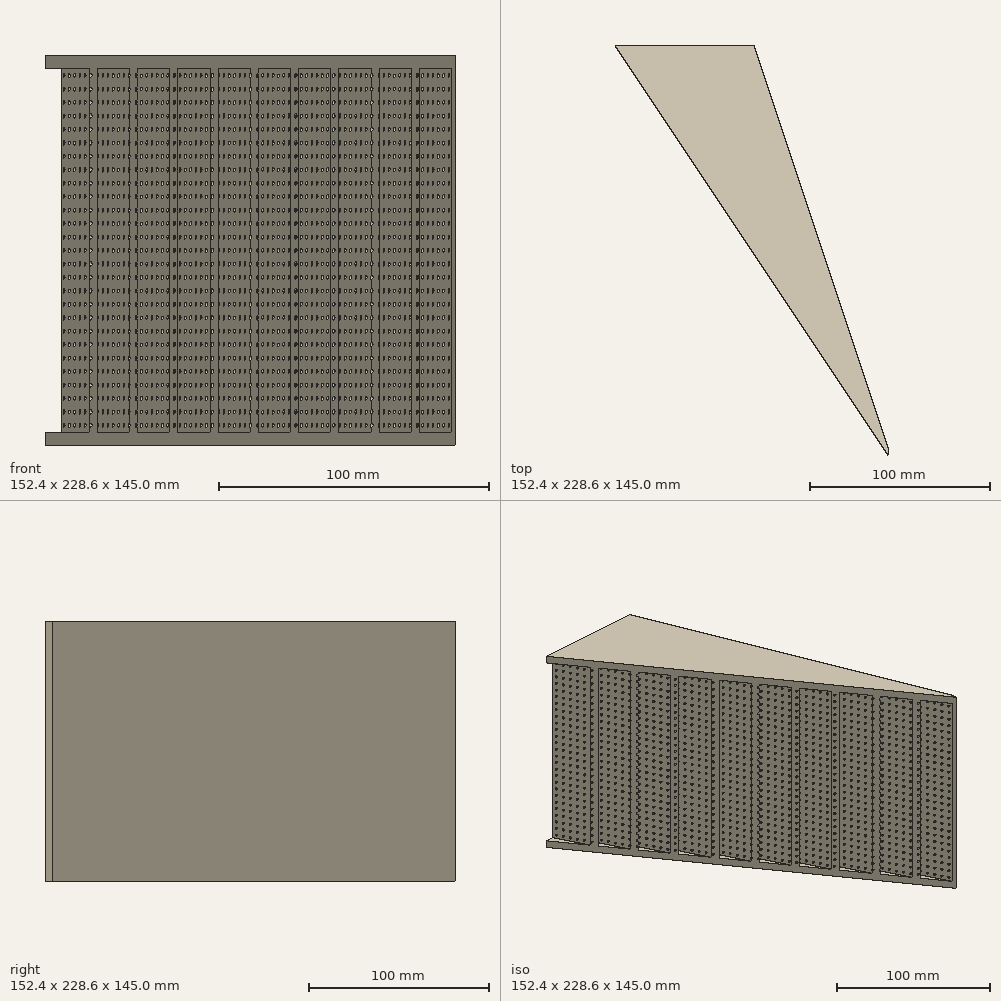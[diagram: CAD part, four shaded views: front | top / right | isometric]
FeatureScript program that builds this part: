
annotation { "Feature Type Name" : "Feature", "Feature Type Description" : "" }
export const myFeature = defineFeature(function(context is Context, id is Id, definition is map)
    precondition{}
    {
        {
            var Q0;
            Q0=qCreatedBy(makeId("Top.planeOp"),FACE);
            var sketch = newSketch(context, id + "F0", { "sketchPlane" : qUnion([Q0])});
            skLineSegment(sketch, "E0", {"start": v(0, -87) * mm, "end": v(0, 141.6) * mm});
            skLineSegment(sketch, "E1", {"start": v(0, -87) * mm, "end": v(-76.2, 141.6) * mm});
            skLineSegment(sketch, "E2", {"start": v(-76.2, 141.6) * mm, "end": v(0, 141.6) * mm});
            skLineSegment(sketch, "E3", {"start": v(0, -87) * mm, "end": v(-152.4, 141.6) * mm});
            skLineSegment(sketch, "E4", {"start": v(-152.4, 141.6) * mm, "end": v(-76.2, 141.6) * mm});
            skLineSegment(sketch, "E5", {"start": v(-97.03, 141.6) * mm, "end": v(0, -87) * mm});
            skLineSegment(sketch, "E6", {"start": v(-102.47, 141.6) * mm, "end": v(-14.95, -64.57) * mm});
            skLineSegment(sketch, "E7", {"start": v(-107.9, 141.6) * mm, "end": v(-29.9, -42.14) * mm});
            skLineSegment(sketch, "E8", {"start": v(-113.33, 141.6) * mm, "end": v(-44.86, -19.7) * mm});
            skLineSegment(sketch, "E9.1.0.0", {"start": v(-118.76, 141.6) * mm, "end": v(-59.8, 2.72) * mm});
            skLineSegment(sketch, "E9.2.0.0", {"start": v(-124.2, 141.6) * mm, "end": v(-74.76, 25.15) * mm});
            skLineSegment(sketch, "E9.3.0.0", {"start": v(-129.63, 141.6) * mm, "end": v(-89.71, 47.57) * mm});
            skLineSegment(sketch, "E9.4.0.0", {"start": v(-135.06, 141.6) * mm, "end": v(-104.66, 70) * mm});
            skLineSegment(sketch, "E9.5.0.0", {"start": v(-140.49, 141.6) * mm, "end": v(-119.61, 92.43) * mm});
            skLineSegment(sketch, "E9.6.0.0", {"start": v(-145.92, 141.6) * mm, "end": v(-134.57, 114.86) * mm});
            skLineSegment(sketch, "E10.1.0.0", {"start": v(-91.6, 141.6) * mm, "end": v(-19.87, -27.4) * mm});
            skLineSegment(sketch, "E10.2.0.0", {"start": v(-86.17, 141.6) * mm, "end": v(-39.73, 32.2) * mm});
            skLineSegment(sketch, "E11", {"start": v(-80.74, 141.6) * mm, "end": v(-59.6, 91.8) * mm});
            skLineSegment(sketch, "E12", {"start": v(-81.28, 141.6) * mm, "end": v(-57.61, 85.84) * mm});
            skLineSegment(sketch, "E13", {"start": v(-80.2, 141.6) * mm, "end": v(-61.58, 97.76) * mm});
            skLineSegment(sketch, "E14", {"start": v(-86.71, 141.6) * mm, "end": v(-37.75, 26.24) * mm});
            skLineSegment(sketch, "E15", {"start": v(-85.63, 141.6) * mm, "end": v(-41.72, 38.16) * mm});
            skLineSegment(sketch, "E16", {"start": v(-92.15, 141.6) * mm, "end": v(-17.88, -33.36) * mm});
            skLineSegment(sketch, "E17", {"start": v(-91.06, 141.6) * mm, "end": v(-21.85, -21.44) * mm});
            skLineSegment(sketch, "E18", {"start": v(-97.58, 141.6) * mm, "end": v(-1.5, -84.75) * mm});
            skLineSegment(sketch, "E19", {"start": v(-96.5, 141.6) * mm, "end": v(-1.99, -81.03) * mm});
            skLineSegment(sketch, "E20", {"start": v(-103, 141.6) * mm, "end": v(-16.45, -62.32) * mm});
            skLineSegment(sketch, "E21", {"start": v(-101.92, 141.6) * mm, "end": v(-13.46, -66.8) * mm});
            skLineSegment(sketch, "E22", {"start": v(-108.44, 141.6) * mm, "end": v(-31.4, -39.9) * mm});
            skLineSegment(sketch, "E23", {"start": v(-107.36, 141.6) * mm, "end": v(-28.4, -44.38) * mm});
            skLineSegment(sketch, "E24", {"start": v(-113.94, 141.76) * mm, "end": v(-46.35, -17.47) * mm});
            skLineSegment(sketch, "E25", {"start": v(-112.79, 141.6) * mm, "end": v(-43.36, -21.95) * mm});
            skLineSegment(sketch, "E26", {"start": v(-119.3, 141.6) * mm, "end": v(-61.3, 4.96) * mm});
            skLineSegment(sketch, "E27", {"start": v(-118.22, 141.6) * mm, "end": v(-58.31, 0.47) * mm});
            skLineSegment(sketch, "E28", {"start": v(-124.74, 141.6) * mm, "end": v(-76.25, 27.39) * mm});
            skLineSegment(sketch, "E29", {"start": v(-123.65, 141.6) * mm, "end": v(-73.26, 22.9) * mm});
            skLineSegment(sketch, "E30", {"start": v(-130.17, 141.6) * mm, "end": v(-91.2, 49.82) * mm});
            skLineSegment(sketch, "E31", {"start": v(-129.08, 141.6) * mm, "end": v(-88.22, 45.33) * mm});
            skLineSegment(sketch, "E32", {"start": v(-134.51, 141.6) * mm, "end": v(-103.17, 67.76) * mm});
            skLineSegment(sketch, "E33", {"start": v(-135.6, 141.6) * mm, "end": v(-106.16, 72.24) * mm});
            skLineSegment(sketch, "E34", {"start": v(-141.03, 141.6) * mm, "end": v(-121.1, 94.67) * mm});
            skLineSegment(sketch, "E35", {"start": v(-139.95, 141.6) * mm, "end": v(-118.12, 90.19) * mm});
            skLineSegment(sketch, "E36", {"start": v(-146.46, 141.6) * mm, "end": v(-136.06, 117.1) * mm});
            skLineSegment(sketch, "E37", {"start": v(-145.38, 141.6) * mm, "end": v(-133.07, 112.61) * mm});
            skPoint(sketch, "E38.endSnap0", {"position": v(-70.9, 119.68) * mm});
            skLineSegment(sketch, "E39", {"start": v(-74.88, 141.6) * mm, "end": v(1.19, -86.6) * mm});
            skLineSegment(sketch, "E40", {"start": v(1.19, -86.6) * mm, "end": v(0, -87) * mm});
            skSolve(sketch);
        }
        {
            var Q0;
            {var subQ0=sQuery(id+"F0.wireOp",EDGE,"E11");Q0=makeQuery(id+"F0.imprint","IMPRINT",FACE,{"disambiguationData":[TD([[makeQuery(id+"F0.imprint","IMPRINT",EDGE,{"derivedFrom":subQ0}),-1.0]])]});}
            var Q1;
            {var subQ0=sQuery(id+"F0.wireOp",EDGE,"E11");Q1=makeQuery(id+"F0.imprint","IMPRINT",FACE,{"disambiguationData":[TD([[makeQuery(id+"F0.imprint","IMPRINT",EDGE,{"derivedFrom":subQ0}),1.0]])]});}
            var Q2;
            {var subQ0=sQuery(id+"F0.wireOp",EDGE,"E10.2.0.0");Q2=makeQuery(id+"F0.imprint","IMPRINT",FACE,{"disambiguationData":[TD([[makeQuery(id+"F0.imprint","IMPRINT",EDGE,{"derivedFrom":subQ0}),1.0]])]});}
            var Q3;
            {var subQ0=sQuery(id+"F0.wireOp",EDGE,"E10.2.0.0");Q3=makeQuery(id+"F0.imprint","IMPRINT",FACE,{"disambiguationData":[TD([[makeQuery(id+"F0.imprint","IMPRINT",EDGE,{"derivedFrom":subQ0}),-1.0]])]});}
            var Q4;
            {var subQ0=sQuery(id+"F0.wireOp",EDGE,"E10.1.0.0");Q4=makeQuery(id+"F0.imprint","IMPRINT",FACE,{"disambiguationData":[TD([[makeQuery(id+"F0.imprint","IMPRINT",EDGE,{"derivedFrom":subQ0}),1.0]])]});}
            var Q5;
            {var subQ0=sQuery(id+"F0.wireOp",EDGE,"E10.1.0.0");Q5=makeQuery(id+"F0.imprint","IMPRINT",FACE,{"disambiguationData":[TD([[makeQuery(id+"F0.imprint","IMPRINT",EDGE,{"derivedFrom":subQ0}),-1.0]])]});}
            var Q6;
            {var subQ0=sQuery(id+"F0.wireOp",EDGE,"E5");Q6=makeQuery(id+"F0.imprint","IMPRINT",FACE,{"disambiguationData":[TD([[makeQuery(id+"F0.imprint","IMPRINT",EDGE,{"derivedFrom":subQ0}),1.0]])]});}
            var Q7;
            {var subQ0=sQuery(id+"F0.wireOp",EDGE,"E5");Q7=makeQuery(id+"F0.imprint","IMPRINT",FACE,{"disambiguationData":[TD([[makeQuery(id+"F0.imprint","IMPRINT",EDGE,{"derivedFrom":subQ0}),-1.0]])]});}
            var Q8;
            {var subQ0=sQuery(id+"F0.wireOp",EDGE,"E6");Q8=makeQuery(id+"F0.imprint","IMPRINT",FACE,{"disambiguationData":[TD([[makeQuery(id+"F0.imprint","IMPRINT",EDGE,{"derivedFrom":subQ0}),1.0]])]});}
            var Q9;
            {var subQ0=sQuery(id+"F0.wireOp",EDGE,"E6");Q9=makeQuery(id+"F0.imprint","IMPRINT",FACE,{"disambiguationData":[TD([[makeQuery(id+"F0.imprint","IMPRINT",EDGE,{"derivedFrom":subQ0}),-1.0]])]});}
            var Q10;
            {var subQ0=sQuery(id+"F0.wireOp",EDGE,"E7");Q10=makeQuery(id+"F0.imprint","IMPRINT",FACE,{"disambiguationData":[TD([[makeQuery(id+"F0.imprint","IMPRINT",EDGE,{"derivedFrom":subQ0}),1.0]])]});}
            var Q11;
            {var subQ0=sQuery(id+"F0.wireOp",EDGE,"E7");Q11=makeQuery(id+"F0.imprint","IMPRINT",FACE,{"disambiguationData":[TD([[makeQuery(id+"F0.imprint","IMPRINT",EDGE,{"derivedFrom":subQ0}),-1.0]])]});}
            var Q12;
            {var subQ0=sQuery(id+"F0.wireOp",EDGE,"E8");Q12=makeQuery(id+"F0.imprint","IMPRINT",FACE,{"disambiguationData":[TD([[makeQuery(id+"F0.imprint","IMPRINT",EDGE,{"derivedFrom":subQ0}),1.0]])]});}
            var Q13;
            {var subQ0=sQuery(id+"F0.wireOp",EDGE,"E8");Q13=makeQuery(id+"F0.imprint","IMPRINT",FACE,{"disambiguationData":[TD([[makeQuery(id+"F0.imprint","IMPRINT",EDGE,{"derivedFrom":subQ0}),-1.0]])]});}
            var Q14;
            {var subQ0=sQuery(id+"F0.wireOp",EDGE,"E9.1.0.0");Q14=makeQuery(id+"F0.imprint","IMPRINT",FACE,{"disambiguationData":[TD([[makeQuery(id+"F0.imprint","IMPRINT",EDGE,{"derivedFrom":subQ0}),1.0]])]});}
            var Q15;
            {var subQ0=sQuery(id+"F0.wireOp",EDGE,"E9.1.0.0");Q15=makeQuery(id+"F0.imprint","IMPRINT",FACE,{"disambiguationData":[TD([[makeQuery(id+"F0.imprint","IMPRINT",EDGE,{"derivedFrom":subQ0}),-1.0]])]});}
            var Q16;
            {var subQ0=sQuery(id+"F0.wireOp",EDGE,"E9.2.0.0");Q16=makeQuery(id+"F0.imprint","IMPRINT",FACE,{"disambiguationData":[TD([[makeQuery(id+"F0.imprint","IMPRINT",EDGE,{"derivedFrom":subQ0}),1.0]])]});}
            var Q17;
            {var subQ0=sQuery(id+"F0.wireOp",EDGE,"E9.2.0.0");Q17=makeQuery(id+"F0.imprint","IMPRINT",FACE,{"disambiguationData":[TD([[makeQuery(id+"F0.imprint","IMPRINT",EDGE,{"derivedFrom":subQ0}),-1.0]])]});}
            var Q18;
            {var subQ0=sQuery(id+"F0.wireOp",EDGE,"E9.3.0.0");Q18=makeQuery(id+"F0.imprint","IMPRINT",FACE,{"disambiguationData":[TD([[makeQuery(id+"F0.imprint","IMPRINT",EDGE,{"derivedFrom":subQ0}),1.0]])]});}
            var Q19;
            {var subQ0=sQuery(id+"F0.wireOp",EDGE,"E9.3.0.0");Q19=makeQuery(id+"F0.imprint","IMPRINT",FACE,{"disambiguationData":[TD([[makeQuery(id+"F0.imprint","IMPRINT",EDGE,{"derivedFrom":subQ0}),-1.0]])]});}
            var Q20;
            {var subQ0=sQuery(id+"F0.wireOp",EDGE,"E9.4.0.0");Q20=makeQuery(id+"F0.imprint","IMPRINT",FACE,{"disambiguationData":[TD([[makeQuery(id+"F0.imprint","IMPRINT",EDGE,{"derivedFrom":subQ0}),1.0]])]});}
            var Q21;
            {var subQ0=sQuery(id+"F0.wireOp",EDGE,"E9.4.0.0");Q21=makeQuery(id+"F0.imprint","IMPRINT",FACE,{"disambiguationData":[TD([[makeQuery(id+"F0.imprint","IMPRINT",EDGE,{"derivedFrom":subQ0}),-1.0]])]});}
            var Q22;
            {var subQ0=sQuery(id+"F0.wireOp",EDGE,"E9.5.0.0");Q22=makeQuery(id+"F0.imprint","IMPRINT",FACE,{"disambiguationData":[TD([[makeQuery(id+"F0.imprint","IMPRINT",EDGE,{"derivedFrom":subQ0}),1.0]])]});}
            var Q23;
            {var subQ0=sQuery(id+"F0.wireOp",EDGE,"E9.5.0.0");Q23=makeQuery(id+"F0.imprint","IMPRINT",FACE,{"disambiguationData":[TD([[makeQuery(id+"F0.imprint","IMPRINT",EDGE,{"derivedFrom":subQ0}),-1.0]])]});}
            var Q24;
            {var subQ0=sQuery(id+"F0.wireOp",EDGE,"E9.6.0.0");Q24=makeQuery(id+"F0.imprint","IMPRINT",FACE,{"disambiguationData":[TD([[makeQuery(id+"F0.imprint","IMPRINT",EDGE,{"derivedFrom":subQ0}),1.0]])]});}
            var Q25;
            {var subQ0=sQuery(id+"F0.wireOp",EDGE,"E9.6.0.0");Q25=makeQuery(id+"F0.imprint","IMPRINT",FACE,{"disambiguationData":[TD([[makeQuery(id+"F0.imprint","IMPRINT",EDGE,{"derivedFrom":subQ0}),-1.0]])]});}
            extrude(context, id + "F1", {"entities" : qUnion([Q0, Q1, Q2, Q3, Q4, Q5, Q6, Q7, Q8, Q9, Q10, Q11, Q12, Q13, Q14, Q15, Q16, Q17, Q18, Q19, Q20, Q21, Q22, Q23, Q24, Q25]), "depth" : 135 * mm, "offsetDistance" : 25 * mm});
        }
        {
            var Q0;
            Q0=makeQuery(id+"F1.opExtrude","SWEPT_FACE",FACE,{"disambiguationData":[OSD([sQuery(id+"F0.wireOp",EDGE,"E18")])]});
            var sketch = newSketch(context, id + "F2", { "sketchPlane" : qUnion([Q0])});
            skLineSegment(sketch, "E41", {"start": v(77.43, 195) * mm, "end": v(77.43, 135) * mm});
            skLineSegment(sketch, "E42", {"start": v(72.43, 135) * mm, "end": v(77.43, 135) * mm});
            skCircle(sketch, "E43", {"center": v(75, 197.44) * mm, "radius": 0.8 * mm});
            skCircle(sketch, "E44.0.1.0", {"center": v(75, 192.44) * mm, "radius": 0.8 * mm});
            skCircle(sketch, "E44.1.0.0", {"center": v(70, 197.44) * mm, "radius": 0.8 * mm});
            skCircle(sketch, "E44.1.1.0", {"center": v(70, 192.44) * mm, "radius": 0.8 * mm});
            skCircle(sketch, "E44.2.0.0", {"center": v(65, 197.44) * mm, "radius": 0.8 * mm});
            skCircle(sketch, "E44.2.1.0", {"center": v(65, 192.44) * mm, "radius": 0.8 * mm});
            skCircle(sketch, "E44.3.0.0", {"center": v(60, 197.44) * mm, "radius": 0.8 * mm});
            skCircle(sketch, "E44.3.1.0", {"center": v(60, 192.44) * mm, "radius": 0.8 * mm});
            skCircle(sketch, "E44.4.0.0", {"center": v(55, 197.44) * mm, "radius": 0.8 * mm});
            skCircle(sketch, "E44.4.1.0", {"center": v(55, 192.44) * mm, "radius": 0.8 * mm});
            skCircle(sketch, "E44.5.0.0", {"center": v(50, 197.44) * mm, "radius": 0.8 * mm});
            skCircle(sketch, "E44.5.1.0", {"center": v(50, 192.44) * mm, "radius": 0.8 * mm});
            skCircle(sketch, "E44.6.0.0", {"center": v(45, 197.44) * mm, "radius": 0.8 * mm});
            skCircle(sketch, "E44.6.1.0", {"center": v(45, 192.44) * mm, "radius": 0.8 * mm});
            skCircle(sketch, "E44.7.0.0", {"center": v(40, 197.44) * mm, "radius": 0.8 * mm});
            skCircle(sketch, "E44.7.1.0", {"center": v(40, 192.44) * mm, "radius": 0.8 * mm});
            skCircle(sketch, "E44.8.0.0", {"center": v(35, 197.44) * mm, "radius": 0.8 * mm});
            skCircle(sketch, "E44.8.1.0", {"center": v(35, 192.44) * mm, "radius": 0.8 * mm});
            skCircle(sketch, "E44.9.0.0", {"center": v(30, 197.44) * mm, "radius": 0.8 * mm});
            skCircle(sketch, "E44.9.1.0", {"center": v(30, 192.44) * mm, "radius": 0.8 * mm});
            skCircle(sketch, "E44.10.0.0", {"center": v(25, 197.44) * mm, "radius": 0.8 * mm});
            skCircle(sketch, "E44.10.1.0", {"center": v(25, 192.44) * mm, "radius": 0.8 * mm});
            skCircle(sketch, "E44.11.0.0", {"center": v(20, 197.44) * mm, "radius": 0.8 * mm});
            skCircle(sketch, "E44.11.1.0", {"center": v(20, 192.44) * mm, "radius": 0.8 * mm});
            skCircle(sketch, "E44.12.0.0", {"center": v(15, 197.44) * mm, "radius": 0.8 * mm});
            skCircle(sketch, "E44.12.1.0", {"center": v(15, 192.44) * mm, "radius": 0.8 * mm});
            skCircle(sketch, "E44.13.0.0", {"center": v(10, 197.44) * mm, "radius": 0.8 * mm});
            skCircle(sketch, "E44.13.1.0", {"center": v(10, 192.44) * mm, "radius": 0.8 * mm});
            skCircle(sketch, "E44.14.0.0", {"center": v(5, 197.44) * mm, "radius": 0.8 * mm});
            skCircle(sketch, "E44.14.1.0", {"center": v(5, 192.44) * mm, "radius": 0.8 * mm});
            skCircle(sketch, "E44.15.0.0", {"center": v(0, 197.44) * mm, "radius": 0.8 * mm});
            skCircle(sketch, "E44.15.1.0", {"center": v(0, 192.44) * mm, "radius": 0.8 * mm});
            skCircle(sketch, "E44.16.0.0", {"center": v(-5, 197.44) * mm, "radius": 0.8 * mm});
            skCircle(sketch, "E44.16.1.0", {"center": v(-5, 192.44) * mm, "radius": 0.8 * mm});
            skCircle(sketch, "E44.17.0.0", {"center": v(-10, 197.44) * mm, "radius": 0.8 * mm});
            skCircle(sketch, "E44.17.1.0", {"center": v(-10, 192.44) * mm, "radius": 0.8 * mm});
            skCircle(sketch, "E44.18.0.0", {"center": v(-15, 197.44) * mm, "radius": 0.8 * mm});
            skCircle(sketch, "E44.18.1.0", {"center": v(-15, 192.44) * mm, "radius": 0.8 * mm});
            skCircle(sketch, "E44.19.0.0", {"center": v(-20, 197.44) * mm, "radius": 0.8 * mm});
            skCircle(sketch, "E44.19.1.0", {"center": v(-20, 192.44) * mm, "radius": 0.8 * mm});
            skCircle(sketch, "E44.20.0.0", {"center": v(-25, 197.44) * mm, "radius": 0.8 * mm});
            skCircle(sketch, "E44.20.1.0", {"center": v(-25, 192.44) * mm, "radius": 0.8 * mm});
            skCircle(sketch, "E44.21.0.0", {"center": v(-30, 197.44) * mm, "radius": 0.8 * mm});
            skCircle(sketch, "E44.21.1.0", {"center": v(-30, 192.44) * mm, "radius": 0.8 * mm});
            skCircle(sketch, "E44.22.0.0", {"center": v(-35, 197.44) * mm, "radius": 0.8 * mm});
            skCircle(sketch, "E44.22.1.0", {"center": v(-35, 192.44) * mm, "radius": 0.8 * mm});
            skCircle(sketch, "E44.23.0.0", {"center": v(-40, 197.44) * mm, "radius": 0.8 * mm});
            skCircle(sketch, "E44.23.1.0", {"center": v(-40, 192.44) * mm, "radius": 0.8 * mm});
            skCircle(sketch, "E44.24.0.0", {"center": v(-45, 197.44) * mm, "radius": 0.8 * mm});
            skCircle(sketch, "E44.24.1.0", {"center": v(-45, 192.44) * mm, "radius": 0.8 * mm});
            skCircle(sketch, "E44.25.0.0", {"center": v(-50, 197.44) * mm, "radius": 0.8 * mm});
            skCircle(sketch, "E44.25.1.0", {"center": v(-50, 192.44) * mm, "radius": 0.8 * mm});
            skCircle(sketch, "E44.26.0.0", {"center": v(-55, 197.44) * mm, "radius": 0.8 * mm});
            skCircle(sketch, "E44.26.1.0", {"center": v(-55, 192.44) * mm, "radius": 0.8 * mm});
            skCircle(sketch, "E44.27.0.0", {"center": v(-60, 197.44) * mm, "radius": 0.8 * mm});
            skCircle(sketch, "E44.27.1.0", {"center": v(-60, 192.44) * mm, "radius": 0.8 * mm});
            skCircle(sketch, "E44.28.0.0", {"center": v(-65, 197.44) * mm, "radius": 0.8 * mm});
            skCircle(sketch, "E44.28.1.0", {"center": v(-65, 192.44) * mm, "radius": 0.8 * mm});
            skCircle(sketch, "E44.29.0.0", {"center": v(-70, 197.44) * mm, "radius": 0.8 * mm});
            skCircle(sketch, "E44.29.1.0", {"center": v(-70, 192.44) * mm, "radius": 0.8 * mm});
            skCircle(sketch, "E44.30.0.0", {"center": v(-75, 197.44) * mm, "radius": 0.8 * mm});
            skCircle(sketch, "E44.30.1.0", {"center": v(-75, 192.44) * mm, "radius": 0.8 * mm});
            skCircle(sketch, "E44.31.0.0", {"center": v(-80, 197.44) * mm, "radius": 0.8 * mm});
            skCircle(sketch, "E44.31.1.0", {"center": v(-80, 192.44) * mm, "radius": 0.8 * mm});
            skCircle(sketch, "E44.32.0.0", {"center": v(-85, 197.44) * mm, "radius": 0.8 * mm});
            skCircle(sketch, "E44.32.1.0", {"center": v(-85, 192.44) * mm, "radius": 0.8 * mm});
            skCircle(sketch, "E44.33.0.0", {"center": v(-90, 197.44) * mm, "radius": 0.8 * mm});
            skCircle(sketch, "E44.33.1.0", {"center": v(-90, 192.44) * mm, "radius": 0.8 * mm});
            skCircle(sketch, "E44.34.0.0", {"center": v(-95, 197.44) * mm, "radius": 0.8 * mm});
            skCircle(sketch, "E44.34.1.0", {"center": v(-95, 192.44) * mm, "radius": 0.8 * mm});
            skCircle(sketch, "E44.35.0.0", {"center": v(-100, 197.44) * mm, "radius": 0.8 * mm});
            skCircle(sketch, "E44.35.1.0", {"center": v(-100, 192.44) * mm, "radius": 0.8 * mm});
            skCircle(sketch, "E44.36.0.0", {"center": v(-105, 197.44) * mm, "radius": 0.8 * mm});
            skCircle(sketch, "E44.36.1.0", {"center": v(-105, 192.44) * mm, "radius": 0.8 * mm});
            skCircle(sketch, "E44.37.0.0", {"center": v(-110, 197.44) * mm, "radius": 0.8 * mm});
            skCircle(sketch, "E44.37.1.0", {"center": v(-110, 192.44) * mm, "radius": 0.8 * mm});
            skCircle(sketch, "E44.38.0.0", {"center": v(-115, 197.44) * mm, "radius": 0.8 * mm});
            skCircle(sketch, "E44.38.1.0", {"center": v(-115, 192.44) * mm, "radius": 0.8 * mm});
            skCircle(sketch, "E44.39.0.0", {"center": v(-120, 197.44) * mm, "radius": 0.8 * mm});
            skCircle(sketch, "E44.39.1.0", {"center": v(-120, 192.44) * mm, "radius": 0.8 * mm});
            skCircle(sketch, "E44.40.0.0", {"center": v(-125, 197.44) * mm, "radius": 0.8 * mm});
            skCircle(sketch, "E44.40.1.0", {"center": v(-125, 192.44) * mm, "radius": 0.8 * mm});
            skCircle(sketch, "E44.41.0.0", {"center": v(-130, 197.44) * mm, "radius": 0.8 * mm});
            skCircle(sketch, "E44.41.1.0", {"center": v(-130, 192.44) * mm, "radius": 0.8 * mm});
            skCircle(sketch, "E44.42.0.0", {"center": v(-135, 197.44) * mm, "radius": 0.8 * mm});
            skCircle(sketch, "E44.42.1.0", {"center": v(-135, 192.44) * mm, "radius": 0.8 * mm});
            skCircle(sketch, "E44.43.0.0", {"center": v(-140, 197.44) * mm, "radius": 0.8 * mm});
            skCircle(sketch, "E44.43.1.0", {"center": v(-140, 192.44) * mm, "radius": 0.8 * mm});
            skCircle(sketch, "E44.44.0.0", {"center": v(-145, 197.44) * mm, "radius": 0.8 * mm});
            skCircle(sketch, "E44.44.1.0", {"center": v(-145, 192.44) * mm, "radius": 0.8 * mm});
            skCircle(sketch, "E44.45.0.0", {"center": v(-150, 197.44) * mm, "radius": 0.8 * mm});
            skCircle(sketch, "E44.45.1.0", {"center": v(-150, 192.44) * mm, "radius": 0.8 * mm});
            skCircle(sketch, "E44.46.0.0", {"center": v(-155, 197.44) * mm, "radius": 0.8 * mm});
            skCircle(sketch, "E44.46.1.0", {"center": v(-155, 192.44) * mm, "radius": 0.8 * mm});
            skCircle(sketch, "E44.47.0.0", {"center": v(-160, 197.44) * mm, "radius": 0.8 * mm});
            skCircle(sketch, "E44.47.1.0", {"center": v(-160, 192.44) * mm, "radius": 0.8 * mm});
            skCircle(sketch, "E44.48.0.0", {"center": v(-165, 197.44) * mm, "radius": 0.8 * mm});
            skCircle(sketch, "E44.48.1.0", {"center": v(-165, 192.44) * mm, "radius": 0.8 * mm});
            skLineSegment(sketch, "E44.direction1", {"start": v(75, 197.44) * mm, "end": v(70, 197.44) * mm, "construction": true});
            skLineSegment(sketch, "E44.direction2", {"start": v(75, 197.44) * mm, "end": v(75, 192.44) * mm, "construction": true});
            skCircle(sketch, "E45.0.0.2", {"center": v(75, 187.44) * mm, "radius": 0.8 * mm});
            skCircle(sketch, "E45.0.0.3", {"center": v(75, 182.44) * mm, "radius": 0.8 * mm});
            skCircle(sketch, "E45.0.0.4", {"center": v(75, 177.44) * mm, "radius": 0.8 * mm});
            skCircle(sketch, "E45.0.0.5", {"center": v(75, 172.44) * mm, "radius": 0.8 * mm});
            skCircle(sketch, "E45.0.0.6", {"center": v(75, 167.44) * mm, "radius": 0.8 * mm});
            skCircle(sketch, "E45.0.0.7", {"center": v(75, 162.44) * mm, "radius": 0.8 * mm});
            skCircle(sketch, "E45.0.0.8", {"center": v(75, 157.44) * mm, "radius": 0.8 * mm});
            skCircle(sketch, "E45.0.0.9", {"center": v(75, 152.44) * mm, "radius": 0.8 * mm});
            skCircle(sketch, "E45.0.0.10", {"center": v(75, 147.44) * mm, "radius": 0.8 * mm});
            skCircle(sketch, "E45.0.0.11", {"center": v(75, 142.44) * mm, "radius": 0.8 * mm});
            skCircle(sketch, "E45.0.0.12", {"center": v(75, 137.44) * mm, "radius": 0.8 * mm});
            skCircle(sketch, "E45.0.0.13", {"center": v(75, 132.44) * mm, "radius": 0.8 * mm});
            skCircle(sketch, "E45.0.0.14", {"center": v(75, 127.44) * mm, "radius": 0.8 * mm});
            skCircle(sketch, "E45.0.0.15", {"center": v(75, 122.44) * mm, "radius": 0.8 * mm});
            skCircle(sketch, "E45.0.0.16", {"center": v(75, 117.44) * mm, "radius": 0.8 * mm});
            skCircle(sketch, "E45.0.0.17", {"center": v(75, 112.44) * mm, "radius": 0.8 * mm});
            skCircle(sketch, "E45.0.0.18", {"center": v(75, 107.44) * mm, "radius": 0.8 * mm});
            skCircle(sketch, "E45.0.0.19", {"center": v(75, 102.44) * mm, "radius": 0.8 * mm});
            skCircle(sketch, "E45.0.0.20", {"center": v(75, 97.44) * mm, "radius": 0.8 * mm});
            skCircle(sketch, "E45.0.0.21", {"center": v(75, 92.44) * mm, "radius": 0.8 * mm});
            skCircle(sketch, "E45.0.0.22", {"center": v(75, 87.44) * mm, "radius": 0.8 * mm});
            skCircle(sketch, "E45.0.0.23", {"center": v(75, 82.44) * mm, "radius": 0.8 * mm});
            skCircle(sketch, "E45.0.0.24", {"center": v(75, 77.44) * mm, "radius": 0.8 * mm});
            skCircle(sketch, "E45.0.0.25", {"center": v(75, 72.44) * mm, "radius": 0.8 * mm});
            skCircle(sketch, "E45.0.0.26", {"center": v(75, 67.44) * mm, "radius": 0.8 * mm});
            skCircle(sketch, "E45.0.0.27", {"center": v(75, 62.44) * mm, "radius": 0.8 * mm});
            skCircle(sketch, "E45.0.0.28", {"center": v(75, 57.44) * mm, "radius": 0.8 * mm});
            skCircle(sketch, "E45.0.0.29", {"center": v(75, 52.44) * mm, "radius": 0.8 * mm});
            skCircle(sketch, "E45.0.1.2", {"center": v(70, 187.44) * mm, "radius": 0.8 * mm});
            skCircle(sketch, "E45.0.1.3", {"center": v(70, 182.44) * mm, "radius": 0.8 * mm});
            skCircle(sketch, "E45.0.1.4", {"center": v(70, 177.44) * mm, "radius": 0.8 * mm});
            skCircle(sketch, "E45.0.1.5", {"center": v(70, 172.44) * mm, "radius": 0.8 * mm});
            skCircle(sketch, "E45.0.1.6", {"center": v(70, 167.44) * mm, "radius": 0.8 * mm});
            skCircle(sketch, "E45.0.1.7", {"center": v(70, 162.44) * mm, "radius": 0.8 * mm});
            skCircle(sketch, "E45.0.1.8", {"center": v(70, 157.44) * mm, "radius": 0.8 * mm});
            skCircle(sketch, "E45.0.1.9", {"center": v(70, 152.44) * mm, "radius": 0.8 * mm});
            skCircle(sketch, "E45.0.1.10", {"center": v(70, 147.44) * mm, "radius": 0.8 * mm});
            skCircle(sketch, "E45.0.1.11", {"center": v(70, 142.44) * mm, "radius": 0.8 * mm});
            skCircle(sketch, "E45.0.1.12", {"center": v(70, 137.44) * mm, "radius": 0.8 * mm});
            skCircle(sketch, "E45.0.1.13", {"center": v(70, 132.44) * mm, "radius": 0.8 * mm});
            skCircle(sketch, "E45.0.1.14", {"center": v(70, 127.44) * mm, "radius": 0.8 * mm});
            skCircle(sketch, "E45.0.1.15", {"center": v(70, 122.44) * mm, "radius": 0.8 * mm});
            skCircle(sketch, "E45.0.1.16", {"center": v(70, 117.44) * mm, "radius": 0.8 * mm});
            skCircle(sketch, "E45.0.1.17", {"center": v(70, 112.44) * mm, "radius": 0.8 * mm});
            skCircle(sketch, "E45.0.1.18", {"center": v(70, 107.44) * mm, "radius": 0.8 * mm});
            skCircle(sketch, "E45.0.1.19", {"center": v(70, 102.44) * mm, "radius": 0.8 * mm});
            skCircle(sketch, "E45.0.1.20", {"center": v(70, 97.44) * mm, "radius": 0.8 * mm});
            skCircle(sketch, "E45.0.1.21", {"center": v(70, 92.44) * mm, "radius": 0.8 * mm});
            skCircle(sketch, "E45.0.1.22", {"center": v(70, 87.44) * mm, "radius": 0.8 * mm});
            skCircle(sketch, "E45.0.1.23", {"center": v(70, 82.44) * mm, "radius": 0.8 * mm});
            skCircle(sketch, "E45.0.1.24", {"center": v(70, 77.44) * mm, "radius": 0.8 * mm});
            skCircle(sketch, "E45.0.1.25", {"center": v(70, 72.44) * mm, "radius": 0.8 * mm});
            skCircle(sketch, "E45.0.1.26", {"center": v(70, 67.44) * mm, "radius": 0.8 * mm});
            skCircle(sketch, "E45.0.1.27", {"center": v(70, 62.44) * mm, "radius": 0.8 * mm});
            skCircle(sketch, "E45.0.1.28", {"center": v(70, 57.44) * mm, "radius": 0.8 * mm});
            skCircle(sketch, "E45.0.1.29", {"center": v(70, 52.44) * mm, "radius": 0.8 * mm});
            skCircle(sketch, "E45.0.2.2", {"center": v(65, 187.44) * mm, "radius": 0.8 * mm});
            skCircle(sketch, "E45.0.2.3", {"center": v(65, 182.44) * mm, "radius": 0.8 * mm});
            skCircle(sketch, "E45.0.2.4", {"center": v(65, 177.44) * mm, "radius": 0.8 * mm});
            skCircle(sketch, "E45.0.2.5", {"center": v(65, 172.44) * mm, "radius": 0.8 * mm});
            skCircle(sketch, "E45.0.2.6", {"center": v(65, 167.44) * mm, "radius": 0.8 * mm});
            skCircle(sketch, "E45.0.2.7", {"center": v(65, 162.44) * mm, "radius": 0.8 * mm});
            skCircle(sketch, "E45.0.2.8", {"center": v(65, 157.44) * mm, "radius": 0.8 * mm});
            skCircle(sketch, "E45.0.2.9", {"center": v(65, 152.44) * mm, "radius": 0.8 * mm});
            skCircle(sketch, "E45.0.2.10", {"center": v(65, 147.44) * mm, "radius": 0.8 * mm});
            skCircle(sketch, "E45.0.2.11", {"center": v(65, 142.44) * mm, "radius": 0.8 * mm});
            skCircle(sketch, "E45.0.2.12", {"center": v(65, 137.44) * mm, "radius": 0.8 * mm});
            skCircle(sketch, "E45.0.2.13", {"center": v(65, 132.44) * mm, "radius": 0.8 * mm});
            skCircle(sketch, "E45.0.2.14", {"center": v(65, 127.44) * mm, "radius": 0.8 * mm});
            skCircle(sketch, "E45.0.2.15", {"center": v(65, 122.44) * mm, "radius": 0.8 * mm});
            skCircle(sketch, "E45.0.2.16", {"center": v(65, 117.44) * mm, "radius": 0.8 * mm});
            skCircle(sketch, "E45.0.2.17", {"center": v(65, 112.44) * mm, "radius": 0.8 * mm});
            skCircle(sketch, "E45.0.2.18", {"center": v(65, 107.44) * mm, "radius": 0.8 * mm});
            skCircle(sketch, "E45.0.2.19", {"center": v(65, 102.44) * mm, "radius": 0.8 * mm});
            skCircle(sketch, "E45.0.2.20", {"center": v(65, 97.44) * mm, "radius": 0.8 * mm});
            skCircle(sketch, "E45.0.2.21", {"center": v(65, 92.44) * mm, "radius": 0.8 * mm});
            skCircle(sketch, "E45.0.2.22", {"center": v(65, 87.44) * mm, "radius": 0.8 * mm});
            skCircle(sketch, "E45.0.2.23", {"center": v(65, 82.44) * mm, "radius": 0.8 * mm});
            skCircle(sketch, "E45.0.2.24", {"center": v(65, 77.44) * mm, "radius": 0.8 * mm});
            skCircle(sketch, "E45.0.2.25", {"center": v(65, 72.44) * mm, "radius": 0.8 * mm});
            skCircle(sketch, "E45.0.2.26", {"center": v(65, 67.44) * mm, "radius": 0.8 * mm});
            skCircle(sketch, "E45.0.2.27", {"center": v(65, 62.44) * mm, "radius": 0.8 * mm});
            skCircle(sketch, "E45.0.2.28", {"center": v(65, 57.44) * mm, "radius": 0.8 * mm});
            skCircle(sketch, "E45.0.2.29", {"center": v(65, 52.44) * mm, "radius": 0.8 * mm});
            skCircle(sketch, "E45.0.3.2", {"center": v(60, 187.44) * mm, "radius": 0.8 * mm});
            skCircle(sketch, "E45.0.3.3", {"center": v(60, 182.44) * mm, "radius": 0.8 * mm});
            skCircle(sketch, "E45.0.3.4", {"center": v(60, 177.44) * mm, "radius": 0.8 * mm});
            skCircle(sketch, "E45.0.3.5", {"center": v(60, 172.44) * mm, "radius": 0.8 * mm});
            skCircle(sketch, "E45.0.3.6", {"center": v(60, 167.44) * mm, "radius": 0.8 * mm});
            skCircle(sketch, "E45.0.3.7", {"center": v(60, 162.44) * mm, "radius": 0.8 * mm});
            skCircle(sketch, "E45.0.3.8", {"center": v(60, 157.44) * mm, "radius": 0.8 * mm});
            skCircle(sketch, "E45.0.3.9", {"center": v(60, 152.44) * mm, "radius": 0.8 * mm});
            skCircle(sketch, "E45.0.3.10", {"center": v(60, 147.44) * mm, "radius": 0.8 * mm});
            skCircle(sketch, "E45.0.3.11", {"center": v(60, 142.44) * mm, "radius": 0.8 * mm});
            skCircle(sketch, "E45.0.3.12", {"center": v(60, 137.44) * mm, "radius": 0.8 * mm});
            skCircle(sketch, "E45.0.3.13", {"center": v(60, 132.44) * mm, "radius": 0.8 * mm});
            skCircle(sketch, "E45.0.3.14", {"center": v(60, 127.44) * mm, "radius": 0.8 * mm});
            skCircle(sketch, "E45.0.3.15", {"center": v(60, 122.44) * mm, "radius": 0.8 * mm});
            skCircle(sketch, "E45.0.3.16", {"center": v(60, 117.44) * mm, "radius": 0.8 * mm});
            skCircle(sketch, "E45.0.3.17", {"center": v(60, 112.44) * mm, "radius": 0.8 * mm});
            skCircle(sketch, "E45.0.3.18", {"center": v(60, 107.44) * mm, "radius": 0.8 * mm});
            skCircle(sketch, "E45.0.3.19", {"center": v(60, 102.44) * mm, "radius": 0.8 * mm});
            skCircle(sketch, "E45.0.3.20", {"center": v(60, 97.44) * mm, "radius": 0.8 * mm});
            skCircle(sketch, "E45.0.3.21", {"center": v(60, 92.44) * mm, "radius": 0.8 * mm});
            skCircle(sketch, "E45.0.3.22", {"center": v(60, 87.44) * mm, "radius": 0.8 * mm});
            skCircle(sketch, "E45.0.3.23", {"center": v(60, 82.44) * mm, "radius": 0.8 * mm});
            skCircle(sketch, "E45.0.3.24", {"center": v(60, 77.44) * mm, "radius": 0.8 * mm});
            skCircle(sketch, "E45.0.3.25", {"center": v(60, 72.44) * mm, "radius": 0.8 * mm});
            skCircle(sketch, "E45.0.3.26", {"center": v(60, 67.44) * mm, "radius": 0.8 * mm});
            skCircle(sketch, "E45.0.3.27", {"center": v(60, 62.44) * mm, "radius": 0.8 * mm});
            skCircle(sketch, "E45.0.3.28", {"center": v(60, 57.44) * mm, "radius": 0.8 * mm});
            skCircle(sketch, "E45.0.3.29", {"center": v(60, 52.44) * mm, "radius": 0.8 * mm});
            skCircle(sketch, "E45.0.4.2", {"center": v(55, 187.44) * mm, "radius": 0.8 * mm});
            skCircle(sketch, "E45.0.4.3", {"center": v(55, 182.44) * mm, "radius": 0.8 * mm});
            skCircle(sketch, "E45.0.4.4", {"center": v(55, 177.44) * mm, "radius": 0.8 * mm});
            skCircle(sketch, "E45.0.4.5", {"center": v(55, 172.44) * mm, "radius": 0.8 * mm});
            skCircle(sketch, "E45.0.4.6", {"center": v(55, 167.44) * mm, "radius": 0.8 * mm});
            skCircle(sketch, "E45.0.4.7", {"center": v(55, 162.44) * mm, "radius": 0.8 * mm});
            skCircle(sketch, "E45.0.4.8", {"center": v(55, 157.44) * mm, "radius": 0.8 * mm});
            skCircle(sketch, "E45.0.4.9", {"center": v(55, 152.44) * mm, "radius": 0.8 * mm});
            skCircle(sketch, "E45.0.4.10", {"center": v(55, 147.44) * mm, "radius": 0.8 * mm});
            skCircle(sketch, "E45.0.4.11", {"center": v(55, 142.44) * mm, "radius": 0.8 * mm});
            skCircle(sketch, "E45.0.4.12", {"center": v(55, 137.44) * mm, "radius": 0.8 * mm});
            skCircle(sketch, "E45.0.4.13", {"center": v(55, 132.44) * mm, "radius": 0.8 * mm});
            skCircle(sketch, "E45.0.4.14", {"center": v(55, 127.44) * mm, "radius": 0.8 * mm});
            skCircle(sketch, "E45.0.4.15", {"center": v(55, 122.44) * mm, "radius": 0.8 * mm});
            skCircle(sketch, "E45.0.4.16", {"center": v(55, 117.44) * mm, "radius": 0.8 * mm});
            skCircle(sketch, "E45.0.4.17", {"center": v(55, 112.44) * mm, "radius": 0.8 * mm});
            skCircle(sketch, "E45.0.4.18", {"center": v(55, 107.44) * mm, "radius": 0.8 * mm});
            skCircle(sketch, "E45.0.4.19", {"center": v(55, 102.44) * mm, "radius": 0.8 * mm});
            skCircle(sketch, "E45.0.4.20", {"center": v(55, 97.44) * mm, "radius": 0.8 * mm});
            skCircle(sketch, "E45.0.4.21", {"center": v(55, 92.44) * mm, "radius": 0.8 * mm});
            skCircle(sketch, "E45.0.4.22", {"center": v(55, 87.44) * mm, "radius": 0.8 * mm});
            skCircle(sketch, "E45.0.4.23", {"center": v(55, 82.44) * mm, "radius": 0.8 * mm});
            skCircle(sketch, "E45.0.4.24", {"center": v(55, 77.44) * mm, "radius": 0.8 * mm});
            skCircle(sketch, "E45.0.4.25", {"center": v(55, 72.44) * mm, "radius": 0.8 * mm});
            skCircle(sketch, "E45.0.4.26", {"center": v(55, 67.44) * mm, "radius": 0.8 * mm});
            skCircle(sketch, "E45.0.4.27", {"center": v(55, 62.44) * mm, "radius": 0.8 * mm});
            skCircle(sketch, "E45.0.4.28", {"center": v(55, 57.44) * mm, "radius": 0.8 * mm});
            skCircle(sketch, "E45.0.4.29", {"center": v(55, 52.44) * mm, "radius": 0.8 * mm});
            skCircle(sketch, "E45.0.5.2", {"center": v(50, 187.44) * mm, "radius": 0.8 * mm});
            skCircle(sketch, "E45.0.5.3", {"center": v(50, 182.44) * mm, "radius": 0.8 * mm});
            skCircle(sketch, "E45.0.5.4", {"center": v(50, 177.44) * mm, "radius": 0.8 * mm});
            skCircle(sketch, "E45.0.5.5", {"center": v(50, 172.44) * mm, "radius": 0.8 * mm});
            skCircle(sketch, "E45.0.5.6", {"center": v(50, 167.44) * mm, "radius": 0.8 * mm});
            skCircle(sketch, "E45.0.5.7", {"center": v(50, 162.44) * mm, "radius": 0.8 * mm});
            skCircle(sketch, "E45.0.5.8", {"center": v(50, 157.44) * mm, "radius": 0.8 * mm});
            skCircle(sketch, "E45.0.5.9", {"center": v(50, 152.44) * mm, "radius": 0.8 * mm});
            skCircle(sketch, "E45.0.5.10", {"center": v(50, 147.44) * mm, "radius": 0.8 * mm});
            skCircle(sketch, "E45.0.5.11", {"center": v(50, 142.44) * mm, "radius": 0.8 * mm});
            skCircle(sketch, "E45.0.5.12", {"center": v(50, 137.44) * mm, "radius": 0.8 * mm});
            skCircle(sketch, "E45.0.5.13", {"center": v(50, 132.44) * mm, "radius": 0.8 * mm});
            skCircle(sketch, "E45.0.5.14", {"center": v(50, 127.44) * mm, "radius": 0.8 * mm});
            skCircle(sketch, "E45.0.5.15", {"center": v(50, 122.44) * mm, "radius": 0.8 * mm});
            skCircle(sketch, "E45.0.5.16", {"center": v(50, 117.44) * mm, "radius": 0.8 * mm});
            skCircle(sketch, "E45.0.5.17", {"center": v(50, 112.44) * mm, "radius": 0.8 * mm});
            skCircle(sketch, "E45.0.5.18", {"center": v(50, 107.44) * mm, "radius": 0.8 * mm});
            skCircle(sketch, "E45.0.5.19", {"center": v(50, 102.44) * mm, "radius": 0.8 * mm});
            skCircle(sketch, "E45.0.5.20", {"center": v(50, 97.44) * mm, "radius": 0.8 * mm});
            skCircle(sketch, "E45.0.5.21", {"center": v(50, 92.44) * mm, "radius": 0.8 * mm});
            skCircle(sketch, "E45.0.5.22", {"center": v(50, 87.44) * mm, "radius": 0.8 * mm});
            skCircle(sketch, "E45.0.5.23", {"center": v(50, 82.44) * mm, "radius": 0.8 * mm});
            skCircle(sketch, "E45.0.5.24", {"center": v(50, 77.44) * mm, "radius": 0.8 * mm});
            skCircle(sketch, "E45.0.5.25", {"center": v(50, 72.44) * mm, "radius": 0.8 * mm});
            skCircle(sketch, "E45.0.5.26", {"center": v(50, 67.44) * mm, "radius": 0.8 * mm});
            skCircle(sketch, "E45.0.5.27", {"center": v(50, 62.44) * mm, "radius": 0.8 * mm});
            skCircle(sketch, "E45.0.5.28", {"center": v(50, 57.44) * mm, "radius": 0.8 * mm});
            skCircle(sketch, "E45.0.5.29", {"center": v(50, 52.44) * mm, "radius": 0.8 * mm});
            skCircle(sketch, "E45.0.6.2", {"center": v(45, 187.44) * mm, "radius": 0.8 * mm});
            skCircle(sketch, "E45.0.6.3", {"center": v(45, 182.44) * mm, "radius": 0.8 * mm});
            skCircle(sketch, "E45.0.6.4", {"center": v(45, 177.44) * mm, "radius": 0.8 * mm});
            skCircle(sketch, "E45.0.6.5", {"center": v(45, 172.44) * mm, "radius": 0.8 * mm});
            skCircle(sketch, "E45.0.6.6", {"center": v(45, 167.44) * mm, "radius": 0.8 * mm});
            skCircle(sketch, "E45.0.6.7", {"center": v(45, 162.44) * mm, "radius": 0.8 * mm});
            skCircle(sketch, "E45.0.6.8", {"center": v(45, 157.44) * mm, "radius": 0.8 * mm});
            skCircle(sketch, "E45.0.6.9", {"center": v(45, 152.44) * mm, "radius": 0.8 * mm});
            skCircle(sketch, "E45.0.6.10", {"center": v(45, 147.44) * mm, "radius": 0.8 * mm});
            skCircle(sketch, "E45.0.6.11", {"center": v(45, 142.44) * mm, "radius": 0.8 * mm});
            skCircle(sketch, "E45.0.6.12", {"center": v(45, 137.44) * mm, "radius": 0.8 * mm});
            skCircle(sketch, "E45.0.6.13", {"center": v(45, 132.44) * mm, "radius": 0.8 * mm});
            skCircle(sketch, "E45.0.6.14", {"center": v(45, 127.44) * mm, "radius": 0.8 * mm});
            skCircle(sketch, "E45.0.6.15", {"center": v(45, 122.44) * mm, "radius": 0.8 * mm});
            skCircle(sketch, "E45.0.6.16", {"center": v(45, 117.44) * mm, "radius": 0.8 * mm});
            skCircle(sketch, "E45.0.6.17", {"center": v(45, 112.44) * mm, "radius": 0.8 * mm});
            skCircle(sketch, "E45.0.6.18", {"center": v(45, 107.44) * mm, "radius": 0.8 * mm});
            skCircle(sketch, "E45.0.6.19", {"center": v(45, 102.44) * mm, "radius": 0.8 * mm});
            skCircle(sketch, "E45.0.6.20", {"center": v(45, 97.44) * mm, "radius": 0.8 * mm});
            skCircle(sketch, "E45.0.6.21", {"center": v(45, 92.44) * mm, "radius": 0.8 * mm});
            skCircle(sketch, "E45.0.6.22", {"center": v(45, 87.44) * mm, "radius": 0.8 * mm});
            skCircle(sketch, "E45.0.6.23", {"center": v(45, 82.44) * mm, "radius": 0.8 * mm});
            skCircle(sketch, "E45.0.6.24", {"center": v(45, 77.44) * mm, "radius": 0.8 * mm});
            skCircle(sketch, "E45.0.6.25", {"center": v(45, 72.44) * mm, "radius": 0.8 * mm});
            skCircle(sketch, "E45.0.6.26", {"center": v(45, 67.44) * mm, "radius": 0.8 * mm});
            skCircle(sketch, "E45.0.6.27", {"center": v(45, 62.44) * mm, "radius": 0.8 * mm});
            skCircle(sketch, "E45.0.6.28", {"center": v(45, 57.44) * mm, "radius": 0.8 * mm});
            skCircle(sketch, "E45.0.6.29", {"center": v(45, 52.44) * mm, "radius": 0.8 * mm});
            skCircle(sketch, "E45.0.7.2", {"center": v(40, 187.44) * mm, "radius": 0.8 * mm});
            skCircle(sketch, "E45.0.7.3", {"center": v(40, 182.44) * mm, "radius": 0.8 * mm});
            skCircle(sketch, "E45.0.7.4", {"center": v(40, 177.44) * mm, "radius": 0.8 * mm});
            skCircle(sketch, "E45.0.7.5", {"center": v(40, 172.44) * mm, "radius": 0.8 * mm});
            skCircle(sketch, "E45.0.7.6", {"center": v(40, 167.44) * mm, "radius": 0.8 * mm});
            skCircle(sketch, "E45.0.7.7", {"center": v(40, 162.44) * mm, "radius": 0.8 * mm});
            skCircle(sketch, "E45.0.7.8", {"center": v(40, 157.44) * mm, "radius": 0.8 * mm});
            skCircle(sketch, "E45.0.7.9", {"center": v(40, 152.44) * mm, "radius": 0.8 * mm});
            skCircle(sketch, "E45.0.7.10", {"center": v(40, 147.44) * mm, "radius": 0.8 * mm});
            skCircle(sketch, "E45.0.7.11", {"center": v(40, 142.44) * mm, "radius": 0.8 * mm});
            skCircle(sketch, "E45.0.7.12", {"center": v(40, 137.44) * mm, "radius": 0.8 * mm});
            skCircle(sketch, "E45.0.7.13", {"center": v(40, 132.44) * mm, "radius": 0.8 * mm});
            skCircle(sketch, "E45.0.7.14", {"center": v(40, 127.44) * mm, "radius": 0.8 * mm});
            skCircle(sketch, "E45.0.7.15", {"center": v(40, 122.44) * mm, "radius": 0.8 * mm});
            skCircle(sketch, "E45.0.7.16", {"center": v(40, 117.44) * mm, "radius": 0.8 * mm});
            skCircle(sketch, "E45.0.7.17", {"center": v(40, 112.44) * mm, "radius": 0.8 * mm});
            skCircle(sketch, "E45.0.7.18", {"center": v(40, 107.44) * mm, "radius": 0.8 * mm});
            skCircle(sketch, "E45.0.7.19", {"center": v(40, 102.44) * mm, "radius": 0.8 * mm});
            skCircle(sketch, "E45.0.7.20", {"center": v(40, 97.44) * mm, "radius": 0.8 * mm});
            skCircle(sketch, "E45.0.7.21", {"center": v(40, 92.44) * mm, "radius": 0.8 * mm});
            skCircle(sketch, "E45.0.7.22", {"center": v(40, 87.44) * mm, "radius": 0.8 * mm});
            skCircle(sketch, "E45.0.7.23", {"center": v(40, 82.44) * mm, "radius": 0.8 * mm});
            skCircle(sketch, "E45.0.7.24", {"center": v(40, 77.44) * mm, "radius": 0.8 * mm});
            skCircle(sketch, "E45.0.7.25", {"center": v(40, 72.44) * mm, "radius": 0.8 * mm});
            skCircle(sketch, "E45.0.7.26", {"center": v(40, 67.44) * mm, "radius": 0.8 * mm});
            skCircle(sketch, "E45.0.7.27", {"center": v(40, 62.44) * mm, "radius": 0.8 * mm});
            skCircle(sketch, "E45.0.7.28", {"center": v(40, 57.44) * mm, "radius": 0.8 * mm});
            skCircle(sketch, "E45.0.7.29", {"center": v(40, 52.44) * mm, "radius": 0.8 * mm});
            skCircle(sketch, "E45.0.8.2", {"center": v(35, 187.44) * mm, "radius": 0.8 * mm});
            skCircle(sketch, "E45.0.8.3", {"center": v(35, 182.44) * mm, "radius": 0.8 * mm});
            skCircle(sketch, "E45.0.8.4", {"center": v(35, 177.44) * mm, "radius": 0.8 * mm});
            skCircle(sketch, "E45.0.8.5", {"center": v(35, 172.44) * mm, "radius": 0.8 * mm});
            skCircle(sketch, "E45.0.8.6", {"center": v(35, 167.44) * mm, "radius": 0.8 * mm});
            skCircle(sketch, "E45.0.8.7", {"center": v(35, 162.44) * mm, "radius": 0.8 * mm});
            skCircle(sketch, "E45.0.8.8", {"center": v(35, 157.44) * mm, "radius": 0.8 * mm});
            skCircle(sketch, "E45.0.8.9", {"center": v(35, 152.44) * mm, "radius": 0.8 * mm});
            skCircle(sketch, "E45.0.8.10", {"center": v(35, 147.44) * mm, "radius": 0.8 * mm});
            skCircle(sketch, "E45.0.8.11", {"center": v(35, 142.44) * mm, "radius": 0.8 * mm});
            skCircle(sketch, "E45.0.8.12", {"center": v(35, 137.44) * mm, "radius": 0.8 * mm});
            skCircle(sketch, "E45.0.8.13", {"center": v(35, 132.44) * mm, "radius": 0.8 * mm});
            skCircle(sketch, "E45.0.8.14", {"center": v(35, 127.44) * mm, "radius": 0.8 * mm});
            skCircle(sketch, "E45.0.8.15", {"center": v(35, 122.44) * mm, "radius": 0.8 * mm});
            skCircle(sketch, "E45.0.8.16", {"center": v(35, 117.44) * mm, "radius": 0.8 * mm});
            skCircle(sketch, "E45.0.8.17", {"center": v(35, 112.44) * mm, "radius": 0.8 * mm});
            skCircle(sketch, "E45.0.8.18", {"center": v(35, 107.44) * mm, "radius": 0.8 * mm});
            skCircle(sketch, "E45.0.8.19", {"center": v(35, 102.44) * mm, "radius": 0.8 * mm});
            skCircle(sketch, "E45.0.8.20", {"center": v(35, 97.44) * mm, "radius": 0.8 * mm});
            skCircle(sketch, "E45.0.8.21", {"center": v(35, 92.44) * mm, "radius": 0.8 * mm});
            skCircle(sketch, "E45.0.8.22", {"center": v(35, 87.44) * mm, "radius": 0.8 * mm});
            skCircle(sketch, "E45.0.8.23", {"center": v(35, 82.44) * mm, "radius": 0.8 * mm});
            skCircle(sketch, "E45.0.8.24", {"center": v(35, 77.44) * mm, "radius": 0.8 * mm});
            skCircle(sketch, "E45.0.8.25", {"center": v(35, 72.44) * mm, "radius": 0.8 * mm});
            skCircle(sketch, "E45.0.8.26", {"center": v(35, 67.44) * mm, "radius": 0.8 * mm});
            skCircle(sketch, "E45.0.8.27", {"center": v(35, 62.44) * mm, "radius": 0.8 * mm});
            skCircle(sketch, "E45.0.8.28", {"center": v(35, 57.44) * mm, "radius": 0.8 * mm});
            skCircle(sketch, "E45.0.8.29", {"center": v(35, 52.44) * mm, "radius": 0.8 * mm});
            skCircle(sketch, "E45.0.9.2", {"center": v(30, 187.44) * mm, "radius": 0.8 * mm});
            skCircle(sketch, "E45.0.9.3", {"center": v(30, 182.44) * mm, "radius": 0.8 * mm});
            skCircle(sketch, "E45.0.9.4", {"center": v(30, 177.44) * mm, "radius": 0.8 * mm});
            skCircle(sketch, "E45.0.9.5", {"center": v(30, 172.44) * mm, "radius": 0.8 * mm});
            skCircle(sketch, "E45.0.9.6", {"center": v(30, 167.44) * mm, "radius": 0.8 * mm});
            skCircle(sketch, "E45.0.9.7", {"center": v(30, 162.44) * mm, "radius": 0.8 * mm});
            skCircle(sketch, "E45.0.9.8", {"center": v(30, 157.44) * mm, "radius": 0.8 * mm});
            skCircle(sketch, "E45.0.9.9", {"center": v(30, 152.44) * mm, "radius": 0.8 * mm});
            skCircle(sketch, "E45.0.9.10", {"center": v(30, 147.44) * mm, "radius": 0.8 * mm});
            skCircle(sketch, "E45.0.9.11", {"center": v(30, 142.44) * mm, "radius": 0.8 * mm});
            skCircle(sketch, "E45.0.9.12", {"center": v(30, 137.44) * mm, "radius": 0.8 * mm});
            skCircle(sketch, "E45.0.9.13", {"center": v(30, 132.44) * mm, "radius": 0.8 * mm});
            skCircle(sketch, "E45.0.9.14", {"center": v(30, 127.44) * mm, "radius": 0.8 * mm});
            skCircle(sketch, "E45.0.9.15", {"center": v(30, 122.44) * mm, "radius": 0.8 * mm});
            skCircle(sketch, "E45.0.9.16", {"center": v(30, 117.44) * mm, "radius": 0.8 * mm});
            skCircle(sketch, "E45.0.9.17", {"center": v(30, 112.44) * mm, "radius": 0.8 * mm});
            skCircle(sketch, "E45.0.9.18", {"center": v(30, 107.44) * mm, "radius": 0.8 * mm});
            skCircle(sketch, "E45.0.9.19", {"center": v(30, 102.44) * mm, "radius": 0.8 * mm});
            skCircle(sketch, "E45.0.9.20", {"center": v(30, 97.44) * mm, "radius": 0.8 * mm});
            skCircle(sketch, "E45.0.9.21", {"center": v(30, 92.44) * mm, "radius": 0.8 * mm});
            skCircle(sketch, "E45.0.9.22", {"center": v(30, 87.44) * mm, "radius": 0.8 * mm});
            skCircle(sketch, "E45.0.9.23", {"center": v(30, 82.44) * mm, "radius": 0.8 * mm});
            skCircle(sketch, "E45.0.9.24", {"center": v(30, 77.44) * mm, "radius": 0.8 * mm});
            skCircle(sketch, "E45.0.9.25", {"center": v(30, 72.44) * mm, "radius": 0.8 * mm});
            skCircle(sketch, "E45.0.9.26", {"center": v(30, 67.44) * mm, "radius": 0.8 * mm});
            skCircle(sketch, "E45.0.9.27", {"center": v(30, 62.44) * mm, "radius": 0.8 * mm});
            skCircle(sketch, "E45.0.9.28", {"center": v(30, 57.44) * mm, "radius": 0.8 * mm});
            skCircle(sketch, "E45.0.9.29", {"center": v(30, 52.44) * mm, "radius": 0.8 * mm});
            skCircle(sketch, "E45.0.10.2", {"center": v(25, 187.44) * mm, "radius": 0.8 * mm});
            skCircle(sketch, "E45.0.10.3", {"center": v(25, 182.44) * mm, "radius": 0.8 * mm});
            skCircle(sketch, "E45.0.10.4", {"center": v(25, 177.44) * mm, "radius": 0.8 * mm});
            skCircle(sketch, "E45.0.10.5", {"center": v(25, 172.44) * mm, "radius": 0.8 * mm});
            skCircle(sketch, "E45.0.10.6", {"center": v(25, 167.44) * mm, "radius": 0.8 * mm});
            skCircle(sketch, "E45.0.10.7", {"center": v(25, 162.44) * mm, "radius": 0.8 * mm});
            skCircle(sketch, "E45.0.10.8", {"center": v(25, 157.44) * mm, "radius": 0.8 * mm});
            skCircle(sketch, "E45.0.10.9", {"center": v(25, 152.44) * mm, "radius": 0.8 * mm});
            skCircle(sketch, "E45.0.10.10", {"center": v(25, 147.44) * mm, "radius": 0.8 * mm});
            skCircle(sketch, "E45.0.10.11", {"center": v(25, 142.44) * mm, "radius": 0.8 * mm});
            skCircle(sketch, "E45.0.10.12", {"center": v(25, 137.44) * mm, "radius": 0.8 * mm});
            skCircle(sketch, "E45.0.10.13", {"center": v(25, 132.44) * mm, "radius": 0.8 * mm});
            skCircle(sketch, "E45.0.10.14", {"center": v(25, 127.44) * mm, "radius": 0.8 * mm});
            skCircle(sketch, "E45.0.10.15", {"center": v(25, 122.44) * mm, "radius": 0.8 * mm});
            skCircle(sketch, "E45.0.10.16", {"center": v(25, 117.44) * mm, "radius": 0.8 * mm});
            skCircle(sketch, "E45.0.10.17", {"center": v(25, 112.44) * mm, "radius": 0.8 * mm});
            skCircle(sketch, "E45.0.10.18", {"center": v(25, 107.44) * mm, "radius": 0.8 * mm});
            skCircle(sketch, "E45.0.10.19", {"center": v(25, 102.44) * mm, "radius": 0.8 * mm});
            skCircle(sketch, "E45.0.10.20", {"center": v(25, 97.44) * mm, "radius": 0.8 * mm});
            skCircle(sketch, "E45.0.10.21", {"center": v(25, 92.44) * mm, "radius": 0.8 * mm});
            skCircle(sketch, "E45.0.10.22", {"center": v(25, 87.44) * mm, "radius": 0.8 * mm});
            skCircle(sketch, "E45.0.10.23", {"center": v(25, 82.44) * mm, "radius": 0.8 * mm});
            skCircle(sketch, "E45.0.10.24", {"center": v(25, 77.44) * mm, "radius": 0.8 * mm});
            skCircle(sketch, "E45.0.10.25", {"center": v(25, 72.44) * mm, "radius": 0.8 * mm});
            skCircle(sketch, "E45.0.10.26", {"center": v(25, 67.44) * mm, "radius": 0.8 * mm});
            skCircle(sketch, "E45.0.10.27", {"center": v(25, 62.44) * mm, "radius": 0.8 * mm});
            skCircle(sketch, "E45.0.10.28", {"center": v(25, 57.44) * mm, "radius": 0.8 * mm});
            skCircle(sketch, "E45.0.10.29", {"center": v(25, 52.44) * mm, "radius": 0.8 * mm});
            skCircle(sketch, "E45.0.11.2", {"center": v(20, 187.44) * mm, "radius": 0.8 * mm});
            skCircle(sketch, "E45.0.11.3", {"center": v(20, 182.44) * mm, "radius": 0.8 * mm});
            skCircle(sketch, "E45.0.11.4", {"center": v(20, 177.44) * mm, "radius": 0.8 * mm});
            skCircle(sketch, "E45.0.11.5", {"center": v(20, 172.44) * mm, "radius": 0.8 * mm});
            skCircle(sketch, "E45.0.11.6", {"center": v(20, 167.44) * mm, "radius": 0.8 * mm});
            skCircle(sketch, "E45.0.11.7", {"center": v(20, 162.44) * mm, "radius": 0.8 * mm});
            skCircle(sketch, "E45.0.11.8", {"center": v(20, 157.44) * mm, "radius": 0.8 * mm});
            skCircle(sketch, "E45.0.11.9", {"center": v(20, 152.44) * mm, "radius": 0.8 * mm});
            skCircle(sketch, "E45.0.11.10", {"center": v(20, 147.44) * mm, "radius": 0.8 * mm});
            skCircle(sketch, "E45.0.11.11", {"center": v(20, 142.44) * mm, "radius": 0.8 * mm});
            skCircle(sketch, "E45.0.11.12", {"center": v(20, 137.44) * mm, "radius": 0.8 * mm});
            skCircle(sketch, "E45.0.11.13", {"center": v(20, 132.44) * mm, "radius": 0.8 * mm});
            skCircle(sketch, "E45.0.11.14", {"center": v(20, 127.44) * mm, "radius": 0.8 * mm});
            skCircle(sketch, "E45.0.11.15", {"center": v(20, 122.44) * mm, "radius": 0.8 * mm});
            skCircle(sketch, "E45.0.11.16", {"center": v(20, 117.44) * mm, "radius": 0.8 * mm});
            skCircle(sketch, "E45.0.11.17", {"center": v(20, 112.44) * mm, "radius": 0.8 * mm});
            skCircle(sketch, "E45.0.11.18", {"center": v(20, 107.44) * mm, "radius": 0.8 * mm});
            skCircle(sketch, "E45.0.11.19", {"center": v(20, 102.44) * mm, "radius": 0.8 * mm});
            skCircle(sketch, "E45.0.11.20", {"center": v(20, 97.44) * mm, "radius": 0.8 * mm});
            skCircle(sketch, "E45.0.11.21", {"center": v(20, 92.44) * mm, "radius": 0.8 * mm});
            skCircle(sketch, "E45.0.11.22", {"center": v(20, 87.44) * mm, "radius": 0.8 * mm});
            skCircle(sketch, "E45.0.11.23", {"center": v(20, 82.44) * mm, "radius": 0.8 * mm});
            skCircle(sketch, "E45.0.11.24", {"center": v(20, 77.44) * mm, "radius": 0.8 * mm});
            skCircle(sketch, "E45.0.11.25", {"center": v(20, 72.44) * mm, "radius": 0.8 * mm});
            skCircle(sketch, "E45.0.11.26", {"center": v(20, 67.44) * mm, "radius": 0.8 * mm});
            skCircle(sketch, "E45.0.11.27", {"center": v(20, 62.44) * mm, "radius": 0.8 * mm});
            skCircle(sketch, "E45.0.11.28", {"center": v(20, 57.44) * mm, "radius": 0.8 * mm});
            skCircle(sketch, "E45.0.11.29", {"center": v(20, 52.44) * mm, "radius": 0.8 * mm});
            skCircle(sketch, "E45.0.12.2", {"center": v(15, 187.44) * mm, "radius": 0.8 * mm});
            skCircle(sketch, "E45.0.12.3", {"center": v(15, 182.44) * mm, "radius": 0.8 * mm});
            skCircle(sketch, "E45.0.12.4", {"center": v(15, 177.44) * mm, "radius": 0.8 * mm});
            skCircle(sketch, "E45.0.12.5", {"center": v(15, 172.44) * mm, "radius": 0.8 * mm});
            skCircle(sketch, "E45.0.12.6", {"center": v(15, 167.44) * mm, "radius": 0.8 * mm});
            skCircle(sketch, "E45.0.12.7", {"center": v(15, 162.44) * mm, "radius": 0.8 * mm});
            skCircle(sketch, "E45.0.12.8", {"center": v(15, 157.44) * mm, "radius": 0.8 * mm});
            skCircle(sketch, "E45.0.12.9", {"center": v(15, 152.44) * mm, "radius": 0.8 * mm});
            skCircle(sketch, "E45.0.12.10", {"center": v(15, 147.44) * mm, "radius": 0.8 * mm});
            skCircle(sketch, "E45.0.12.11", {"center": v(15, 142.44) * mm, "radius": 0.8 * mm});
            skCircle(sketch, "E45.0.12.12", {"center": v(15, 137.44) * mm, "radius": 0.8 * mm});
            skCircle(sketch, "E45.0.12.13", {"center": v(15, 132.44) * mm, "radius": 0.8 * mm});
            skCircle(sketch, "E45.0.12.14", {"center": v(15, 127.44) * mm, "radius": 0.8 * mm});
            skCircle(sketch, "E45.0.12.15", {"center": v(15, 122.44) * mm, "radius": 0.8 * mm});
            skCircle(sketch, "E45.0.12.16", {"center": v(15, 117.44) * mm, "radius": 0.8 * mm});
            skCircle(sketch, "E45.0.12.17", {"center": v(15, 112.44) * mm, "radius": 0.8 * mm});
            skCircle(sketch, "E45.0.12.18", {"center": v(15, 107.44) * mm, "radius": 0.8 * mm});
            skCircle(sketch, "E45.0.12.19", {"center": v(15, 102.44) * mm, "radius": 0.8 * mm});
            skCircle(sketch, "E45.0.12.20", {"center": v(15, 97.44) * mm, "radius": 0.8 * mm});
            skCircle(sketch, "E45.0.12.21", {"center": v(15, 92.44) * mm, "radius": 0.8 * mm});
            skCircle(sketch, "E45.0.12.22", {"center": v(15, 87.44) * mm, "radius": 0.8 * mm});
            skCircle(sketch, "E45.0.12.23", {"center": v(15, 82.44) * mm, "radius": 0.8 * mm});
            skCircle(sketch, "E45.0.12.24", {"center": v(15, 77.44) * mm, "radius": 0.8 * mm});
            skCircle(sketch, "E45.0.12.25", {"center": v(15, 72.44) * mm, "radius": 0.8 * mm});
            skCircle(sketch, "E45.0.12.26", {"center": v(15, 67.44) * mm, "radius": 0.8 * mm});
            skCircle(sketch, "E45.0.12.27", {"center": v(15, 62.44) * mm, "radius": 0.8 * mm});
            skCircle(sketch, "E45.0.12.28", {"center": v(15, 57.44) * mm, "radius": 0.8 * mm});
            skCircle(sketch, "E45.0.12.29", {"center": v(15, 52.44) * mm, "radius": 0.8 * mm});
            skCircle(sketch, "E45.0.13.2", {"center": v(10, 187.44) * mm, "radius": 0.8 * mm});
            skCircle(sketch, "E45.0.13.3", {"center": v(10, 182.44) * mm, "radius": 0.8 * mm});
            skCircle(sketch, "E45.0.13.4", {"center": v(10, 177.44) * mm, "radius": 0.8 * mm});
            skCircle(sketch, "E45.0.13.5", {"center": v(10, 172.44) * mm, "radius": 0.8 * mm});
            skCircle(sketch, "E45.0.13.6", {"center": v(10, 167.44) * mm, "radius": 0.8 * mm});
            skCircle(sketch, "E45.0.13.7", {"center": v(10, 162.44) * mm, "radius": 0.8 * mm});
            skCircle(sketch, "E45.0.13.8", {"center": v(10, 157.44) * mm, "radius": 0.8 * mm});
            skCircle(sketch, "E45.0.13.9", {"center": v(10, 152.44) * mm, "radius": 0.8 * mm});
            skCircle(sketch, "E45.0.13.10", {"center": v(10, 147.44) * mm, "radius": 0.8 * mm});
            skCircle(sketch, "E45.0.13.11", {"center": v(10, 142.44) * mm, "radius": 0.8 * mm});
            skCircle(sketch, "E45.0.13.12", {"center": v(10, 137.44) * mm, "radius": 0.8 * mm});
            skCircle(sketch, "E45.0.13.13", {"center": v(10, 132.44) * mm, "radius": 0.8 * mm});
            skCircle(sketch, "E45.0.13.14", {"center": v(10, 127.44) * mm, "radius": 0.8 * mm});
            skCircle(sketch, "E45.0.13.15", {"center": v(10, 122.44) * mm, "radius": 0.8 * mm});
            skCircle(sketch, "E45.0.13.16", {"center": v(10, 117.44) * mm, "radius": 0.8 * mm});
            skCircle(sketch, "E45.0.13.17", {"center": v(10, 112.44) * mm, "radius": 0.8 * mm});
            skCircle(sketch, "E45.0.13.18", {"center": v(10, 107.44) * mm, "radius": 0.8 * mm});
            skCircle(sketch, "E45.0.13.19", {"center": v(10, 102.44) * mm, "radius": 0.8 * mm});
            skCircle(sketch, "E45.0.13.20", {"center": v(10, 97.44) * mm, "radius": 0.8 * mm});
            skCircle(sketch, "E45.0.13.21", {"center": v(10, 92.44) * mm, "radius": 0.8 * mm});
            skCircle(sketch, "E45.0.13.22", {"center": v(10, 87.44) * mm, "radius": 0.8 * mm});
            skCircle(sketch, "E45.0.13.23", {"center": v(10, 82.44) * mm, "radius": 0.8 * mm});
            skCircle(sketch, "E45.0.13.24", {"center": v(10, 77.44) * mm, "radius": 0.8 * mm});
            skCircle(sketch, "E45.0.13.25", {"center": v(10, 72.44) * mm, "radius": 0.8 * mm});
            skCircle(sketch, "E45.0.13.26", {"center": v(10, 67.44) * mm, "radius": 0.8 * mm});
            skCircle(sketch, "E45.0.13.27", {"center": v(10, 62.44) * mm, "radius": 0.8 * mm});
            skCircle(sketch, "E45.0.13.28", {"center": v(10, 57.44) * mm, "radius": 0.8 * mm});
            skCircle(sketch, "E45.0.13.29", {"center": v(10, 52.44) * mm, "radius": 0.8 * mm});
            skCircle(sketch, "E45.0.14.2", {"center": v(5, 187.44) * mm, "radius": 0.8 * mm});
            skCircle(sketch, "E45.0.14.3", {"center": v(5, 182.44) * mm, "radius": 0.8 * mm});
            skCircle(sketch, "E45.0.14.4", {"center": v(5, 177.44) * mm, "radius": 0.8 * mm});
            skCircle(sketch, "E45.0.14.5", {"center": v(5, 172.44) * mm, "radius": 0.8 * mm});
            skCircle(sketch, "E45.0.14.6", {"center": v(5, 167.44) * mm, "radius": 0.8 * mm});
            skCircle(sketch, "E45.0.14.7", {"center": v(5, 162.44) * mm, "radius": 0.8 * mm});
            skCircle(sketch, "E45.0.14.8", {"center": v(5, 157.44) * mm, "radius": 0.8 * mm});
            skCircle(sketch, "E45.0.14.9", {"center": v(5, 152.44) * mm, "radius": 0.8 * mm});
            skCircle(sketch, "E45.0.14.10", {"center": v(5, 147.44) * mm, "radius": 0.8 * mm});
            skCircle(sketch, "E45.0.14.11", {"center": v(5, 142.44) * mm, "radius": 0.8 * mm});
            skCircle(sketch, "E45.0.14.12", {"center": v(5, 137.44) * mm, "radius": 0.8 * mm});
            skCircle(sketch, "E45.0.14.13", {"center": v(5, 132.44) * mm, "radius": 0.8 * mm});
            skCircle(sketch, "E45.0.14.14", {"center": v(5, 127.44) * mm, "radius": 0.8 * mm});
            skCircle(sketch, "E45.0.14.15", {"center": v(5, 122.44) * mm, "radius": 0.8 * mm});
            skCircle(sketch, "E45.0.14.16", {"center": v(5, 117.44) * mm, "radius": 0.8 * mm});
            skCircle(sketch, "E45.0.14.17", {"center": v(5, 112.44) * mm, "radius": 0.8 * mm});
            skCircle(sketch, "E45.0.14.18", {"center": v(5, 107.44) * mm, "radius": 0.8 * mm});
            skCircle(sketch, "E45.0.14.19", {"center": v(5, 102.44) * mm, "radius": 0.8 * mm});
            skCircle(sketch, "E45.0.14.20", {"center": v(5, 97.44) * mm, "radius": 0.8 * mm});
            skCircle(sketch, "E45.0.14.21", {"center": v(5, 92.44) * mm, "radius": 0.8 * mm});
            skCircle(sketch, "E45.0.14.22", {"center": v(5, 87.44) * mm, "radius": 0.8 * mm});
            skCircle(sketch, "E45.0.14.23", {"center": v(5, 82.44) * mm, "radius": 0.8 * mm});
            skCircle(sketch, "E45.0.14.24", {"center": v(5, 77.44) * mm, "radius": 0.8 * mm});
            skCircle(sketch, "E45.0.14.25", {"center": v(5, 72.44) * mm, "radius": 0.8 * mm});
            skCircle(sketch, "E45.0.14.26", {"center": v(5, 67.44) * mm, "radius": 0.8 * mm});
            skCircle(sketch, "E45.0.14.27", {"center": v(5, 62.44) * mm, "radius": 0.8 * mm});
            skCircle(sketch, "E45.0.14.28", {"center": v(5, 57.44) * mm, "radius": 0.8 * mm});
            skCircle(sketch, "E45.0.14.29", {"center": v(5, 52.44) * mm, "radius": 0.8 * mm});
            skCircle(sketch, "E45.0.15.2", {"center": v(0, 187.44) * mm, "radius": 0.8 * mm});
            skCircle(sketch, "E45.0.15.3", {"center": v(0, 182.44) * mm, "radius": 0.8 * mm});
            skCircle(sketch, "E45.0.15.4", {"center": v(0, 177.44) * mm, "radius": 0.8 * mm});
            skCircle(sketch, "E45.0.15.5", {"center": v(0, 172.44) * mm, "radius": 0.8 * mm});
            skCircle(sketch, "E45.0.15.6", {"center": v(0, 167.44) * mm, "radius": 0.8 * mm});
            skCircle(sketch, "E45.0.15.7", {"center": v(0, 162.44) * mm, "radius": 0.8 * mm});
            skCircle(sketch, "E45.0.15.8", {"center": v(0, 157.44) * mm, "radius": 0.8 * mm});
            skCircle(sketch, "E45.0.15.9", {"center": v(0, 152.44) * mm, "radius": 0.8 * mm});
            skCircle(sketch, "E45.0.15.10", {"center": v(0, 147.44) * mm, "radius": 0.8 * mm});
            skCircle(sketch, "E45.0.15.11", {"center": v(0, 142.44) * mm, "radius": 0.8 * mm});
            skCircle(sketch, "E45.0.15.12", {"center": v(0, 137.44) * mm, "radius": 0.8 * mm});
            skCircle(sketch, "E45.0.15.13", {"center": v(0, 132.44) * mm, "radius": 0.8 * mm});
            skCircle(sketch, "E45.0.15.14", {"center": v(0, 127.44) * mm, "radius": 0.8 * mm});
            skCircle(sketch, "E45.0.15.15", {"center": v(0, 122.44) * mm, "radius": 0.8 * mm});
            skCircle(sketch, "E45.0.15.16", {"center": v(0, 117.44) * mm, "radius": 0.8 * mm});
            skCircle(sketch, "E45.0.15.17", {"center": v(0, 112.44) * mm, "radius": 0.8 * mm});
            skCircle(sketch, "E45.0.15.18", {"center": v(0, 107.44) * mm, "radius": 0.8 * mm});
            skCircle(sketch, "E45.0.15.19", {"center": v(0, 102.44) * mm, "radius": 0.8 * mm});
            skCircle(sketch, "E45.0.15.20", {"center": v(0, 97.44) * mm, "radius": 0.8 * mm});
            skCircle(sketch, "E45.0.15.21", {"center": v(0, 92.44) * mm, "radius": 0.8 * mm});
            skCircle(sketch, "E45.0.15.22", {"center": v(0, 87.44) * mm, "radius": 0.8 * mm});
            skCircle(sketch, "E45.0.15.23", {"center": v(0, 82.44) * mm, "radius": 0.8 * mm});
            skCircle(sketch, "E45.0.15.24", {"center": v(0, 77.44) * mm, "radius": 0.8 * mm});
            skCircle(sketch, "E45.0.15.25", {"center": v(0, 72.44) * mm, "radius": 0.8 * mm});
            skCircle(sketch, "E45.0.15.26", {"center": v(0, 67.44) * mm, "radius": 0.8 * mm});
            skCircle(sketch, "E45.0.15.27", {"center": v(0, 62.44) * mm, "radius": 0.8 * mm});
            skCircle(sketch, "E45.0.15.28", {"center": v(0, 57.44) * mm, "radius": 0.8 * mm});
            skCircle(sketch, "E45.0.15.29", {"center": v(0, 52.44) * mm, "radius": 0.8 * mm});
            skCircle(sketch, "E45.0.16.2", {"center": v(-5, 187.44) * mm, "radius": 0.8 * mm});
            skCircle(sketch, "E45.0.16.3", {"center": v(-5, 182.44) * mm, "radius": 0.8 * mm});
            skCircle(sketch, "E45.0.16.4", {"center": v(-5, 177.44) * mm, "radius": 0.8 * mm});
            skCircle(sketch, "E45.0.16.5", {"center": v(-5, 172.44) * mm, "radius": 0.8 * mm});
            skCircle(sketch, "E45.0.16.6", {"center": v(-5, 167.44) * mm, "radius": 0.8 * mm});
            skCircle(sketch, "E45.0.16.7", {"center": v(-5, 162.44) * mm, "radius": 0.8 * mm});
            skCircle(sketch, "E45.0.16.8", {"center": v(-5, 157.44) * mm, "radius": 0.8 * mm});
            skCircle(sketch, "E45.0.16.9", {"center": v(-5, 152.44) * mm, "radius": 0.8 * mm});
            skCircle(sketch, "E45.0.16.10", {"center": v(-5, 147.44) * mm, "radius": 0.8 * mm});
            skCircle(sketch, "E45.0.16.11", {"center": v(-5, 142.44) * mm, "radius": 0.8 * mm});
            skCircle(sketch, "E45.0.16.12", {"center": v(-5, 137.44) * mm, "radius": 0.8 * mm});
            skCircle(sketch, "E45.0.16.13", {"center": v(-5, 132.44) * mm, "radius": 0.8 * mm});
            skCircle(sketch, "E45.0.16.14", {"center": v(-5, 127.44) * mm, "radius": 0.8 * mm});
            skCircle(sketch, "E45.0.16.15", {"center": v(-5, 122.44) * mm, "radius": 0.8 * mm});
            skCircle(sketch, "E45.0.16.16", {"center": v(-5, 117.44) * mm, "radius": 0.8 * mm});
            skCircle(sketch, "E45.0.16.17", {"center": v(-5, 112.44) * mm, "radius": 0.8 * mm});
            skCircle(sketch, "E45.0.16.18", {"center": v(-5, 107.44) * mm, "radius": 0.8 * mm});
            skCircle(sketch, "E45.0.16.19", {"center": v(-5, 102.44) * mm, "radius": 0.8 * mm});
            skCircle(sketch, "E45.0.16.20", {"center": v(-5, 97.44) * mm, "radius": 0.8 * mm});
            skCircle(sketch, "E45.0.16.21", {"center": v(-5, 92.44) * mm, "radius": 0.8 * mm});
            skCircle(sketch, "E45.0.16.22", {"center": v(-5, 87.44) * mm, "radius": 0.8 * mm});
            skCircle(sketch, "E45.0.16.23", {"center": v(-5, 82.44) * mm, "radius": 0.8 * mm});
            skCircle(sketch, "E45.0.16.24", {"center": v(-5, 77.44) * mm, "radius": 0.8 * mm});
            skCircle(sketch, "E45.0.16.25", {"center": v(-5, 72.44) * mm, "radius": 0.8 * mm});
            skCircle(sketch, "E45.0.16.26", {"center": v(-5, 67.44) * mm, "radius": 0.8 * mm});
            skCircle(sketch, "E45.0.16.27", {"center": v(-5, 62.44) * mm, "radius": 0.8 * mm});
            skCircle(sketch, "E45.0.16.28", {"center": v(-5, 57.44) * mm, "radius": 0.8 * mm});
            skCircle(sketch, "E45.0.16.29", {"center": v(-5, 52.44) * mm, "radius": 0.8 * mm});
            skCircle(sketch, "E45.0.17.2", {"center": v(-10, 187.44) * mm, "radius": 0.8 * mm});
            skCircle(sketch, "E45.0.17.3", {"center": v(-10, 182.44) * mm, "radius": 0.8 * mm});
            skCircle(sketch, "E45.0.17.4", {"center": v(-10, 177.44) * mm, "radius": 0.8 * mm});
            skCircle(sketch, "E45.0.17.5", {"center": v(-10, 172.44) * mm, "radius": 0.8 * mm});
            skCircle(sketch, "E45.0.17.6", {"center": v(-10, 167.44) * mm, "radius": 0.8 * mm});
            skCircle(sketch, "E45.0.17.7", {"center": v(-10, 162.44) * mm, "radius": 0.8 * mm});
            skCircle(sketch, "E45.0.17.8", {"center": v(-10, 157.44) * mm, "radius": 0.8 * mm});
            skCircle(sketch, "E45.0.17.9", {"center": v(-10, 152.44) * mm, "radius": 0.8 * mm});
            skCircle(sketch, "E45.0.17.10", {"center": v(-10, 147.44) * mm, "radius": 0.8 * mm});
            skCircle(sketch, "E45.0.17.11", {"center": v(-10, 142.44) * mm, "radius": 0.8 * mm});
            skCircle(sketch, "E45.0.17.12", {"center": v(-10, 137.44) * mm, "radius": 0.8 * mm});
            skCircle(sketch, "E45.0.17.13", {"center": v(-10, 132.44) * mm, "radius": 0.8 * mm});
            skCircle(sketch, "E45.0.17.14", {"center": v(-10, 127.44) * mm, "radius": 0.8 * mm});
            skCircle(sketch, "E45.0.17.15", {"center": v(-10, 122.44) * mm, "radius": 0.8 * mm});
            skCircle(sketch, "E45.0.17.16", {"center": v(-10, 117.44) * mm, "radius": 0.8 * mm});
            skCircle(sketch, "E45.0.17.17", {"center": v(-10, 112.44) * mm, "radius": 0.8 * mm});
            skCircle(sketch, "E45.0.17.18", {"center": v(-10, 107.44) * mm, "radius": 0.8 * mm});
            skCircle(sketch, "E45.0.17.19", {"center": v(-10, 102.44) * mm, "radius": 0.8 * mm});
            skCircle(sketch, "E45.0.17.20", {"center": v(-10, 97.44) * mm, "radius": 0.8 * mm});
            skCircle(sketch, "E45.0.17.21", {"center": v(-10, 92.44) * mm, "radius": 0.8 * mm});
            skCircle(sketch, "E45.0.17.22", {"center": v(-10, 87.44) * mm, "radius": 0.8 * mm});
            skCircle(sketch, "E45.0.17.23", {"center": v(-10, 82.44) * mm, "radius": 0.8 * mm});
            skCircle(sketch, "E45.0.17.24", {"center": v(-10, 77.44) * mm, "radius": 0.8 * mm});
            skCircle(sketch, "E45.0.17.25", {"center": v(-10, 72.44) * mm, "radius": 0.8 * mm});
            skCircle(sketch, "E45.0.17.26", {"center": v(-10, 67.44) * mm, "radius": 0.8 * mm});
            skCircle(sketch, "E45.0.17.27", {"center": v(-10, 62.44) * mm, "radius": 0.8 * mm});
            skCircle(sketch, "E45.0.17.28", {"center": v(-10, 57.44) * mm, "radius": 0.8 * mm});
            skCircle(sketch, "E45.0.17.29", {"center": v(-10, 52.44) * mm, "radius": 0.8 * mm});
            skCircle(sketch, "E45.0.18.2", {"center": v(-15, 187.44) * mm, "radius": 0.8 * mm});
            skCircle(sketch, "E45.0.18.3", {"center": v(-15, 182.44) * mm, "radius": 0.8 * mm});
            skCircle(sketch, "E45.0.18.4", {"center": v(-15, 177.44) * mm, "radius": 0.8 * mm});
            skCircle(sketch, "E45.0.18.5", {"center": v(-15, 172.44) * mm, "radius": 0.8 * mm});
            skCircle(sketch, "E45.0.18.6", {"center": v(-15, 167.44) * mm, "radius": 0.8 * mm});
            skCircle(sketch, "E45.0.18.7", {"center": v(-15, 162.44) * mm, "radius": 0.8 * mm});
            skCircle(sketch, "E45.0.18.8", {"center": v(-15, 157.44) * mm, "radius": 0.8 * mm});
            skCircle(sketch, "E45.0.18.9", {"center": v(-15, 152.44) * mm, "radius": 0.8 * mm});
            skCircle(sketch, "E45.0.18.10", {"center": v(-15, 147.44) * mm, "radius": 0.8 * mm});
            skCircle(sketch, "E45.0.18.11", {"center": v(-15, 142.44) * mm, "radius": 0.8 * mm});
            skCircle(sketch, "E45.0.18.12", {"center": v(-15, 137.44) * mm, "radius": 0.8 * mm});
            skCircle(sketch, "E45.0.18.13", {"center": v(-15, 132.44) * mm, "radius": 0.8 * mm});
            skCircle(sketch, "E45.0.18.14", {"center": v(-15, 127.44) * mm, "radius": 0.8 * mm});
            skCircle(sketch, "E45.0.18.15", {"center": v(-15, 122.44) * mm, "radius": 0.8 * mm});
            skCircle(sketch, "E45.0.18.16", {"center": v(-15, 117.44) * mm, "radius": 0.8 * mm});
            skCircle(sketch, "E45.0.18.17", {"center": v(-15, 112.44) * mm, "radius": 0.8 * mm});
            skCircle(sketch, "E45.0.18.18", {"center": v(-15, 107.44) * mm, "radius": 0.8 * mm});
            skCircle(sketch, "E45.0.18.19", {"center": v(-15, 102.44) * mm, "radius": 0.8 * mm});
            skCircle(sketch, "E45.0.18.20", {"center": v(-15, 97.44) * mm, "radius": 0.8 * mm});
            skCircle(sketch, "E45.0.18.21", {"center": v(-15, 92.44) * mm, "radius": 0.8 * mm});
            skCircle(sketch, "E45.0.18.22", {"center": v(-15, 87.44) * mm, "radius": 0.8 * mm});
            skCircle(sketch, "E45.0.18.23", {"center": v(-15, 82.44) * mm, "radius": 0.8 * mm});
            skCircle(sketch, "E45.0.18.24", {"center": v(-15, 77.44) * mm, "radius": 0.8 * mm});
            skCircle(sketch, "E45.0.18.25", {"center": v(-15, 72.44) * mm, "radius": 0.8 * mm});
            skCircle(sketch, "E45.0.18.26", {"center": v(-15, 67.44) * mm, "radius": 0.8 * mm});
            skCircle(sketch, "E45.0.18.27", {"center": v(-15, 62.44) * mm, "radius": 0.8 * mm});
            skCircle(sketch, "E45.0.18.28", {"center": v(-15, 57.44) * mm, "radius": 0.8 * mm});
            skCircle(sketch, "E45.0.18.29", {"center": v(-15, 52.44) * mm, "radius": 0.8 * mm});
            skCircle(sketch, "E45.0.19.2", {"center": v(-20, 187.44) * mm, "radius": 0.8 * mm});
            skCircle(sketch, "E45.0.19.3", {"center": v(-20, 182.44) * mm, "radius": 0.8 * mm});
            skCircle(sketch, "E45.0.19.4", {"center": v(-20, 177.44) * mm, "radius": 0.8 * mm});
            skCircle(sketch, "E45.0.19.5", {"center": v(-20, 172.44) * mm, "radius": 0.8 * mm});
            skCircle(sketch, "E45.0.19.6", {"center": v(-20, 167.44) * mm, "radius": 0.8 * mm});
            skCircle(sketch, "E45.0.19.7", {"center": v(-20, 162.44) * mm, "radius": 0.8 * mm});
            skCircle(sketch, "E45.0.19.8", {"center": v(-20, 157.44) * mm, "radius": 0.8 * mm});
            skCircle(sketch, "E45.0.19.9", {"center": v(-20, 152.44) * mm, "radius": 0.8 * mm});
            skCircle(sketch, "E45.0.19.10", {"center": v(-20, 147.44) * mm, "radius": 0.8 * mm});
            skCircle(sketch, "E45.0.19.11", {"center": v(-20, 142.44) * mm, "radius": 0.8 * mm});
            skCircle(sketch, "E45.0.19.12", {"center": v(-20, 137.44) * mm, "radius": 0.8 * mm});
            skCircle(sketch, "E45.0.19.13", {"center": v(-20, 132.44) * mm, "radius": 0.8 * mm});
            skCircle(sketch, "E45.0.19.14", {"center": v(-20, 127.44) * mm, "radius": 0.8 * mm});
            skCircle(sketch, "E45.0.19.15", {"center": v(-20, 122.44) * mm, "radius": 0.8 * mm});
            skCircle(sketch, "E45.0.19.16", {"center": v(-20, 117.44) * mm, "radius": 0.8 * mm});
            skCircle(sketch, "E45.0.19.17", {"center": v(-20, 112.44) * mm, "radius": 0.8 * mm});
            skCircle(sketch, "E45.0.19.18", {"center": v(-20, 107.44) * mm, "radius": 0.8 * mm});
            skCircle(sketch, "E45.0.19.19", {"center": v(-20, 102.44) * mm, "radius": 0.8 * mm});
            skCircle(sketch, "E45.0.19.20", {"center": v(-20, 97.44) * mm, "radius": 0.8 * mm});
            skCircle(sketch, "E45.0.19.21", {"center": v(-20, 92.44) * mm, "radius": 0.8 * mm});
            skCircle(sketch, "E45.0.19.22", {"center": v(-20, 87.44) * mm, "radius": 0.8 * mm});
            skCircle(sketch, "E45.0.19.23", {"center": v(-20, 82.44) * mm, "radius": 0.8 * mm});
            skCircle(sketch, "E45.0.19.24", {"center": v(-20, 77.44) * mm, "radius": 0.8 * mm});
            skCircle(sketch, "E45.0.19.25", {"center": v(-20, 72.44) * mm, "radius": 0.8 * mm});
            skCircle(sketch, "E45.0.19.26", {"center": v(-20, 67.44) * mm, "radius": 0.8 * mm});
            skCircle(sketch, "E45.0.19.27", {"center": v(-20, 62.44) * mm, "radius": 0.8 * mm});
            skCircle(sketch, "E45.0.19.28", {"center": v(-20, 57.44) * mm, "radius": 0.8 * mm});
            skCircle(sketch, "E45.0.19.29", {"center": v(-20, 52.44) * mm, "radius": 0.8 * mm});
            skCircle(sketch, "E45.0.20.2", {"center": v(-25, 187.44) * mm, "radius": 0.8 * mm});
            skCircle(sketch, "E45.0.20.3", {"center": v(-25, 182.44) * mm, "radius": 0.8 * mm});
            skCircle(sketch, "E45.0.20.4", {"center": v(-25, 177.44) * mm, "radius": 0.8 * mm});
            skCircle(sketch, "E45.0.20.5", {"center": v(-25, 172.44) * mm, "radius": 0.8 * mm});
            skCircle(sketch, "E45.0.20.6", {"center": v(-25, 167.44) * mm, "radius": 0.8 * mm});
            skCircle(sketch, "E45.0.20.7", {"center": v(-25, 162.44) * mm, "radius": 0.8 * mm});
            skCircle(sketch, "E45.0.20.8", {"center": v(-25, 157.44) * mm, "radius": 0.8 * mm});
            skCircle(sketch, "E45.0.20.9", {"center": v(-25, 152.44) * mm, "radius": 0.8 * mm});
            skCircle(sketch, "E45.0.20.10", {"center": v(-25, 147.44) * mm, "radius": 0.8 * mm});
            skCircle(sketch, "E45.0.20.11", {"center": v(-25, 142.44) * mm, "radius": 0.8 * mm});
            skCircle(sketch, "E45.0.20.12", {"center": v(-25, 137.44) * mm, "radius": 0.8 * mm});
            skCircle(sketch, "E45.0.20.13", {"center": v(-25, 132.44) * mm, "radius": 0.8 * mm});
            skCircle(sketch, "E45.0.20.14", {"center": v(-25, 127.44) * mm, "radius": 0.8 * mm});
            skCircle(sketch, "E45.0.20.15", {"center": v(-25, 122.44) * mm, "radius": 0.8 * mm});
            skCircle(sketch, "E45.0.20.16", {"center": v(-25, 117.44) * mm, "radius": 0.8 * mm});
            skCircle(sketch, "E45.0.20.17", {"center": v(-25, 112.44) * mm, "radius": 0.8 * mm});
            skCircle(sketch, "E45.0.20.18", {"center": v(-25, 107.44) * mm, "radius": 0.8 * mm});
            skCircle(sketch, "E45.0.20.19", {"center": v(-25, 102.44) * mm, "radius": 0.8 * mm});
            skCircle(sketch, "E45.0.20.20", {"center": v(-25, 97.44) * mm, "radius": 0.8 * mm});
            skCircle(sketch, "E45.0.20.21", {"center": v(-25, 92.44) * mm, "radius": 0.8 * mm});
            skCircle(sketch, "E45.0.20.22", {"center": v(-25, 87.44) * mm, "radius": 0.8 * mm});
            skCircle(sketch, "E45.0.20.23", {"center": v(-25, 82.44) * mm, "radius": 0.8 * mm});
            skCircle(sketch, "E45.0.20.24", {"center": v(-25, 77.44) * mm, "radius": 0.8 * mm});
            skCircle(sketch, "E45.0.20.25", {"center": v(-25, 72.44) * mm, "radius": 0.8 * mm});
            skCircle(sketch, "E45.0.20.26", {"center": v(-25, 67.44) * mm, "radius": 0.8 * mm});
            skCircle(sketch, "E45.0.20.27", {"center": v(-25, 62.44) * mm, "radius": 0.8 * mm});
            skCircle(sketch, "E45.0.20.28", {"center": v(-25, 57.44) * mm, "radius": 0.8 * mm});
            skCircle(sketch, "E45.0.20.29", {"center": v(-25, 52.44) * mm, "radius": 0.8 * mm});
            skCircle(sketch, "E45.0.21.2", {"center": v(-30, 187.44) * mm, "radius": 0.8 * mm});
            skCircle(sketch, "E45.0.21.3", {"center": v(-30, 182.44) * mm, "radius": 0.8 * mm});
            skCircle(sketch, "E45.0.21.4", {"center": v(-30, 177.44) * mm, "radius": 0.8 * mm});
            skCircle(sketch, "E45.0.21.5", {"center": v(-30, 172.44) * mm, "radius": 0.8 * mm});
            skCircle(sketch, "E45.0.21.6", {"center": v(-30, 167.44) * mm, "radius": 0.8 * mm});
            skCircle(sketch, "E45.0.21.7", {"center": v(-30, 162.44) * mm, "radius": 0.8 * mm});
            skCircle(sketch, "E45.0.21.8", {"center": v(-30, 157.44) * mm, "radius": 0.8 * mm});
            skCircle(sketch, "E45.0.21.9", {"center": v(-30, 152.44) * mm, "radius": 0.8 * mm});
            skCircle(sketch, "E45.0.21.10", {"center": v(-30, 147.44) * mm, "radius": 0.8 * mm});
            skCircle(sketch, "E45.0.21.11", {"center": v(-30, 142.44) * mm, "radius": 0.8 * mm});
            skCircle(sketch, "E45.0.21.12", {"center": v(-30, 137.44) * mm, "radius": 0.8 * mm});
            skCircle(sketch, "E45.0.21.13", {"center": v(-30, 132.44) * mm, "radius": 0.8 * mm});
            skCircle(sketch, "E45.0.21.14", {"center": v(-30, 127.44) * mm, "radius": 0.8 * mm});
            skCircle(sketch, "E45.0.21.15", {"center": v(-30, 122.44) * mm, "radius": 0.8 * mm});
            skCircle(sketch, "E45.0.21.16", {"center": v(-30, 117.44) * mm, "radius": 0.8 * mm});
            skCircle(sketch, "E45.0.21.17", {"center": v(-30, 112.44) * mm, "radius": 0.8 * mm});
            skCircle(sketch, "E45.0.21.18", {"center": v(-30, 107.44) * mm, "radius": 0.8 * mm});
            skCircle(sketch, "E45.0.21.19", {"center": v(-30, 102.44) * mm, "radius": 0.8 * mm});
            skCircle(sketch, "E45.0.21.20", {"center": v(-30, 97.44) * mm, "radius": 0.8 * mm});
            skCircle(sketch, "E45.0.21.21", {"center": v(-30, 92.44) * mm, "radius": 0.8 * mm});
            skCircle(sketch, "E45.0.21.22", {"center": v(-30, 87.44) * mm, "radius": 0.8 * mm});
            skCircle(sketch, "E45.0.21.23", {"center": v(-30, 82.44) * mm, "radius": 0.8 * mm});
            skCircle(sketch, "E45.0.21.24", {"center": v(-30, 77.44) * mm, "radius": 0.8 * mm});
            skCircle(sketch, "E45.0.21.25", {"center": v(-30, 72.44) * mm, "radius": 0.8 * mm});
            skCircle(sketch, "E45.0.21.26", {"center": v(-30, 67.44) * mm, "radius": 0.8 * mm});
            skCircle(sketch, "E45.0.21.27", {"center": v(-30, 62.44) * mm, "radius": 0.8 * mm});
            skCircle(sketch, "E45.0.21.28", {"center": v(-30, 57.44) * mm, "radius": 0.8 * mm});
            skCircle(sketch, "E45.0.21.29", {"center": v(-30, 52.44) * mm, "radius": 0.8 * mm});
            skCircle(sketch, "E45.0.22.2", {"center": v(-35, 187.44) * mm, "radius": 0.8 * mm});
            skCircle(sketch, "E45.0.22.3", {"center": v(-35, 182.44) * mm, "radius": 0.8 * mm});
            skCircle(sketch, "E45.0.22.4", {"center": v(-35, 177.44) * mm, "radius": 0.8 * mm});
            skCircle(sketch, "E45.0.22.5", {"center": v(-35, 172.44) * mm, "radius": 0.8 * mm});
            skCircle(sketch, "E45.0.22.6", {"center": v(-35, 167.44) * mm, "radius": 0.8 * mm});
            skCircle(sketch, "E45.0.22.7", {"center": v(-35, 162.44) * mm, "radius": 0.8 * mm});
            skCircle(sketch, "E45.0.22.8", {"center": v(-35, 157.44) * mm, "radius": 0.8 * mm});
            skCircle(sketch, "E45.0.22.9", {"center": v(-35, 152.44) * mm, "radius": 0.8 * mm});
            skCircle(sketch, "E45.0.22.10", {"center": v(-35, 147.44) * mm, "radius": 0.8 * mm});
            skCircle(sketch, "E45.0.22.11", {"center": v(-35, 142.44) * mm, "radius": 0.8 * mm});
            skCircle(sketch, "E45.0.22.12", {"center": v(-35, 137.44) * mm, "radius": 0.8 * mm});
            skCircle(sketch, "E45.0.22.13", {"center": v(-35, 132.44) * mm, "radius": 0.8 * mm});
            skCircle(sketch, "E45.0.22.14", {"center": v(-35, 127.44) * mm, "radius": 0.8 * mm});
            skCircle(sketch, "E45.0.22.15", {"center": v(-35, 122.44) * mm, "radius": 0.8 * mm});
            skCircle(sketch, "E45.0.22.16", {"center": v(-35, 117.44) * mm, "radius": 0.8 * mm});
            skCircle(sketch, "E45.0.22.17", {"center": v(-35, 112.44) * mm, "radius": 0.8 * mm});
            skCircle(sketch, "E45.0.22.18", {"center": v(-35, 107.44) * mm, "radius": 0.8 * mm});
            skCircle(sketch, "E45.0.22.19", {"center": v(-35, 102.44) * mm, "radius": 0.8 * mm});
            skCircle(sketch, "E45.0.22.20", {"center": v(-35, 97.44) * mm, "radius": 0.8 * mm});
            skCircle(sketch, "E45.0.22.21", {"center": v(-35, 92.44) * mm, "radius": 0.8 * mm});
            skCircle(sketch, "E45.0.22.22", {"center": v(-35, 87.44) * mm, "radius": 0.8 * mm});
            skCircle(sketch, "E45.0.22.23", {"center": v(-35, 82.44) * mm, "radius": 0.8 * mm});
            skCircle(sketch, "E45.0.22.24", {"center": v(-35, 77.44) * mm, "radius": 0.8 * mm});
            skCircle(sketch, "E45.0.22.25", {"center": v(-35, 72.44) * mm, "radius": 0.8 * mm});
            skCircle(sketch, "E45.0.22.26", {"center": v(-35, 67.44) * mm, "radius": 0.8 * mm});
            skCircle(sketch, "E45.0.22.27", {"center": v(-35, 62.44) * mm, "radius": 0.8 * mm});
            skCircle(sketch, "E45.0.22.28", {"center": v(-35, 57.44) * mm, "radius": 0.8 * mm});
            skCircle(sketch, "E45.0.22.29", {"center": v(-35, 52.44) * mm, "radius": 0.8 * mm});
            skCircle(sketch, "E45.0.23.2", {"center": v(-40, 187.44) * mm, "radius": 0.8 * mm});
            skCircle(sketch, "E45.0.23.3", {"center": v(-40, 182.44) * mm, "radius": 0.8 * mm});
            skCircle(sketch, "E45.0.23.4", {"center": v(-40, 177.44) * mm, "radius": 0.8 * mm});
            skCircle(sketch, "E45.0.23.5", {"center": v(-40, 172.44) * mm, "radius": 0.8 * mm});
            skCircle(sketch, "E45.0.23.6", {"center": v(-40, 167.44) * mm, "radius": 0.8 * mm});
            skCircle(sketch, "E45.0.23.7", {"center": v(-40, 162.44) * mm, "radius": 0.8 * mm});
            skCircle(sketch, "E45.0.23.8", {"center": v(-40, 157.44) * mm, "radius": 0.8 * mm});
            skCircle(sketch, "E45.0.23.9", {"center": v(-40, 152.44) * mm, "radius": 0.8 * mm});
            skCircle(sketch, "E45.0.23.10", {"center": v(-40, 147.44) * mm, "radius": 0.8 * mm});
            skCircle(sketch, "E45.0.23.11", {"center": v(-40, 142.44) * mm, "radius": 0.8 * mm});
            skCircle(sketch, "E45.0.23.12", {"center": v(-40, 137.44) * mm, "radius": 0.8 * mm});
            skCircle(sketch, "E45.0.23.13", {"center": v(-40, 132.44) * mm, "radius": 0.8 * mm});
            skCircle(sketch, "E45.0.23.14", {"center": v(-40, 127.44) * mm, "radius": 0.8 * mm});
            skCircle(sketch, "E45.0.23.15", {"center": v(-40, 122.44) * mm, "radius": 0.8 * mm});
            skCircle(sketch, "E45.0.23.16", {"center": v(-40, 117.44) * mm, "radius": 0.8 * mm});
            skCircle(sketch, "E45.0.23.17", {"center": v(-40, 112.44) * mm, "radius": 0.8 * mm});
            skCircle(sketch, "E45.0.23.18", {"center": v(-40, 107.44) * mm, "radius": 0.8 * mm});
            skCircle(sketch, "E45.0.23.19", {"center": v(-40, 102.44) * mm, "radius": 0.8 * mm});
            skCircle(sketch, "E45.0.23.20", {"center": v(-40, 97.44) * mm, "radius": 0.8 * mm});
            skCircle(sketch, "E45.0.23.21", {"center": v(-40, 92.44) * mm, "radius": 0.8 * mm});
            skCircle(sketch, "E45.0.23.22", {"center": v(-40, 87.44) * mm, "radius": 0.8 * mm});
            skCircle(sketch, "E45.0.23.23", {"center": v(-40, 82.44) * mm, "radius": 0.8 * mm});
            skCircle(sketch, "E45.0.23.24", {"center": v(-40, 77.44) * mm, "radius": 0.8 * mm});
            skCircle(sketch, "E45.0.23.25", {"center": v(-40, 72.44) * mm, "radius": 0.8 * mm});
            skCircle(sketch, "E45.0.23.26", {"center": v(-40, 67.44) * mm, "radius": 0.8 * mm});
            skCircle(sketch, "E45.0.23.27", {"center": v(-40, 62.44) * mm, "radius": 0.8 * mm});
            skCircle(sketch, "E45.0.23.28", {"center": v(-40, 57.44) * mm, "radius": 0.8 * mm});
            skCircle(sketch, "E45.0.23.29", {"center": v(-40, 52.44) * mm, "radius": 0.8 * mm});
            skCircle(sketch, "E45.0.24.2", {"center": v(-45, 187.44) * mm, "radius": 0.8 * mm});
            skCircle(sketch, "E45.0.24.3", {"center": v(-45, 182.44) * mm, "radius": 0.8 * mm});
            skCircle(sketch, "E45.0.24.4", {"center": v(-45, 177.44) * mm, "radius": 0.8 * mm});
            skCircle(sketch, "E45.0.24.5", {"center": v(-45, 172.44) * mm, "radius": 0.8 * mm});
            skCircle(sketch, "E45.0.24.6", {"center": v(-45, 167.44) * mm, "radius": 0.8 * mm});
            skCircle(sketch, "E45.0.24.7", {"center": v(-45, 162.44) * mm, "radius": 0.8 * mm});
            skCircle(sketch, "E45.0.24.8", {"center": v(-45, 157.44) * mm, "radius": 0.8 * mm});
            skCircle(sketch, "E45.0.24.9", {"center": v(-45, 152.44) * mm, "radius": 0.8 * mm});
            skCircle(sketch, "E45.0.24.10", {"center": v(-45, 147.44) * mm, "radius": 0.8 * mm});
            skCircle(sketch, "E45.0.24.11", {"center": v(-45, 142.44) * mm, "radius": 0.8 * mm});
            skCircle(sketch, "E45.0.24.12", {"center": v(-45, 137.44) * mm, "radius": 0.8 * mm});
            skCircle(sketch, "E45.0.24.13", {"center": v(-45, 132.44) * mm, "radius": 0.8 * mm});
            skCircle(sketch, "E45.0.24.14", {"center": v(-45, 127.44) * mm, "radius": 0.8 * mm});
            skCircle(sketch, "E45.0.24.15", {"center": v(-45, 122.44) * mm, "radius": 0.8 * mm});
            skCircle(sketch, "E45.0.24.16", {"center": v(-45, 117.44) * mm, "radius": 0.8 * mm});
            skCircle(sketch, "E45.0.24.17", {"center": v(-45, 112.44) * mm, "radius": 0.8 * mm});
            skCircle(sketch, "E45.0.24.18", {"center": v(-45, 107.44) * mm, "radius": 0.8 * mm});
            skCircle(sketch, "E45.0.24.19", {"center": v(-45, 102.44) * mm, "radius": 0.8 * mm});
            skCircle(sketch, "E45.0.24.20", {"center": v(-45, 97.44) * mm, "radius": 0.8 * mm});
            skCircle(sketch, "E45.0.24.21", {"center": v(-45, 92.44) * mm, "radius": 0.8 * mm});
            skCircle(sketch, "E45.0.24.22", {"center": v(-45, 87.44) * mm, "radius": 0.8 * mm});
            skCircle(sketch, "E45.0.24.23", {"center": v(-45, 82.44) * mm, "radius": 0.8 * mm});
            skCircle(sketch, "E45.0.24.24", {"center": v(-45, 77.44) * mm, "radius": 0.8 * mm});
            skCircle(sketch, "E45.0.24.25", {"center": v(-45, 72.44) * mm, "radius": 0.8 * mm});
            skCircle(sketch, "E45.0.24.26", {"center": v(-45, 67.44) * mm, "radius": 0.8 * mm});
            skCircle(sketch, "E45.0.24.27", {"center": v(-45, 62.44) * mm, "radius": 0.8 * mm});
            skCircle(sketch, "E45.0.24.28", {"center": v(-45, 57.44) * mm, "radius": 0.8 * mm});
            skCircle(sketch, "E45.0.24.29", {"center": v(-45, 52.44) * mm, "radius": 0.8 * mm});
            skCircle(sketch, "E45.0.25.2", {"center": v(-50, 187.44) * mm, "radius": 0.8 * mm});
            skCircle(sketch, "E45.0.25.3", {"center": v(-50, 182.44) * mm, "radius": 0.8 * mm});
            skCircle(sketch, "E45.0.25.4", {"center": v(-50, 177.44) * mm, "radius": 0.8 * mm});
            skCircle(sketch, "E45.0.25.5", {"center": v(-50, 172.44) * mm, "radius": 0.8 * mm});
            skCircle(sketch, "E45.0.25.6", {"center": v(-50, 167.44) * mm, "radius": 0.8 * mm});
            skCircle(sketch, "E45.0.25.7", {"center": v(-50, 162.44) * mm, "radius": 0.8 * mm});
            skCircle(sketch, "E45.0.25.8", {"center": v(-50, 157.44) * mm, "radius": 0.8 * mm});
            skCircle(sketch, "E45.0.25.9", {"center": v(-50, 152.44) * mm, "radius": 0.8 * mm});
            skCircle(sketch, "E45.0.25.10", {"center": v(-50, 147.44) * mm, "radius": 0.8 * mm});
            skCircle(sketch, "E45.0.25.11", {"center": v(-50, 142.44) * mm, "radius": 0.8 * mm});
            skCircle(sketch, "E45.0.25.12", {"center": v(-50, 137.44) * mm, "radius": 0.8 * mm});
            skCircle(sketch, "E45.0.25.13", {"center": v(-50, 132.44) * mm, "radius": 0.8 * mm});
            skCircle(sketch, "E45.0.25.14", {"center": v(-50, 127.44) * mm, "radius": 0.8 * mm});
            skCircle(sketch, "E45.0.25.15", {"center": v(-50, 122.44) * mm, "radius": 0.8 * mm});
            skCircle(sketch, "E45.0.25.16", {"center": v(-50, 117.44) * mm, "radius": 0.8 * mm});
            skCircle(sketch, "E45.0.25.17", {"center": v(-50, 112.44) * mm, "radius": 0.8 * mm});
            skCircle(sketch, "E45.0.25.18", {"center": v(-50, 107.44) * mm, "radius": 0.8 * mm});
            skCircle(sketch, "E45.0.25.19", {"center": v(-50, 102.44) * mm, "radius": 0.8 * mm});
            skCircle(sketch, "E45.0.25.20", {"center": v(-50, 97.44) * mm, "radius": 0.8 * mm});
            skCircle(sketch, "E45.0.25.21", {"center": v(-50, 92.44) * mm, "radius": 0.8 * mm});
            skCircle(sketch, "E45.0.25.22", {"center": v(-50, 87.44) * mm, "radius": 0.8 * mm});
            skCircle(sketch, "E45.0.25.23", {"center": v(-50, 82.44) * mm, "radius": 0.8 * mm});
            skCircle(sketch, "E45.0.25.24", {"center": v(-50, 77.44) * mm, "radius": 0.8 * mm});
            skCircle(sketch, "E45.0.25.25", {"center": v(-50, 72.44) * mm, "radius": 0.8 * mm});
            skCircle(sketch, "E45.0.25.26", {"center": v(-50, 67.44) * mm, "radius": 0.8 * mm});
            skCircle(sketch, "E45.0.25.27", {"center": v(-50, 62.44) * mm, "radius": 0.8 * mm});
            skCircle(sketch, "E45.0.25.28", {"center": v(-50, 57.44) * mm, "radius": 0.8 * mm});
            skCircle(sketch, "E45.0.25.29", {"center": v(-50, 52.44) * mm, "radius": 0.8 * mm});
            skCircle(sketch, "E45.0.26.2", {"center": v(-55, 187.44) * mm, "radius": 0.8 * mm});
            skCircle(sketch, "E45.0.26.3", {"center": v(-55, 182.44) * mm, "radius": 0.8 * mm});
            skCircle(sketch, "E45.0.26.4", {"center": v(-55, 177.44) * mm, "radius": 0.8 * mm});
            skCircle(sketch, "E45.0.26.5", {"center": v(-55, 172.44) * mm, "radius": 0.8 * mm});
            skCircle(sketch, "E45.0.26.6", {"center": v(-55, 167.44) * mm, "radius": 0.8 * mm});
            skCircle(sketch, "E45.0.26.7", {"center": v(-55, 162.44) * mm, "radius": 0.8 * mm});
            skCircle(sketch, "E45.0.26.8", {"center": v(-55, 157.44) * mm, "radius": 0.8 * mm});
            skCircle(sketch, "E45.0.26.9", {"center": v(-55, 152.44) * mm, "radius": 0.8 * mm});
            skCircle(sketch, "E45.0.26.10", {"center": v(-55, 147.44) * mm, "radius": 0.8 * mm});
            skCircle(sketch, "E45.0.26.11", {"center": v(-55, 142.44) * mm, "radius": 0.8 * mm});
            skCircle(sketch, "E45.0.26.12", {"center": v(-55, 137.44) * mm, "radius": 0.8 * mm});
            skCircle(sketch, "E45.0.26.13", {"center": v(-55, 132.44) * mm, "radius": 0.8 * mm});
            skCircle(sketch, "E45.0.26.14", {"center": v(-55, 127.44) * mm, "radius": 0.8 * mm});
            skCircle(sketch, "E45.0.26.15", {"center": v(-55, 122.44) * mm, "radius": 0.8 * mm});
            skCircle(sketch, "E45.0.26.16", {"center": v(-55, 117.44) * mm, "radius": 0.8 * mm});
            skCircle(sketch, "E45.0.26.17", {"center": v(-55, 112.44) * mm, "radius": 0.8 * mm});
            skCircle(sketch, "E45.0.26.18", {"center": v(-55, 107.44) * mm, "radius": 0.8 * mm});
            skCircle(sketch, "E45.0.26.19", {"center": v(-55, 102.44) * mm, "radius": 0.8 * mm});
            skCircle(sketch, "E45.0.26.20", {"center": v(-55, 97.44) * mm, "radius": 0.8 * mm});
            skCircle(sketch, "E45.0.26.21", {"center": v(-55, 92.44) * mm, "radius": 0.8 * mm});
            skCircle(sketch, "E45.0.26.22", {"center": v(-55, 87.44) * mm, "radius": 0.8 * mm});
            skCircle(sketch, "E45.0.26.23", {"center": v(-55, 82.44) * mm, "radius": 0.8 * mm});
            skCircle(sketch, "E45.0.26.24", {"center": v(-55, 77.44) * mm, "radius": 0.8 * mm});
            skCircle(sketch, "E45.0.26.25", {"center": v(-55, 72.44) * mm, "radius": 0.8 * mm});
            skCircle(sketch, "E45.0.26.26", {"center": v(-55, 67.44) * mm, "radius": 0.8 * mm});
            skCircle(sketch, "E45.0.26.27", {"center": v(-55, 62.44) * mm, "radius": 0.8 * mm});
            skCircle(sketch, "E45.0.26.28", {"center": v(-55, 57.44) * mm, "radius": 0.8 * mm});
            skCircle(sketch, "E45.0.26.29", {"center": v(-55, 52.44) * mm, "radius": 0.8 * mm});
            skCircle(sketch, "E45.0.27.2", {"center": v(-60, 187.44) * mm, "radius": 0.8 * mm});
            skCircle(sketch, "E45.0.27.3", {"center": v(-60, 182.44) * mm, "radius": 0.8 * mm});
            skCircle(sketch, "E45.0.27.4", {"center": v(-60, 177.44) * mm, "radius": 0.8 * mm});
            skCircle(sketch, "E45.0.27.5", {"center": v(-60, 172.44) * mm, "radius": 0.8 * mm});
            skCircle(sketch, "E45.0.27.6", {"center": v(-60, 167.44) * mm, "radius": 0.8 * mm});
            skCircle(sketch, "E45.0.27.7", {"center": v(-60, 162.44) * mm, "radius": 0.8 * mm});
            skCircle(sketch, "E45.0.27.8", {"center": v(-60, 157.44) * mm, "radius": 0.8 * mm});
            skCircle(sketch, "E45.0.27.9", {"center": v(-60, 152.44) * mm, "radius": 0.8 * mm});
            skCircle(sketch, "E45.0.27.10", {"center": v(-60, 147.44) * mm, "radius": 0.8 * mm});
            skCircle(sketch, "E45.0.27.11", {"center": v(-60, 142.44) * mm, "radius": 0.8 * mm});
            skCircle(sketch, "E45.0.27.12", {"center": v(-60, 137.44) * mm, "radius": 0.8 * mm});
            skCircle(sketch, "E45.0.27.13", {"center": v(-60, 132.44) * mm, "radius": 0.8 * mm});
            skCircle(sketch, "E45.0.27.14", {"center": v(-60, 127.44) * mm, "radius": 0.8 * mm});
            skCircle(sketch, "E45.0.27.15", {"center": v(-60, 122.44) * mm, "radius": 0.8 * mm});
            skCircle(sketch, "E45.0.27.16", {"center": v(-60, 117.44) * mm, "radius": 0.8 * mm});
            skCircle(sketch, "E45.0.27.17", {"center": v(-60, 112.44) * mm, "radius": 0.8 * mm});
            skCircle(sketch, "E45.0.27.18", {"center": v(-60, 107.44) * mm, "radius": 0.8 * mm});
            skCircle(sketch, "E45.0.27.19", {"center": v(-60, 102.44) * mm, "radius": 0.8 * mm});
            skCircle(sketch, "E45.0.27.20", {"center": v(-60, 97.44) * mm, "radius": 0.8 * mm});
            skCircle(sketch, "E45.0.27.21", {"center": v(-60, 92.44) * mm, "radius": 0.8 * mm});
            skCircle(sketch, "E45.0.27.22", {"center": v(-60, 87.44) * mm, "radius": 0.8 * mm});
            skCircle(sketch, "E45.0.27.23", {"center": v(-60, 82.44) * mm, "radius": 0.8 * mm});
            skCircle(sketch, "E45.0.27.24", {"center": v(-60, 77.44) * mm, "radius": 0.8 * mm});
            skCircle(sketch, "E45.0.27.25", {"center": v(-60, 72.44) * mm, "radius": 0.8 * mm});
            skCircle(sketch, "E45.0.27.26", {"center": v(-60, 67.44) * mm, "radius": 0.8 * mm});
            skCircle(sketch, "E45.0.27.27", {"center": v(-60, 62.44) * mm, "radius": 0.8 * mm});
            skCircle(sketch, "E45.0.27.28", {"center": v(-60, 57.44) * mm, "radius": 0.8 * mm});
            skCircle(sketch, "E45.0.27.29", {"center": v(-60, 52.44) * mm, "radius": 0.8 * mm});
            skCircle(sketch, "E45.0.28.2", {"center": v(-65, 187.44) * mm, "radius": 0.8 * mm});
            skCircle(sketch, "E45.0.28.3", {"center": v(-65, 182.44) * mm, "radius": 0.8 * mm});
            skCircle(sketch, "E45.0.28.4", {"center": v(-65, 177.44) * mm, "radius": 0.8 * mm});
            skCircle(sketch, "E45.0.28.5", {"center": v(-65, 172.44) * mm, "radius": 0.8 * mm});
            skCircle(sketch, "E45.0.28.6", {"center": v(-65, 167.44) * mm, "radius": 0.8 * mm});
            skCircle(sketch, "E45.0.28.7", {"center": v(-65, 162.44) * mm, "radius": 0.8 * mm});
            skCircle(sketch, "E45.0.28.8", {"center": v(-65, 157.44) * mm, "radius": 0.8 * mm});
            skCircle(sketch, "E45.0.28.9", {"center": v(-65, 152.44) * mm, "radius": 0.8 * mm});
            skCircle(sketch, "E45.0.28.10", {"center": v(-65, 147.44) * mm, "radius": 0.8 * mm});
            skCircle(sketch, "E45.0.28.11", {"center": v(-65, 142.44) * mm, "radius": 0.8 * mm});
            skCircle(sketch, "E45.0.28.12", {"center": v(-65, 137.44) * mm, "radius": 0.8 * mm});
            skCircle(sketch, "E45.0.28.13", {"center": v(-65, 132.44) * mm, "radius": 0.8 * mm});
            skCircle(sketch, "E45.0.28.14", {"center": v(-65, 127.44) * mm, "radius": 0.8 * mm});
            skCircle(sketch, "E45.0.28.15", {"center": v(-65, 122.44) * mm, "radius": 0.8 * mm});
            skCircle(sketch, "E45.0.28.16", {"center": v(-65, 117.44) * mm, "radius": 0.8 * mm});
            skCircle(sketch, "E45.0.28.17", {"center": v(-65, 112.44) * mm, "radius": 0.8 * mm});
            skCircle(sketch, "E45.0.28.18", {"center": v(-65, 107.44) * mm, "radius": 0.8 * mm});
            skCircle(sketch, "E45.0.28.19", {"center": v(-65, 102.44) * mm, "radius": 0.8 * mm});
            skCircle(sketch, "E45.0.28.20", {"center": v(-65, 97.44) * mm, "radius": 0.8 * mm});
            skCircle(sketch, "E45.0.28.21", {"center": v(-65, 92.44) * mm, "radius": 0.8 * mm});
            skCircle(sketch, "E45.0.28.22", {"center": v(-65, 87.44) * mm, "radius": 0.8 * mm});
            skCircle(sketch, "E45.0.28.23", {"center": v(-65, 82.44) * mm, "radius": 0.8 * mm});
            skCircle(sketch, "E45.0.28.24", {"center": v(-65, 77.44) * mm, "radius": 0.8 * mm});
            skCircle(sketch, "E45.0.28.25", {"center": v(-65, 72.44) * mm, "radius": 0.8 * mm});
            skCircle(sketch, "E45.0.28.26", {"center": v(-65, 67.44) * mm, "radius": 0.8 * mm});
            skCircle(sketch, "E45.0.28.27", {"center": v(-65, 62.44) * mm, "radius": 0.8 * mm});
            skCircle(sketch, "E45.0.28.28", {"center": v(-65, 57.44) * mm, "radius": 0.8 * mm});
            skCircle(sketch, "E45.0.28.29", {"center": v(-65, 52.44) * mm, "radius": 0.8 * mm});
            skCircle(sketch, "E45.0.29.2", {"center": v(-70, 187.44) * mm, "radius": 0.8 * mm});
            skCircle(sketch, "E45.0.29.3", {"center": v(-70, 182.44) * mm, "radius": 0.8 * mm});
            skCircle(sketch, "E45.0.29.4", {"center": v(-70, 177.44) * mm, "radius": 0.8 * mm});
            skCircle(sketch, "E45.0.29.5", {"center": v(-70, 172.44) * mm, "radius": 0.8 * mm});
            skCircle(sketch, "E45.0.29.6", {"center": v(-70, 167.44) * mm, "radius": 0.8 * mm});
            skCircle(sketch, "E45.0.29.7", {"center": v(-70, 162.44) * mm, "radius": 0.8 * mm});
            skCircle(sketch, "E45.0.29.8", {"center": v(-70, 157.44) * mm, "radius": 0.8 * mm});
            skCircle(sketch, "E45.0.29.9", {"center": v(-70, 152.44) * mm, "radius": 0.8 * mm});
            skCircle(sketch, "E45.0.29.10", {"center": v(-70, 147.44) * mm, "radius": 0.8 * mm});
            skCircle(sketch, "E45.0.29.11", {"center": v(-70, 142.44) * mm, "radius": 0.8 * mm});
            skCircle(sketch, "E45.0.29.12", {"center": v(-70, 137.44) * mm, "radius": 0.8 * mm});
            skCircle(sketch, "E45.0.29.13", {"center": v(-70, 132.44) * mm, "radius": 0.8 * mm});
            skCircle(sketch, "E45.0.29.14", {"center": v(-70, 127.44) * mm, "radius": 0.8 * mm});
            skCircle(sketch, "E45.0.29.15", {"center": v(-70, 122.44) * mm, "radius": 0.8 * mm});
            skCircle(sketch, "E45.0.29.16", {"center": v(-70, 117.44) * mm, "radius": 0.8 * mm});
            skCircle(sketch, "E45.0.29.17", {"center": v(-70, 112.44) * mm, "radius": 0.8 * mm});
            skCircle(sketch, "E45.0.29.18", {"center": v(-70, 107.44) * mm, "radius": 0.8 * mm});
            skCircle(sketch, "E45.0.29.19", {"center": v(-70, 102.44) * mm, "radius": 0.8 * mm});
            skCircle(sketch, "E45.0.29.20", {"center": v(-70, 97.44) * mm, "radius": 0.8 * mm});
            skCircle(sketch, "E45.0.29.21", {"center": v(-70, 92.44) * mm, "radius": 0.8 * mm});
            skCircle(sketch, "E45.0.29.22", {"center": v(-70, 87.44) * mm, "radius": 0.8 * mm});
            skCircle(sketch, "E45.0.29.23", {"center": v(-70, 82.44) * mm, "radius": 0.8 * mm});
            skCircle(sketch, "E45.0.29.24", {"center": v(-70, 77.44) * mm, "radius": 0.8 * mm});
            skCircle(sketch, "E45.0.29.25", {"center": v(-70, 72.44) * mm, "radius": 0.8 * mm});
            skCircle(sketch, "E45.0.29.26", {"center": v(-70, 67.44) * mm, "radius": 0.8 * mm});
            skCircle(sketch, "E45.0.29.27", {"center": v(-70, 62.44) * mm, "radius": 0.8 * mm});
            skCircle(sketch, "E45.0.29.28", {"center": v(-70, 57.44) * mm, "radius": 0.8 * mm});
            skCircle(sketch, "E45.0.29.29", {"center": v(-70, 52.44) * mm, "radius": 0.8 * mm});
            skCircle(sketch, "E45.0.30.2", {"center": v(-75, 187.44) * mm, "radius": 0.8 * mm});
            skCircle(sketch, "E45.0.30.3", {"center": v(-75, 182.44) * mm, "radius": 0.8 * mm});
            skCircle(sketch, "E45.0.30.4", {"center": v(-75, 177.44) * mm, "radius": 0.8 * mm});
            skCircle(sketch, "E45.0.30.5", {"center": v(-75, 172.44) * mm, "radius": 0.8 * mm});
            skCircle(sketch, "E45.0.30.6", {"center": v(-75, 167.44) * mm, "radius": 0.8 * mm});
            skCircle(sketch, "E45.0.30.7", {"center": v(-75, 162.44) * mm, "radius": 0.8 * mm});
            skCircle(sketch, "E45.0.30.8", {"center": v(-75, 157.44) * mm, "radius": 0.8 * mm});
            skCircle(sketch, "E45.0.30.9", {"center": v(-75, 152.44) * mm, "radius": 0.8 * mm});
            skCircle(sketch, "E45.0.30.10", {"center": v(-75, 147.44) * mm, "radius": 0.8 * mm});
            skCircle(sketch, "E45.0.30.11", {"center": v(-75, 142.44) * mm, "radius": 0.8 * mm});
            skCircle(sketch, "E45.0.30.12", {"center": v(-75, 137.44) * mm, "radius": 0.8 * mm});
            skCircle(sketch, "E45.0.30.13", {"center": v(-75, 132.44) * mm, "radius": 0.8 * mm});
            skCircle(sketch, "E45.0.30.14", {"center": v(-75, 127.44) * mm, "radius": 0.8 * mm});
            skCircle(sketch, "E45.0.30.15", {"center": v(-75, 122.44) * mm, "radius": 0.8 * mm});
            skCircle(sketch, "E45.0.30.16", {"center": v(-75, 117.44) * mm, "radius": 0.8 * mm});
            skCircle(sketch, "E45.0.30.17", {"center": v(-75, 112.44) * mm, "radius": 0.8 * mm});
            skCircle(sketch, "E45.0.30.18", {"center": v(-75, 107.44) * mm, "radius": 0.8 * mm});
            skCircle(sketch, "E45.0.30.19", {"center": v(-75, 102.44) * mm, "radius": 0.8 * mm});
            skCircle(sketch, "E45.0.30.20", {"center": v(-75, 97.44) * mm, "radius": 0.8 * mm});
            skCircle(sketch, "E45.0.30.21", {"center": v(-75, 92.44) * mm, "radius": 0.8 * mm});
            skCircle(sketch, "E45.0.30.22", {"center": v(-75, 87.44) * mm, "radius": 0.8 * mm});
            skCircle(sketch, "E45.0.30.23", {"center": v(-75, 82.44) * mm, "radius": 0.8 * mm});
            skCircle(sketch, "E45.0.30.24", {"center": v(-75, 77.44) * mm, "radius": 0.8 * mm});
            skCircle(sketch, "E45.0.30.25", {"center": v(-75, 72.44) * mm, "radius": 0.8 * mm});
            skCircle(sketch, "E45.0.30.26", {"center": v(-75, 67.44) * mm, "radius": 0.8 * mm});
            skCircle(sketch, "E45.0.30.27", {"center": v(-75, 62.44) * mm, "radius": 0.8 * mm});
            skCircle(sketch, "E45.0.30.28", {"center": v(-75, 57.44) * mm, "radius": 0.8 * mm});
            skCircle(sketch, "E45.0.30.29", {"center": v(-75, 52.44) * mm, "radius": 0.8 * mm});
            skCircle(sketch, "E45.0.31.2", {"center": v(-80, 187.44) * mm, "radius": 0.8 * mm});
            skCircle(sketch, "E45.0.31.3", {"center": v(-80, 182.44) * mm, "radius": 0.8 * mm});
            skCircle(sketch, "E45.0.31.4", {"center": v(-80, 177.44) * mm, "radius": 0.8 * mm});
            skCircle(sketch, "E45.0.31.5", {"center": v(-80, 172.44) * mm, "radius": 0.8 * mm});
            skCircle(sketch, "E45.0.31.6", {"center": v(-80, 167.44) * mm, "radius": 0.8 * mm});
            skCircle(sketch, "E45.0.31.7", {"center": v(-80, 162.44) * mm, "radius": 0.8 * mm});
            skCircle(sketch, "E45.0.31.8", {"center": v(-80, 157.44) * mm, "radius": 0.8 * mm});
            skCircle(sketch, "E45.0.31.9", {"center": v(-80, 152.44) * mm, "radius": 0.8 * mm});
            skCircle(sketch, "E45.0.31.10", {"center": v(-80, 147.44) * mm, "radius": 0.8 * mm});
            skCircle(sketch, "E45.0.31.11", {"center": v(-80, 142.44) * mm, "radius": 0.8 * mm});
            skCircle(sketch, "E45.0.31.12", {"center": v(-80, 137.44) * mm, "radius": 0.8 * mm});
            skCircle(sketch, "E45.0.31.13", {"center": v(-80, 132.44) * mm, "radius": 0.8 * mm});
            skCircle(sketch, "E45.0.31.14", {"center": v(-80, 127.44) * mm, "radius": 0.8 * mm});
            skCircle(sketch, "E45.0.31.15", {"center": v(-80, 122.44) * mm, "radius": 0.8 * mm});
            skCircle(sketch, "E45.0.31.16", {"center": v(-80, 117.44) * mm, "radius": 0.8 * mm});
            skCircle(sketch, "E45.0.31.17", {"center": v(-80, 112.44) * mm, "radius": 0.8 * mm});
            skCircle(sketch, "E45.0.31.18", {"center": v(-80, 107.44) * mm, "radius": 0.8 * mm});
            skCircle(sketch, "E45.0.31.19", {"center": v(-80, 102.44) * mm, "radius": 0.8 * mm});
            skCircle(sketch, "E45.0.31.20", {"center": v(-80, 97.44) * mm, "radius": 0.8 * mm});
            skCircle(sketch, "E45.0.31.21", {"center": v(-80, 92.44) * mm, "radius": 0.8 * mm});
            skCircle(sketch, "E45.0.31.22", {"center": v(-80, 87.44) * mm, "radius": 0.8 * mm});
            skCircle(sketch, "E45.0.31.23", {"center": v(-80, 82.44) * mm, "radius": 0.8 * mm});
            skCircle(sketch, "E45.0.31.24", {"center": v(-80, 77.44) * mm, "radius": 0.8 * mm});
            skCircle(sketch, "E45.0.31.25", {"center": v(-80, 72.44) * mm, "radius": 0.8 * mm});
            skCircle(sketch, "E45.0.31.26", {"center": v(-80, 67.44) * mm, "radius": 0.8 * mm});
            skCircle(sketch, "E45.0.31.27", {"center": v(-80, 62.44) * mm, "radius": 0.8 * mm});
            skCircle(sketch, "E45.0.31.28", {"center": v(-80, 57.44) * mm, "radius": 0.8 * mm});
            skCircle(sketch, "E45.0.31.29", {"center": v(-80, 52.44) * mm, "radius": 0.8 * mm});
            skCircle(sketch, "E45.0.32.2", {"center": v(-85, 187.44) * mm, "radius": 0.8 * mm});
            skCircle(sketch, "E45.0.32.3", {"center": v(-85, 182.44) * mm, "radius": 0.8 * mm});
            skCircle(sketch, "E45.0.32.4", {"center": v(-85, 177.44) * mm, "radius": 0.8 * mm});
            skCircle(sketch, "E45.0.32.5", {"center": v(-85, 172.44) * mm, "radius": 0.8 * mm});
            skCircle(sketch, "E45.0.32.6", {"center": v(-85, 167.44) * mm, "radius": 0.8 * mm});
            skCircle(sketch, "E45.0.32.7", {"center": v(-85, 162.44) * mm, "radius": 0.8 * mm});
            skCircle(sketch, "E45.0.32.8", {"center": v(-85, 157.44) * mm, "radius": 0.8 * mm});
            skCircle(sketch, "E45.0.32.9", {"center": v(-85, 152.44) * mm, "radius": 0.8 * mm});
            skCircle(sketch, "E45.0.32.10", {"center": v(-85, 147.44) * mm, "radius": 0.8 * mm});
            skCircle(sketch, "E45.0.32.11", {"center": v(-85, 142.44) * mm, "radius": 0.8 * mm});
            skCircle(sketch, "E45.0.32.12", {"center": v(-85, 137.44) * mm, "radius": 0.8 * mm});
            skCircle(sketch, "E45.0.32.13", {"center": v(-85, 132.44) * mm, "radius": 0.8 * mm});
            skCircle(sketch, "E45.0.32.14", {"center": v(-85, 127.44) * mm, "radius": 0.8 * mm});
            skCircle(sketch, "E45.0.32.15", {"center": v(-85, 122.44) * mm, "radius": 0.8 * mm});
            skCircle(sketch, "E45.0.32.16", {"center": v(-85, 117.44) * mm, "radius": 0.8 * mm});
            skCircle(sketch, "E45.0.32.17", {"center": v(-85, 112.44) * mm, "radius": 0.8 * mm});
            skCircle(sketch, "E45.0.32.18", {"center": v(-85, 107.44) * mm, "radius": 0.8 * mm});
            skCircle(sketch, "E45.0.32.19", {"center": v(-85, 102.44) * mm, "radius": 0.8 * mm});
            skCircle(sketch, "E45.0.32.20", {"center": v(-85, 97.44) * mm, "radius": 0.8 * mm});
            skCircle(sketch, "E45.0.32.21", {"center": v(-85, 92.44) * mm, "radius": 0.8 * mm});
            skCircle(sketch, "E45.0.32.22", {"center": v(-85, 87.44) * mm, "radius": 0.8 * mm});
            skCircle(sketch, "E45.0.32.23", {"center": v(-85, 82.44) * mm, "radius": 0.8 * mm});
            skCircle(sketch, "E45.0.32.24", {"center": v(-85, 77.44) * mm, "radius": 0.8 * mm});
            skCircle(sketch, "E45.0.32.25", {"center": v(-85, 72.44) * mm, "radius": 0.8 * mm});
            skCircle(sketch, "E45.0.32.26", {"center": v(-85, 67.44) * mm, "radius": 0.8 * mm});
            skCircle(sketch, "E45.0.32.27", {"center": v(-85, 62.44) * mm, "radius": 0.8 * mm});
            skCircle(sketch, "E45.0.32.28", {"center": v(-85, 57.44) * mm, "radius": 0.8 * mm});
            skCircle(sketch, "E45.0.32.29", {"center": v(-85, 52.44) * mm, "radius": 0.8 * mm});
            skCircle(sketch, "E45.0.33.2", {"center": v(-90, 187.44) * mm, "radius": 0.8 * mm});
            skCircle(sketch, "E45.0.33.3", {"center": v(-90, 182.44) * mm, "radius": 0.8 * mm});
            skCircle(sketch, "E45.0.33.4", {"center": v(-90, 177.44) * mm, "radius": 0.8 * mm});
            skCircle(sketch, "E45.0.33.5", {"center": v(-90, 172.44) * mm, "radius": 0.8 * mm});
            skCircle(sketch, "E45.0.33.6", {"center": v(-90, 167.44) * mm, "radius": 0.8 * mm});
            skCircle(sketch, "E45.0.33.7", {"center": v(-90, 162.44) * mm, "radius": 0.8 * mm});
            skCircle(sketch, "E45.0.33.8", {"center": v(-90, 157.44) * mm, "radius": 0.8 * mm});
            skCircle(sketch, "E45.0.33.9", {"center": v(-90, 152.44) * mm, "radius": 0.8 * mm});
            skCircle(sketch, "E45.0.33.10", {"center": v(-90, 147.44) * mm, "radius": 0.8 * mm});
            skCircle(sketch, "E45.0.33.11", {"center": v(-90, 142.44) * mm, "radius": 0.8 * mm});
            skCircle(sketch, "E45.0.33.12", {"center": v(-90, 137.44) * mm, "radius": 0.8 * mm});
            skCircle(sketch, "E45.0.33.13", {"center": v(-90, 132.44) * mm, "radius": 0.8 * mm});
            skCircle(sketch, "E45.0.33.14", {"center": v(-90, 127.44) * mm, "radius": 0.8 * mm});
            skCircle(sketch, "E45.0.33.15", {"center": v(-90, 122.44) * mm, "radius": 0.8 * mm});
            skCircle(sketch, "E45.0.33.16", {"center": v(-90, 117.44) * mm, "radius": 0.8 * mm});
            skCircle(sketch, "E45.0.33.17", {"center": v(-90, 112.44) * mm, "radius": 0.8 * mm});
            skCircle(sketch, "E45.0.33.18", {"center": v(-90, 107.44) * mm, "radius": 0.8 * mm});
            skCircle(sketch, "E45.0.33.19", {"center": v(-90, 102.44) * mm, "radius": 0.8 * mm});
            skCircle(sketch, "E45.0.33.20", {"center": v(-90, 97.44) * mm, "radius": 0.8 * mm});
            skCircle(sketch, "E45.0.33.21", {"center": v(-90, 92.44) * mm, "radius": 0.8 * mm});
            skCircle(sketch, "E45.0.33.22", {"center": v(-90, 87.44) * mm, "radius": 0.8 * mm});
            skCircle(sketch, "E45.0.33.23", {"center": v(-90, 82.44) * mm, "radius": 0.8 * mm});
            skCircle(sketch, "E45.0.33.24", {"center": v(-90, 77.44) * mm, "radius": 0.8 * mm});
            skCircle(sketch, "E45.0.33.25", {"center": v(-90, 72.44) * mm, "radius": 0.8 * mm});
            skCircle(sketch, "E45.0.33.26", {"center": v(-90, 67.44) * mm, "radius": 0.8 * mm});
            skCircle(sketch, "E45.0.33.27", {"center": v(-90, 62.44) * mm, "radius": 0.8 * mm});
            skCircle(sketch, "E45.0.33.28", {"center": v(-90, 57.44) * mm, "radius": 0.8 * mm});
            skCircle(sketch, "E45.0.33.29", {"center": v(-90, 52.44) * mm, "radius": 0.8 * mm});
            skCircle(sketch, "E45.0.34.2", {"center": v(-95, 187.44) * mm, "radius": 0.8 * mm});
            skCircle(sketch, "E45.0.34.3", {"center": v(-95, 182.44) * mm, "radius": 0.8 * mm});
            skCircle(sketch, "E45.0.34.4", {"center": v(-95, 177.44) * mm, "radius": 0.8 * mm});
            skCircle(sketch, "E45.0.34.5", {"center": v(-95, 172.44) * mm, "radius": 0.8 * mm});
            skCircle(sketch, "E45.0.34.6", {"center": v(-95, 167.44) * mm, "radius": 0.8 * mm});
            skCircle(sketch, "E45.0.34.7", {"center": v(-95, 162.44) * mm, "radius": 0.8 * mm});
            skCircle(sketch, "E45.0.34.8", {"center": v(-95, 157.44) * mm, "radius": 0.8 * mm});
            skCircle(sketch, "E45.0.34.9", {"center": v(-95, 152.44) * mm, "radius": 0.8 * mm});
            skCircle(sketch, "E45.0.34.10", {"center": v(-95, 147.44) * mm, "radius": 0.8 * mm});
            skCircle(sketch, "E45.0.34.11", {"center": v(-95, 142.44) * mm, "radius": 0.8 * mm});
            skCircle(sketch, "E45.0.34.12", {"center": v(-95, 137.44) * mm, "radius": 0.8 * mm});
            skCircle(sketch, "E45.0.34.13", {"center": v(-95, 132.44) * mm, "radius": 0.8 * mm});
            skCircle(sketch, "E45.0.34.14", {"center": v(-95, 127.44) * mm, "radius": 0.8 * mm});
            skCircle(sketch, "E45.0.34.15", {"center": v(-95, 122.44) * mm, "radius": 0.8 * mm});
            skCircle(sketch, "E45.0.34.16", {"center": v(-95, 117.44) * mm, "radius": 0.8 * mm});
            skCircle(sketch, "E45.0.34.17", {"center": v(-95, 112.44) * mm, "radius": 0.8 * mm});
            skCircle(sketch, "E45.0.34.18", {"center": v(-95, 107.44) * mm, "radius": 0.8 * mm});
            skCircle(sketch, "E45.0.34.19", {"center": v(-95, 102.44) * mm, "radius": 0.8 * mm});
            skCircle(sketch, "E45.0.34.20", {"center": v(-95, 97.44) * mm, "radius": 0.8 * mm});
            skCircle(sketch, "E45.0.34.21", {"center": v(-95, 92.44) * mm, "radius": 0.8 * mm});
            skCircle(sketch, "E45.0.34.22", {"center": v(-95, 87.44) * mm, "radius": 0.8 * mm});
            skCircle(sketch, "E45.0.34.23", {"center": v(-95, 82.44) * mm, "radius": 0.8 * mm});
            skCircle(sketch, "E45.0.34.24", {"center": v(-95, 77.44) * mm, "radius": 0.8 * mm});
            skCircle(sketch, "E45.0.34.25", {"center": v(-95, 72.44) * mm, "radius": 0.8 * mm});
            skCircle(sketch, "E45.0.34.26", {"center": v(-95, 67.44) * mm, "radius": 0.8 * mm});
            skCircle(sketch, "E45.0.34.27", {"center": v(-95, 62.44) * mm, "radius": 0.8 * mm});
            skCircle(sketch, "E45.0.34.28", {"center": v(-95, 57.44) * mm, "radius": 0.8 * mm});
            skCircle(sketch, "E45.0.34.29", {"center": v(-95, 52.44) * mm, "radius": 0.8 * mm});
            skCircle(sketch, "E45.0.35.2", {"center": v(-100, 187.44) * mm, "radius": 0.8 * mm});
            skCircle(sketch, "E45.0.35.3", {"center": v(-100, 182.44) * mm, "radius": 0.8 * mm});
            skCircle(sketch, "E45.0.35.4", {"center": v(-100, 177.44) * mm, "radius": 0.8 * mm});
            skCircle(sketch, "E45.0.35.5", {"center": v(-100, 172.44) * mm, "radius": 0.8 * mm});
            skCircle(sketch, "E45.0.35.6", {"center": v(-100, 167.44) * mm, "radius": 0.8 * mm});
            skCircle(sketch, "E45.0.35.7", {"center": v(-100, 162.44) * mm, "radius": 0.8 * mm});
            skCircle(sketch, "E45.0.35.8", {"center": v(-100, 157.44) * mm, "radius": 0.8 * mm});
            skCircle(sketch, "E45.0.35.9", {"center": v(-100, 152.44) * mm, "radius": 0.8 * mm});
            skCircle(sketch, "E45.0.35.10", {"center": v(-100, 147.44) * mm, "radius": 0.8 * mm});
            skCircle(sketch, "E45.0.35.11", {"center": v(-100, 142.44) * mm, "radius": 0.8 * mm});
            skCircle(sketch, "E45.0.35.12", {"center": v(-100, 137.44) * mm, "radius": 0.8 * mm});
            skCircle(sketch, "E45.0.35.13", {"center": v(-100, 132.44) * mm, "radius": 0.8 * mm});
            skCircle(sketch, "E45.0.35.14", {"center": v(-100, 127.44) * mm, "radius": 0.8 * mm});
            skCircle(sketch, "E45.0.35.15", {"center": v(-100, 122.44) * mm, "radius": 0.8 * mm});
            skCircle(sketch, "E45.0.35.16", {"center": v(-100, 117.44) * mm, "radius": 0.8 * mm});
            skCircle(sketch, "E45.0.35.17", {"center": v(-100, 112.44) * mm, "radius": 0.8 * mm});
            skCircle(sketch, "E45.0.35.18", {"center": v(-100, 107.44) * mm, "radius": 0.8 * mm});
            skCircle(sketch, "E45.0.35.19", {"center": v(-100, 102.44) * mm, "radius": 0.8 * mm});
            skCircle(sketch, "E45.0.35.20", {"center": v(-100, 97.44) * mm, "radius": 0.8 * mm});
            skCircle(sketch, "E45.0.35.21", {"center": v(-100, 92.44) * mm, "radius": 0.8 * mm});
            skCircle(sketch, "E45.0.35.22", {"center": v(-100, 87.44) * mm, "radius": 0.8 * mm});
            skCircle(sketch, "E45.0.35.23", {"center": v(-100, 82.44) * mm, "radius": 0.8 * mm});
            skCircle(sketch, "E45.0.35.24", {"center": v(-100, 77.44) * mm, "radius": 0.8 * mm});
            skCircle(sketch, "E45.0.35.25", {"center": v(-100, 72.44) * mm, "radius": 0.8 * mm});
            skCircle(sketch, "E45.0.35.26", {"center": v(-100, 67.44) * mm, "radius": 0.8 * mm});
            skCircle(sketch, "E45.0.35.27", {"center": v(-100, 62.44) * mm, "radius": 0.8 * mm});
            skCircle(sketch, "E45.0.35.28", {"center": v(-100, 57.44) * mm, "radius": 0.8 * mm});
            skCircle(sketch, "E45.0.35.29", {"center": v(-100, 52.44) * mm, "radius": 0.8 * mm});
            skCircle(sketch, "E45.0.36.2", {"center": v(-105, 187.44) * mm, "radius": 0.8 * mm});
            skCircle(sketch, "E45.0.36.3", {"center": v(-105, 182.44) * mm, "radius": 0.8 * mm});
            skCircle(sketch, "E45.0.36.4", {"center": v(-105, 177.44) * mm, "radius": 0.8 * mm});
            skCircle(sketch, "E45.0.36.5", {"center": v(-105, 172.44) * mm, "radius": 0.8 * mm});
            skCircle(sketch, "E45.0.36.6", {"center": v(-105, 167.44) * mm, "radius": 0.8 * mm});
            skCircle(sketch, "E45.0.36.7", {"center": v(-105, 162.44) * mm, "radius": 0.8 * mm});
            skCircle(sketch, "E45.0.36.8", {"center": v(-105, 157.44) * mm, "radius": 0.8 * mm});
            skCircle(sketch, "E45.0.36.9", {"center": v(-105, 152.44) * mm, "radius": 0.8 * mm});
            skCircle(sketch, "E45.0.36.10", {"center": v(-105, 147.44) * mm, "radius": 0.8 * mm});
            skCircle(sketch, "E45.0.36.11", {"center": v(-105, 142.44) * mm, "radius": 0.8 * mm});
            skCircle(sketch, "E45.0.36.12", {"center": v(-105, 137.44) * mm, "radius": 0.8 * mm});
            skCircle(sketch, "E45.0.36.13", {"center": v(-105, 132.44) * mm, "radius": 0.8 * mm});
            skCircle(sketch, "E45.0.36.14", {"center": v(-105, 127.44) * mm, "radius": 0.8 * mm});
            skCircle(sketch, "E45.0.36.15", {"center": v(-105, 122.44) * mm, "radius": 0.8 * mm});
            skCircle(sketch, "E45.0.36.16", {"center": v(-105, 117.44) * mm, "radius": 0.8 * mm});
            skCircle(sketch, "E45.0.36.17", {"center": v(-105, 112.44) * mm, "radius": 0.8 * mm});
            skCircle(sketch, "E45.0.36.18", {"center": v(-105, 107.44) * mm, "radius": 0.8 * mm});
            skCircle(sketch, "E45.0.36.19", {"center": v(-105, 102.44) * mm, "radius": 0.8 * mm});
            skCircle(sketch, "E45.0.36.20", {"center": v(-105, 97.44) * mm, "radius": 0.8 * mm});
            skCircle(sketch, "E45.0.36.21", {"center": v(-105, 92.44) * mm, "radius": 0.8 * mm});
            skCircle(sketch, "E45.0.36.22", {"center": v(-105, 87.44) * mm, "radius": 0.8 * mm});
            skCircle(sketch, "E45.0.36.23", {"center": v(-105, 82.44) * mm, "radius": 0.8 * mm});
            skCircle(sketch, "E45.0.36.24", {"center": v(-105, 77.44) * mm, "radius": 0.8 * mm});
            skCircle(sketch, "E45.0.36.25", {"center": v(-105, 72.44) * mm, "radius": 0.8 * mm});
            skCircle(sketch, "E45.0.36.26", {"center": v(-105, 67.44) * mm, "radius": 0.8 * mm});
            skCircle(sketch, "E45.0.36.27", {"center": v(-105, 62.44) * mm, "radius": 0.8 * mm});
            skCircle(sketch, "E45.0.36.28", {"center": v(-105, 57.44) * mm, "radius": 0.8 * mm});
            skCircle(sketch, "E45.0.36.29", {"center": v(-105, 52.44) * mm, "radius": 0.8 * mm});
            skCircle(sketch, "E45.0.37.2", {"center": v(-110, 187.44) * mm, "radius": 0.8 * mm});
            skCircle(sketch, "E45.0.37.3", {"center": v(-110, 182.44) * mm, "radius": 0.8 * mm});
            skCircle(sketch, "E45.0.37.4", {"center": v(-110, 177.44) * mm, "radius": 0.8 * mm});
            skCircle(sketch, "E45.0.37.5", {"center": v(-110, 172.44) * mm, "radius": 0.8 * mm});
            skCircle(sketch, "E45.0.37.6", {"center": v(-110, 167.44) * mm, "radius": 0.8 * mm});
            skCircle(sketch, "E45.0.37.7", {"center": v(-110, 162.44) * mm, "radius": 0.8 * mm});
            skCircle(sketch, "E45.0.37.8", {"center": v(-110, 157.44) * mm, "radius": 0.8 * mm});
            skCircle(sketch, "E45.0.37.9", {"center": v(-110, 152.44) * mm, "radius": 0.8 * mm});
            skCircle(sketch, "E45.0.37.10", {"center": v(-110, 147.44) * mm, "radius": 0.8 * mm});
            skCircle(sketch, "E45.0.37.11", {"center": v(-110, 142.44) * mm, "radius": 0.8 * mm});
            skCircle(sketch, "E45.0.37.12", {"center": v(-110, 137.44) * mm, "radius": 0.8 * mm});
            skCircle(sketch, "E45.0.37.13", {"center": v(-110, 132.44) * mm, "radius": 0.8 * mm});
            skCircle(sketch, "E45.0.37.14", {"center": v(-110, 127.44) * mm, "radius": 0.8 * mm});
            skCircle(sketch, "E45.0.37.15", {"center": v(-110, 122.44) * mm, "radius": 0.8 * mm});
            skCircle(sketch, "E45.0.37.16", {"center": v(-110, 117.44) * mm, "radius": 0.8 * mm});
            skCircle(sketch, "E45.0.37.17", {"center": v(-110, 112.44) * mm, "radius": 0.8 * mm});
            skCircle(sketch, "E45.0.37.18", {"center": v(-110, 107.44) * mm, "radius": 0.8 * mm});
            skCircle(sketch, "E45.0.37.19", {"center": v(-110, 102.44) * mm, "radius": 0.8 * mm});
            skCircle(sketch, "E45.0.37.20", {"center": v(-110, 97.44) * mm, "radius": 0.8 * mm});
            skCircle(sketch, "E45.0.37.21", {"center": v(-110, 92.44) * mm, "radius": 0.8 * mm});
            skCircle(sketch, "E45.0.37.22", {"center": v(-110, 87.44) * mm, "radius": 0.8 * mm});
            skCircle(sketch, "E45.0.37.23", {"center": v(-110, 82.44) * mm, "radius": 0.8 * mm});
            skCircle(sketch, "E45.0.37.24", {"center": v(-110, 77.44) * mm, "radius": 0.8 * mm});
            skCircle(sketch, "E45.0.37.25", {"center": v(-110, 72.44) * mm, "radius": 0.8 * mm});
            skCircle(sketch, "E45.0.37.26", {"center": v(-110, 67.44) * mm, "radius": 0.8 * mm});
            skCircle(sketch, "E45.0.37.27", {"center": v(-110, 62.44) * mm, "radius": 0.8 * mm});
            skCircle(sketch, "E45.0.37.28", {"center": v(-110, 57.44) * mm, "radius": 0.8 * mm});
            skCircle(sketch, "E45.0.37.29", {"center": v(-110, 52.44) * mm, "radius": 0.8 * mm});
            skCircle(sketch, "E45.0.38.2", {"center": v(-115, 187.44) * mm, "radius": 0.8 * mm});
            skCircle(sketch, "E45.0.38.3", {"center": v(-115, 182.44) * mm, "radius": 0.8 * mm});
            skCircle(sketch, "E45.0.38.4", {"center": v(-115, 177.44) * mm, "radius": 0.8 * mm});
            skCircle(sketch, "E45.0.38.5", {"center": v(-115, 172.44) * mm, "radius": 0.8 * mm});
            skCircle(sketch, "E45.0.38.6", {"center": v(-115, 167.44) * mm, "radius": 0.8 * mm});
            skCircle(sketch, "E45.0.38.7", {"center": v(-115, 162.44) * mm, "radius": 0.8 * mm});
            skCircle(sketch, "E45.0.38.8", {"center": v(-115, 157.44) * mm, "radius": 0.8 * mm});
            skCircle(sketch, "E45.0.38.9", {"center": v(-115, 152.44) * mm, "radius": 0.8 * mm});
            skCircle(sketch, "E45.0.38.10", {"center": v(-115, 147.44) * mm, "radius": 0.8 * mm});
            skCircle(sketch, "E45.0.38.11", {"center": v(-115, 142.44) * mm, "radius": 0.8 * mm});
            skCircle(sketch, "E45.0.38.12", {"center": v(-115, 137.44) * mm, "radius": 0.8 * mm});
            skCircle(sketch, "E45.0.38.13", {"center": v(-115, 132.44) * mm, "radius": 0.8 * mm});
            skCircle(sketch, "E45.0.38.14", {"center": v(-115, 127.44) * mm, "radius": 0.8 * mm});
            skCircle(sketch, "E45.0.38.15", {"center": v(-115, 122.44) * mm, "radius": 0.8 * mm});
            skCircle(sketch, "E45.0.38.16", {"center": v(-115, 117.44) * mm, "radius": 0.8 * mm});
            skCircle(sketch, "E45.0.38.17", {"center": v(-115, 112.44) * mm, "radius": 0.8 * mm});
            skCircle(sketch, "E45.0.38.18", {"center": v(-115, 107.44) * mm, "radius": 0.8 * mm});
            skCircle(sketch, "E45.0.38.19", {"center": v(-115, 102.44) * mm, "radius": 0.8 * mm});
            skCircle(sketch, "E45.0.38.20", {"center": v(-115, 97.44) * mm, "radius": 0.8 * mm});
            skCircle(sketch, "E45.0.38.21", {"center": v(-115, 92.44) * mm, "radius": 0.8 * mm});
            skCircle(sketch, "E45.0.38.22", {"center": v(-115, 87.44) * mm, "radius": 0.8 * mm});
            skCircle(sketch, "E45.0.38.23", {"center": v(-115, 82.44) * mm, "radius": 0.8 * mm});
            skCircle(sketch, "E45.0.38.24", {"center": v(-115, 77.44) * mm, "radius": 0.8 * mm});
            skCircle(sketch, "E45.0.38.25", {"center": v(-115, 72.44) * mm, "radius": 0.8 * mm});
            skCircle(sketch, "E45.0.38.26", {"center": v(-115, 67.44) * mm, "radius": 0.8 * mm});
            skCircle(sketch, "E45.0.38.27", {"center": v(-115, 62.44) * mm, "radius": 0.8 * mm});
            skCircle(sketch, "E45.0.38.28", {"center": v(-115, 57.44) * mm, "radius": 0.8 * mm});
            skCircle(sketch, "E45.0.38.29", {"center": v(-115, 52.44) * mm, "radius": 0.8 * mm});
            skCircle(sketch, "E45.0.39.2", {"center": v(-120, 187.44) * mm, "radius": 0.8 * mm});
            skCircle(sketch, "E45.0.39.3", {"center": v(-120, 182.44) * mm, "radius": 0.8 * mm});
            skCircle(sketch, "E45.0.39.4", {"center": v(-120, 177.44) * mm, "radius": 0.8 * mm});
            skCircle(sketch, "E45.0.39.5", {"center": v(-120, 172.44) * mm, "radius": 0.8 * mm});
            skCircle(sketch, "E45.0.39.6", {"center": v(-120, 167.44) * mm, "radius": 0.8 * mm});
            skCircle(sketch, "E45.0.39.7", {"center": v(-120, 162.44) * mm, "radius": 0.8 * mm});
            skCircle(sketch, "E45.0.39.8", {"center": v(-120, 157.44) * mm, "radius": 0.8 * mm});
            skCircle(sketch, "E45.0.39.9", {"center": v(-120, 152.44) * mm, "radius": 0.8 * mm});
            skCircle(sketch, "E45.0.39.10", {"center": v(-120, 147.44) * mm, "radius": 0.8 * mm});
            skCircle(sketch, "E45.0.39.11", {"center": v(-120, 142.44) * mm, "radius": 0.8 * mm});
            skCircle(sketch, "E45.0.39.12", {"center": v(-120, 137.44) * mm, "radius": 0.8 * mm});
            skCircle(sketch, "E45.0.39.13", {"center": v(-120, 132.44) * mm, "radius": 0.8 * mm});
            skCircle(sketch, "E45.0.39.14", {"center": v(-120, 127.44) * mm, "radius": 0.8 * mm});
            skCircle(sketch, "E45.0.39.15", {"center": v(-120, 122.44) * mm, "radius": 0.8 * mm});
            skCircle(sketch, "E45.0.39.16", {"center": v(-120, 117.44) * mm, "radius": 0.8 * mm});
            skCircle(sketch, "E45.0.39.17", {"center": v(-120, 112.44) * mm, "radius": 0.8 * mm});
            skCircle(sketch, "E45.0.39.18", {"center": v(-120, 107.44) * mm, "radius": 0.8 * mm});
            skCircle(sketch, "E45.0.39.19", {"center": v(-120, 102.44) * mm, "radius": 0.8 * mm});
            skCircle(sketch, "E45.0.39.20", {"center": v(-120, 97.44) * mm, "radius": 0.8 * mm});
            skCircle(sketch, "E45.0.39.21", {"center": v(-120, 92.44) * mm, "radius": 0.8 * mm});
            skCircle(sketch, "E45.0.39.22", {"center": v(-120, 87.44) * mm, "radius": 0.8 * mm});
            skCircle(sketch, "E45.0.39.23", {"center": v(-120, 82.44) * mm, "radius": 0.8 * mm});
            skCircle(sketch, "E45.0.39.24", {"center": v(-120, 77.44) * mm, "radius": 0.8 * mm});
            skCircle(sketch, "E45.0.39.25", {"center": v(-120, 72.44) * mm, "radius": 0.8 * mm});
            skCircle(sketch, "E45.0.39.26", {"center": v(-120, 67.44) * mm, "radius": 0.8 * mm});
            skCircle(sketch, "E45.0.39.27", {"center": v(-120, 62.44) * mm, "radius": 0.8 * mm});
            skCircle(sketch, "E45.0.39.28", {"center": v(-120, 57.44) * mm, "radius": 0.8 * mm});
            skCircle(sketch, "E45.0.39.29", {"center": v(-120, 52.44) * mm, "radius": 0.8 * mm});
            skCircle(sketch, "E45.0.40.2", {"center": v(-125, 187.44) * mm, "radius": 0.8 * mm});
            skCircle(sketch, "E45.0.40.3", {"center": v(-125, 182.44) * mm, "radius": 0.8 * mm});
            skCircle(sketch, "E45.0.40.4", {"center": v(-125, 177.44) * mm, "radius": 0.8 * mm});
            skCircle(sketch, "E45.0.40.5", {"center": v(-125, 172.44) * mm, "radius": 0.8 * mm});
            skCircle(sketch, "E45.0.40.6", {"center": v(-125, 167.44) * mm, "radius": 0.8 * mm});
            skCircle(sketch, "E45.0.40.7", {"center": v(-125, 162.44) * mm, "radius": 0.8 * mm});
            skCircle(sketch, "E45.0.40.8", {"center": v(-125, 157.44) * mm, "radius": 0.8 * mm});
            skCircle(sketch, "E45.0.40.9", {"center": v(-125, 152.44) * mm, "radius": 0.8 * mm});
            skCircle(sketch, "E45.0.40.10", {"center": v(-125, 147.44) * mm, "radius": 0.8 * mm});
            skCircle(sketch, "E45.0.40.11", {"center": v(-125, 142.44) * mm, "radius": 0.8 * mm});
            skCircle(sketch, "E45.0.40.12", {"center": v(-125, 137.44) * mm, "radius": 0.8 * mm});
            skCircle(sketch, "E45.0.40.13", {"center": v(-125, 132.44) * mm, "radius": 0.8 * mm});
            skCircle(sketch, "E45.0.40.14", {"center": v(-125, 127.44) * mm, "radius": 0.8 * mm});
            skCircle(sketch, "E45.0.40.15", {"center": v(-125, 122.44) * mm, "radius": 0.8 * mm});
            skCircle(sketch, "E45.0.40.16", {"center": v(-125, 117.44) * mm, "radius": 0.8 * mm});
            skCircle(sketch, "E45.0.40.17", {"center": v(-125, 112.44) * mm, "radius": 0.8 * mm});
            skCircle(sketch, "E45.0.40.18", {"center": v(-125, 107.44) * mm, "radius": 0.8 * mm});
            skCircle(sketch, "E45.0.40.19", {"center": v(-125, 102.44) * mm, "radius": 0.8 * mm});
            skCircle(sketch, "E45.0.40.20", {"center": v(-125, 97.44) * mm, "radius": 0.8 * mm});
            skCircle(sketch, "E45.0.40.21", {"center": v(-125, 92.44) * mm, "radius": 0.8 * mm});
            skCircle(sketch, "E45.0.40.22", {"center": v(-125, 87.44) * mm, "radius": 0.8 * mm});
            skCircle(sketch, "E45.0.40.23", {"center": v(-125, 82.44) * mm, "radius": 0.8 * mm});
            skCircle(sketch, "E45.0.40.24", {"center": v(-125, 77.44) * mm, "radius": 0.8 * mm});
            skCircle(sketch, "E45.0.40.25", {"center": v(-125, 72.44) * mm, "radius": 0.8 * mm});
            skCircle(sketch, "E45.0.40.26", {"center": v(-125, 67.44) * mm, "radius": 0.8 * mm});
            skCircle(sketch, "E45.0.40.27", {"center": v(-125, 62.44) * mm, "radius": 0.8 * mm});
            skCircle(sketch, "E45.0.40.28", {"center": v(-125, 57.44) * mm, "radius": 0.8 * mm});
            skCircle(sketch, "E45.0.40.29", {"center": v(-125, 52.44) * mm, "radius": 0.8 * mm});
            skCircle(sketch, "E45.0.41.2", {"center": v(-130, 187.44) * mm, "radius": 0.8 * mm});
            skCircle(sketch, "E45.0.41.3", {"center": v(-130, 182.44) * mm, "radius": 0.8 * mm});
            skCircle(sketch, "E45.0.41.4", {"center": v(-130, 177.44) * mm, "radius": 0.8 * mm});
            skCircle(sketch, "E45.0.41.5", {"center": v(-130, 172.44) * mm, "radius": 0.8 * mm});
            skCircle(sketch, "E45.0.41.6", {"center": v(-130, 167.44) * mm, "radius": 0.8 * mm});
            skCircle(sketch, "E45.0.41.7", {"center": v(-130, 162.44) * mm, "radius": 0.8 * mm});
            skCircle(sketch, "E45.0.41.8", {"center": v(-130, 157.44) * mm, "radius": 0.8 * mm});
            skCircle(sketch, "E45.0.41.9", {"center": v(-130, 152.44) * mm, "radius": 0.8 * mm});
            skCircle(sketch, "E45.0.41.10", {"center": v(-130, 147.44) * mm, "radius": 0.8 * mm});
            skCircle(sketch, "E45.0.41.11", {"center": v(-130, 142.44) * mm, "radius": 0.8 * mm});
            skCircle(sketch, "E45.0.41.12", {"center": v(-130, 137.44) * mm, "radius": 0.8 * mm});
            skCircle(sketch, "E45.0.41.13", {"center": v(-130, 132.44) * mm, "radius": 0.8 * mm});
            skCircle(sketch, "E45.0.41.14", {"center": v(-130, 127.44) * mm, "radius": 0.8 * mm});
            skCircle(sketch, "E45.0.41.15", {"center": v(-130, 122.44) * mm, "radius": 0.8 * mm});
            skCircle(sketch, "E45.0.41.16", {"center": v(-130, 117.44) * mm, "radius": 0.8 * mm});
            skCircle(sketch, "E45.0.41.17", {"center": v(-130, 112.44) * mm, "radius": 0.8 * mm});
            skCircle(sketch, "E45.0.41.18", {"center": v(-130, 107.44) * mm, "radius": 0.8 * mm});
            skCircle(sketch, "E45.0.41.19", {"center": v(-130, 102.44) * mm, "radius": 0.8 * mm});
            skCircle(sketch, "E45.0.41.20", {"center": v(-130, 97.44) * mm, "radius": 0.8 * mm});
            skCircle(sketch, "E45.0.41.21", {"center": v(-130, 92.44) * mm, "radius": 0.8 * mm});
            skCircle(sketch, "E45.0.41.22", {"center": v(-130, 87.44) * mm, "radius": 0.8 * mm});
            skCircle(sketch, "E45.0.41.23", {"center": v(-130, 82.44) * mm, "radius": 0.8 * mm});
            skCircle(sketch, "E45.0.41.24", {"center": v(-130, 77.44) * mm, "radius": 0.8 * mm});
            skCircle(sketch, "E45.0.41.25", {"center": v(-130, 72.44) * mm, "radius": 0.8 * mm});
            skCircle(sketch, "E45.0.41.26", {"center": v(-130, 67.44) * mm, "radius": 0.8 * mm});
            skCircle(sketch, "E45.0.41.27", {"center": v(-130, 62.44) * mm, "radius": 0.8 * mm});
            skCircle(sketch, "E45.0.41.28", {"center": v(-130, 57.44) * mm, "radius": 0.8 * mm});
            skCircle(sketch, "E45.0.41.29", {"center": v(-130, 52.44) * mm, "radius": 0.8 * mm});
            skCircle(sketch, "E45.0.42.2", {"center": v(-135, 187.44) * mm, "radius": 0.8 * mm});
            skCircle(sketch, "E45.0.42.3", {"center": v(-135, 182.44) * mm, "radius": 0.8 * mm});
            skCircle(sketch, "E45.0.42.4", {"center": v(-135, 177.44) * mm, "radius": 0.8 * mm});
            skCircle(sketch, "E45.0.42.5", {"center": v(-135, 172.44) * mm, "radius": 0.8 * mm});
            skCircle(sketch, "E45.0.42.6", {"center": v(-135, 167.44) * mm, "radius": 0.8 * mm});
            skCircle(sketch, "E45.0.42.7", {"center": v(-135, 162.44) * mm, "radius": 0.8 * mm});
            skCircle(sketch, "E45.0.42.8", {"center": v(-135, 157.44) * mm, "radius": 0.8 * mm});
            skCircle(sketch, "E45.0.42.9", {"center": v(-135, 152.44) * mm, "radius": 0.8 * mm});
            skCircle(sketch, "E45.0.42.10", {"center": v(-135, 147.44) * mm, "radius": 0.8 * mm});
            skCircle(sketch, "E45.0.42.11", {"center": v(-135, 142.44) * mm, "radius": 0.8 * mm});
            skCircle(sketch, "E45.0.42.12", {"center": v(-135, 137.44) * mm, "radius": 0.8 * mm});
            skCircle(sketch, "E45.0.42.13", {"center": v(-135, 132.44) * mm, "radius": 0.8 * mm});
            skCircle(sketch, "E45.0.42.14", {"center": v(-135, 127.44) * mm, "radius": 0.8 * mm});
            skCircle(sketch, "E45.0.42.15", {"center": v(-135, 122.44) * mm, "radius": 0.8 * mm});
            skCircle(sketch, "E45.0.42.16", {"center": v(-135, 117.44) * mm, "radius": 0.8 * mm});
            skCircle(sketch, "E45.0.42.17", {"center": v(-135, 112.44) * mm, "radius": 0.8 * mm});
            skCircle(sketch, "E45.0.42.18", {"center": v(-135, 107.44) * mm, "radius": 0.8 * mm});
            skCircle(sketch, "E45.0.42.19", {"center": v(-135, 102.44) * mm, "radius": 0.8 * mm});
            skCircle(sketch, "E45.0.42.20", {"center": v(-135, 97.44) * mm, "radius": 0.8 * mm});
            skCircle(sketch, "E45.0.42.21", {"center": v(-135, 92.44) * mm, "radius": 0.8 * mm});
            skCircle(sketch, "E45.0.42.22", {"center": v(-135, 87.44) * mm, "radius": 0.8 * mm});
            skCircle(sketch, "E45.0.42.23", {"center": v(-135, 82.44) * mm, "radius": 0.8 * mm});
            skCircle(sketch, "E45.0.42.24", {"center": v(-135, 77.44) * mm, "radius": 0.8 * mm});
            skCircle(sketch, "E45.0.42.25", {"center": v(-135, 72.44) * mm, "radius": 0.8 * mm});
            skCircle(sketch, "E45.0.42.26", {"center": v(-135, 67.44) * mm, "radius": 0.8 * mm});
            skCircle(sketch, "E45.0.42.27", {"center": v(-135, 62.44) * mm, "radius": 0.8 * mm});
            skCircle(sketch, "E45.0.42.28", {"center": v(-135, 57.44) * mm, "radius": 0.8 * mm});
            skCircle(sketch, "E45.0.42.29", {"center": v(-135, 52.44) * mm, "radius": 0.8 * mm});
            skCircle(sketch, "E45.0.43.2", {"center": v(-140, 187.44) * mm, "radius": 0.8 * mm});
            skCircle(sketch, "E45.0.43.3", {"center": v(-140, 182.44) * mm, "radius": 0.8 * mm});
            skCircle(sketch, "E45.0.43.4", {"center": v(-140, 177.44) * mm, "radius": 0.8 * mm});
            skCircle(sketch, "E45.0.43.5", {"center": v(-140, 172.44) * mm, "radius": 0.8 * mm});
            skCircle(sketch, "E45.0.43.6", {"center": v(-140, 167.44) * mm, "radius": 0.8 * mm});
            skCircle(sketch, "E45.0.43.7", {"center": v(-140, 162.44) * mm, "radius": 0.8 * mm});
            skCircle(sketch, "E45.0.43.8", {"center": v(-140, 157.44) * mm, "radius": 0.8 * mm});
            skCircle(sketch, "E45.0.43.9", {"center": v(-140, 152.44) * mm, "radius": 0.8 * mm});
            skCircle(sketch, "E45.0.43.10", {"center": v(-140, 147.44) * mm, "radius": 0.8 * mm});
            skCircle(sketch, "E45.0.43.11", {"center": v(-140, 142.44) * mm, "radius": 0.8 * mm});
            skCircle(sketch, "E45.0.43.12", {"center": v(-140, 137.44) * mm, "radius": 0.8 * mm});
            skCircle(sketch, "E45.0.43.13", {"center": v(-140, 132.44) * mm, "radius": 0.8 * mm});
            skCircle(sketch, "E45.0.43.14", {"center": v(-140, 127.44) * mm, "radius": 0.8 * mm});
            skCircle(sketch, "E45.0.43.15", {"center": v(-140, 122.44) * mm, "radius": 0.8 * mm});
            skCircle(sketch, "E45.0.43.16", {"center": v(-140, 117.44) * mm, "radius": 0.8 * mm});
            skCircle(sketch, "E45.0.43.17", {"center": v(-140, 112.44) * mm, "radius": 0.8 * mm});
            skCircle(sketch, "E45.0.43.18", {"center": v(-140, 107.44) * mm, "radius": 0.8 * mm});
            skCircle(sketch, "E45.0.43.19", {"center": v(-140, 102.44) * mm, "radius": 0.8 * mm});
            skCircle(sketch, "E45.0.43.20", {"center": v(-140, 97.44) * mm, "radius": 0.8 * mm});
            skCircle(sketch, "E45.0.43.21", {"center": v(-140, 92.44) * mm, "radius": 0.8 * mm});
            skCircle(sketch, "E45.0.43.22", {"center": v(-140, 87.44) * mm, "radius": 0.8 * mm});
            skCircle(sketch, "E45.0.43.23", {"center": v(-140, 82.44) * mm, "radius": 0.8 * mm});
            skCircle(sketch, "E45.0.43.24", {"center": v(-140, 77.44) * mm, "radius": 0.8 * mm});
            skCircle(sketch, "E45.0.43.25", {"center": v(-140, 72.44) * mm, "radius": 0.8 * mm});
            skCircle(sketch, "E45.0.43.26", {"center": v(-140, 67.44) * mm, "radius": 0.8 * mm});
            skCircle(sketch, "E45.0.43.27", {"center": v(-140, 62.44) * mm, "radius": 0.8 * mm});
            skCircle(sketch, "E45.0.43.28", {"center": v(-140, 57.44) * mm, "radius": 0.8 * mm});
            skCircle(sketch, "E45.0.43.29", {"center": v(-140, 52.44) * mm, "radius": 0.8 * mm});
            skCircle(sketch, "E45.0.44.2", {"center": v(-145, 187.44) * mm, "radius": 0.8 * mm});
            skCircle(sketch, "E45.0.44.3", {"center": v(-145, 182.44) * mm, "radius": 0.8 * mm});
            skCircle(sketch, "E45.0.44.4", {"center": v(-145, 177.44) * mm, "radius": 0.8 * mm});
            skCircle(sketch, "E45.0.44.5", {"center": v(-145, 172.44) * mm, "radius": 0.8 * mm});
            skCircle(sketch, "E45.0.44.6", {"center": v(-145, 167.44) * mm, "radius": 0.8 * mm});
            skCircle(sketch, "E45.0.44.7", {"center": v(-145, 162.44) * mm, "radius": 0.8 * mm});
            skCircle(sketch, "E45.0.44.8", {"center": v(-145, 157.44) * mm, "radius": 0.8 * mm});
            skCircle(sketch, "E45.0.44.9", {"center": v(-145, 152.44) * mm, "radius": 0.8 * mm});
            skCircle(sketch, "E45.0.44.10", {"center": v(-145, 147.44) * mm, "radius": 0.8 * mm});
            skCircle(sketch, "E45.0.44.11", {"center": v(-145, 142.44) * mm, "radius": 0.8 * mm});
            skCircle(sketch, "E45.0.44.12", {"center": v(-145, 137.44) * mm, "radius": 0.8 * mm});
            skCircle(sketch, "E45.0.44.13", {"center": v(-145, 132.44) * mm, "radius": 0.8 * mm});
            skCircle(sketch, "E45.0.44.14", {"center": v(-145, 127.44) * mm, "radius": 0.8 * mm});
            skCircle(sketch, "E45.0.44.15", {"center": v(-145, 122.44) * mm, "radius": 0.8 * mm});
            skCircle(sketch, "E45.0.44.16", {"center": v(-145, 117.44) * mm, "radius": 0.8 * mm});
            skCircle(sketch, "E45.0.44.17", {"center": v(-145, 112.44) * mm, "radius": 0.8 * mm});
            skCircle(sketch, "E45.0.44.18", {"center": v(-145, 107.44) * mm, "radius": 0.8 * mm});
            skCircle(sketch, "E45.0.44.19", {"center": v(-145, 102.44) * mm, "radius": 0.8 * mm});
            skCircle(sketch, "E45.0.44.20", {"center": v(-145, 97.44) * mm, "radius": 0.8 * mm});
            skCircle(sketch, "E45.0.44.21", {"center": v(-145, 92.44) * mm, "radius": 0.8 * mm});
            skCircle(sketch, "E45.0.44.22", {"center": v(-145, 87.44) * mm, "radius": 0.8 * mm});
            skCircle(sketch, "E45.0.44.23", {"center": v(-145, 82.44) * mm, "radius": 0.8 * mm});
            skCircle(sketch, "E45.0.44.24", {"center": v(-145, 77.44) * mm, "radius": 0.8 * mm});
            skCircle(sketch, "E45.0.44.25", {"center": v(-145, 72.44) * mm, "radius": 0.8 * mm});
            skCircle(sketch, "E45.0.44.26", {"center": v(-145, 67.44) * mm, "radius": 0.8 * mm});
            skCircle(sketch, "E45.0.44.27", {"center": v(-145, 62.44) * mm, "radius": 0.8 * mm});
            skCircle(sketch, "E45.0.44.28", {"center": v(-145, 57.44) * mm, "radius": 0.8 * mm});
            skCircle(sketch, "E45.0.44.29", {"center": v(-145, 52.44) * mm, "radius": 0.8 * mm});
            skCircle(sketch, "E45.0.45.2", {"center": v(-150, 187.44) * mm, "radius": 0.8 * mm});
            skCircle(sketch, "E45.0.45.3", {"center": v(-150, 182.44) * mm, "radius": 0.8 * mm});
            skCircle(sketch, "E45.0.45.4", {"center": v(-150, 177.44) * mm, "radius": 0.8 * mm});
            skCircle(sketch, "E45.0.45.5", {"center": v(-150, 172.44) * mm, "radius": 0.8 * mm});
            skCircle(sketch, "E45.0.45.6", {"center": v(-150, 167.44) * mm, "radius": 0.8 * mm});
            skCircle(sketch, "E45.0.45.7", {"center": v(-150, 162.44) * mm, "radius": 0.8 * mm});
            skCircle(sketch, "E45.0.45.8", {"center": v(-150, 157.44) * mm, "radius": 0.8 * mm});
            skCircle(sketch, "E45.0.45.9", {"center": v(-150, 152.44) * mm, "radius": 0.8 * mm});
            skCircle(sketch, "E45.0.45.10", {"center": v(-150, 147.44) * mm, "radius": 0.8 * mm});
            skCircle(sketch, "E45.0.45.11", {"center": v(-150, 142.44) * mm, "radius": 0.8 * mm});
            skCircle(sketch, "E45.0.45.12", {"center": v(-150, 137.44) * mm, "radius": 0.8 * mm});
            skCircle(sketch, "E45.0.45.13", {"center": v(-150, 132.44) * mm, "radius": 0.8 * mm});
            skCircle(sketch, "E45.0.45.14", {"center": v(-150, 127.44) * mm, "radius": 0.8 * mm});
            skCircle(sketch, "E45.0.45.15", {"center": v(-150, 122.44) * mm, "radius": 0.8 * mm});
            skCircle(sketch, "E45.0.45.16", {"center": v(-150, 117.44) * mm, "radius": 0.8 * mm});
            skCircle(sketch, "E45.0.45.17", {"center": v(-150, 112.44) * mm, "radius": 0.8 * mm});
            skCircle(sketch, "E45.0.45.18", {"center": v(-150, 107.44) * mm, "radius": 0.8 * mm});
            skCircle(sketch, "E45.0.45.19", {"center": v(-150, 102.44) * mm, "radius": 0.8 * mm});
            skCircle(sketch, "E45.0.45.20", {"center": v(-150, 97.44) * mm, "radius": 0.8 * mm});
            skCircle(sketch, "E45.0.45.21", {"center": v(-150, 92.44) * mm, "radius": 0.8 * mm});
            skCircle(sketch, "E45.0.45.22", {"center": v(-150, 87.44) * mm, "radius": 0.8 * mm});
            skCircle(sketch, "E45.0.45.23", {"center": v(-150, 82.44) * mm, "radius": 0.8 * mm});
            skCircle(sketch, "E45.0.45.24", {"center": v(-150, 77.44) * mm, "radius": 0.8 * mm});
            skCircle(sketch, "E45.0.45.25", {"center": v(-150, 72.44) * mm, "radius": 0.8 * mm});
            skCircle(sketch, "E45.0.45.26", {"center": v(-150, 67.44) * mm, "radius": 0.8 * mm});
            skCircle(sketch, "E45.0.45.27", {"center": v(-150, 62.44) * mm, "radius": 0.8 * mm});
            skCircle(sketch, "E45.0.45.28", {"center": v(-150, 57.44) * mm, "radius": 0.8 * mm});
            skCircle(sketch, "E45.0.45.29", {"center": v(-150, 52.44) * mm, "radius": 0.8 * mm});
            skCircle(sketch, "E45.0.46.2", {"center": v(-155, 187.44) * mm, "radius": 0.8 * mm});
            skCircle(sketch, "E45.0.46.3", {"center": v(-155, 182.44) * mm, "radius": 0.8 * mm});
            skCircle(sketch, "E45.0.46.4", {"center": v(-155, 177.44) * mm, "radius": 0.8 * mm});
            skCircle(sketch, "E45.0.46.5", {"center": v(-155, 172.44) * mm, "radius": 0.8 * mm});
            skCircle(sketch, "E45.0.46.6", {"center": v(-155, 167.44) * mm, "radius": 0.8 * mm});
            skCircle(sketch, "E45.0.46.7", {"center": v(-155, 162.44) * mm, "radius": 0.8 * mm});
            skCircle(sketch, "E45.0.46.8", {"center": v(-155, 157.44) * mm, "radius": 0.8 * mm});
            skCircle(sketch, "E45.0.46.9", {"center": v(-155, 152.44) * mm, "radius": 0.8 * mm});
            skCircle(sketch, "E45.0.46.10", {"center": v(-155, 147.44) * mm, "radius": 0.8 * mm});
            skCircle(sketch, "E45.0.46.11", {"center": v(-155, 142.44) * mm, "radius": 0.8 * mm});
            skCircle(sketch, "E45.0.46.12", {"center": v(-155, 137.44) * mm, "radius": 0.8 * mm});
            skCircle(sketch, "E45.0.46.13", {"center": v(-155, 132.44) * mm, "radius": 0.8 * mm});
            skCircle(sketch, "E45.0.46.14", {"center": v(-155, 127.44) * mm, "radius": 0.8 * mm});
            skCircle(sketch, "E45.0.46.15", {"center": v(-155, 122.44) * mm, "radius": 0.8 * mm});
            skCircle(sketch, "E45.0.46.16", {"center": v(-155, 117.44) * mm, "radius": 0.8 * mm});
            skCircle(sketch, "E45.0.46.17", {"center": v(-155, 112.44) * mm, "radius": 0.8 * mm});
            skCircle(sketch, "E45.0.46.18", {"center": v(-155, 107.44) * mm, "radius": 0.8 * mm});
            skCircle(sketch, "E45.0.46.19", {"center": v(-155, 102.44) * mm, "radius": 0.8 * mm});
            skCircle(sketch, "E45.0.46.20", {"center": v(-155, 97.44) * mm, "radius": 0.8 * mm});
            skCircle(sketch, "E45.0.46.21", {"center": v(-155, 92.44) * mm, "radius": 0.8 * mm});
            skCircle(sketch, "E45.0.46.22", {"center": v(-155, 87.44) * mm, "radius": 0.8 * mm});
            skCircle(sketch, "E45.0.46.23", {"center": v(-155, 82.44) * mm, "radius": 0.8 * mm});
            skCircle(sketch, "E45.0.46.24", {"center": v(-155, 77.44) * mm, "radius": 0.8 * mm});
            skCircle(sketch, "E45.0.46.25", {"center": v(-155, 72.44) * mm, "radius": 0.8 * mm});
            skCircle(sketch, "E45.0.46.26", {"center": v(-155, 67.44) * mm, "radius": 0.8 * mm});
            skCircle(sketch, "E45.0.46.27", {"center": v(-155, 62.44) * mm, "radius": 0.8 * mm});
            skCircle(sketch, "E45.0.46.28", {"center": v(-155, 57.44) * mm, "radius": 0.8 * mm});
            skCircle(sketch, "E45.0.46.29", {"center": v(-155, 52.44) * mm, "radius": 0.8 * mm});
            skCircle(sketch, "E45.0.47.2", {"center": v(-160, 187.44) * mm, "radius": 0.8 * mm});
            skCircle(sketch, "E45.0.47.3", {"center": v(-160, 182.44) * mm, "radius": 0.8 * mm});
            skCircle(sketch, "E45.0.47.4", {"center": v(-160, 177.44) * mm, "radius": 0.8 * mm});
            skCircle(sketch, "E45.0.47.5", {"center": v(-160, 172.44) * mm, "radius": 0.8 * mm});
            skCircle(sketch, "E45.0.47.6", {"center": v(-160, 167.44) * mm, "radius": 0.8 * mm});
            skCircle(sketch, "E45.0.47.7", {"center": v(-160, 162.44) * mm, "radius": 0.8 * mm});
            skCircle(sketch, "E45.0.47.8", {"center": v(-160, 157.44) * mm, "radius": 0.8 * mm});
            skCircle(sketch, "E45.0.47.9", {"center": v(-160, 152.44) * mm, "radius": 0.8 * mm});
            skCircle(sketch, "E45.0.47.10", {"center": v(-160, 147.44) * mm, "radius": 0.8 * mm});
            skCircle(sketch, "E45.0.47.11", {"center": v(-160, 142.44) * mm, "radius": 0.8 * mm});
            skCircle(sketch, "E45.0.47.12", {"center": v(-160, 137.44) * mm, "radius": 0.8 * mm});
            skCircle(sketch, "E45.0.47.13", {"center": v(-160, 132.44) * mm, "radius": 0.8 * mm});
            skCircle(sketch, "E45.0.47.14", {"center": v(-160, 127.44) * mm, "radius": 0.8 * mm});
            skCircle(sketch, "E45.0.47.15", {"center": v(-160, 122.44) * mm, "radius": 0.8 * mm});
            skCircle(sketch, "E45.0.47.16", {"center": v(-160, 117.44) * mm, "radius": 0.8 * mm});
            skCircle(sketch, "E45.0.47.17", {"center": v(-160, 112.44) * mm, "radius": 0.8 * mm});
            skCircle(sketch, "E45.0.47.18", {"center": v(-160, 107.44) * mm, "radius": 0.8 * mm});
            skCircle(sketch, "E45.0.47.19", {"center": v(-160, 102.44) * mm, "radius": 0.8 * mm});
            skCircle(sketch, "E45.0.47.20", {"center": v(-160, 97.44) * mm, "radius": 0.8 * mm});
            skCircle(sketch, "E45.0.47.21", {"center": v(-160, 92.44) * mm, "radius": 0.8 * mm});
            skCircle(sketch, "E45.0.47.22", {"center": v(-160, 87.44) * mm, "radius": 0.8 * mm});
            skCircle(sketch, "E45.0.47.23", {"center": v(-160, 82.44) * mm, "radius": 0.8 * mm});
            skCircle(sketch, "E45.0.47.24", {"center": v(-160, 77.44) * mm, "radius": 0.8 * mm});
            skCircle(sketch, "E45.0.47.25", {"center": v(-160, 72.44) * mm, "radius": 0.8 * mm});
            skCircle(sketch, "E45.0.47.26", {"center": v(-160, 67.44) * mm, "radius": 0.8 * mm});
            skCircle(sketch, "E45.0.47.27", {"center": v(-160, 62.44) * mm, "radius": 0.8 * mm});
            skCircle(sketch, "E45.0.47.28", {"center": v(-160, 57.44) * mm, "radius": 0.8 * mm});
            skCircle(sketch, "E45.0.47.29", {"center": v(-160, 52.44) * mm, "radius": 0.8 * mm});
            skCircle(sketch, "E45.0.48.2", {"center": v(-165, 187.44) * mm, "radius": 0.8 * mm});
            skCircle(sketch, "E45.0.48.3", {"center": v(-165, 182.44) * mm, "radius": 0.8 * mm});
            skCircle(sketch, "E45.0.48.4", {"center": v(-165, 177.44) * mm, "radius": 0.8 * mm});
            skCircle(sketch, "E45.0.48.5", {"center": v(-165, 172.44) * mm, "radius": 0.8 * mm});
            skCircle(sketch, "E45.0.48.6", {"center": v(-165, 167.44) * mm, "radius": 0.8 * mm});
            skCircle(sketch, "E45.0.48.7", {"center": v(-165, 162.44) * mm, "radius": 0.8 * mm});
            skCircle(sketch, "E45.0.48.8", {"center": v(-165, 157.44) * mm, "radius": 0.8 * mm});
            skCircle(sketch, "E45.0.48.9", {"center": v(-165, 152.44) * mm, "radius": 0.8 * mm});
            skCircle(sketch, "E45.0.48.10", {"center": v(-165, 147.44) * mm, "radius": 0.8 * mm});
            skCircle(sketch, "E45.0.48.11", {"center": v(-165, 142.44) * mm, "radius": 0.8 * mm});
            skCircle(sketch, "E45.0.48.12", {"center": v(-165, 137.44) * mm, "radius": 0.8 * mm});
            skCircle(sketch, "E45.0.48.13", {"center": v(-165, 132.44) * mm, "radius": 0.8 * mm});
            skCircle(sketch, "E45.0.48.14", {"center": v(-165, 127.44) * mm, "radius": 0.8 * mm});
            skCircle(sketch, "E45.0.48.15", {"center": v(-165, 122.44) * mm, "radius": 0.8 * mm});
            skCircle(sketch, "E45.0.48.16", {"center": v(-165, 117.44) * mm, "radius": 0.8 * mm});
            skCircle(sketch, "E45.0.48.17", {"center": v(-165, 112.44) * mm, "radius": 0.8 * mm});
            skCircle(sketch, "E45.0.48.18", {"center": v(-165, 107.44) * mm, "radius": 0.8 * mm});
            skCircle(sketch, "E45.0.48.19", {"center": v(-165, 102.44) * mm, "radius": 0.8 * mm});
            skCircle(sketch, "E45.0.48.20", {"center": v(-165, 97.44) * mm, "radius": 0.8 * mm});
            skCircle(sketch, "E45.0.48.21", {"center": v(-165, 92.44) * mm, "radius": 0.8 * mm});
            skCircle(sketch, "E45.0.48.22", {"center": v(-165, 87.44) * mm, "radius": 0.8 * mm});
            skCircle(sketch, "E45.0.48.23", {"center": v(-165, 82.44) * mm, "radius": 0.8 * mm});
            skCircle(sketch, "E45.0.48.24", {"center": v(-165, 77.44) * mm, "radius": 0.8 * mm});
            skCircle(sketch, "E45.0.48.25", {"center": v(-165, 72.44) * mm, "radius": 0.8 * mm});
            skCircle(sketch, "E45.0.48.26", {"center": v(-165, 67.44) * mm, "radius": 0.8 * mm});
            skCircle(sketch, "E45.0.48.27", {"center": v(-165, 62.44) * mm, "radius": 0.8 * mm});
            skCircle(sketch, "E45.0.48.28", {"center": v(-165, 57.44) * mm, "radius": 0.8 * mm});
            skCircle(sketch, "E45.0.48.29", {"center": v(-165, 52.44) * mm, "radius": 0.8 * mm});
            skCircle(sketch, "E46.0.0.30", {"center": v(75, 47.44) * mm, "radius": 0.8 * mm});
            skCircle(sketch, "E46.0.0.31", {"center": v(75, 42.44) * mm, "radius": 0.8 * mm});
            skCircle(sketch, "E46.0.0.32", {"center": v(75, 37.44) * mm, "radius": 0.8 * mm});
            skCircle(sketch, "E46.0.0.33", {"center": v(75, 32.44) * mm, "radius": 0.8 * mm});
            skCircle(sketch, "E46.0.0.34", {"center": v(75, 27.44) * mm, "radius": 0.8 * mm});
            skCircle(sketch, "E46.0.0.35", {"center": v(75, 22.44) * mm, "radius": 0.8 * mm});
            skCircle(sketch, "E46.0.0.36", {"center": v(75, 17.44) * mm, "radius": 0.8 * mm});
            skCircle(sketch, "E46.0.0.37", {"center": v(75, 12.44) * mm, "radius": 0.8 * mm});
            skCircle(sketch, "E46.0.0.38", {"center": v(75, 7.44) * mm, "radius": 0.8 * mm});
            skCircle(sketch, "E46.0.0.39", {"center": v(75, 2.44) * mm, "radius": 0.8 * mm});
            skCircle(sketch, "E46.0.1.30", {"center": v(70, 47.44) * mm, "radius": 0.8 * mm});
            skCircle(sketch, "E46.0.1.31", {"center": v(70, 42.44) * mm, "radius": 0.8 * mm});
            skCircle(sketch, "E46.0.1.32", {"center": v(70, 37.44) * mm, "radius": 0.8 * mm});
            skCircle(sketch, "E46.0.1.33", {"center": v(70, 32.44) * mm, "radius": 0.8 * mm});
            skCircle(sketch, "E46.0.1.34", {"center": v(70, 27.44) * mm, "radius": 0.8 * mm});
            skCircle(sketch, "E46.0.1.35", {"center": v(70, 22.44) * mm, "radius": 0.8 * mm});
            skCircle(sketch, "E46.0.1.36", {"center": v(70, 17.44) * mm, "radius": 0.8 * mm});
            skCircle(sketch, "E46.0.1.37", {"center": v(70, 12.44) * mm, "radius": 0.8 * mm});
            skCircle(sketch, "E46.0.1.38", {"center": v(70, 7.44) * mm, "radius": 0.8 * mm});
            skCircle(sketch, "E46.0.1.39", {"center": v(70, 2.44) * mm, "radius": 0.8 * mm});
            skCircle(sketch, "E46.0.2.30", {"center": v(65, 47.44) * mm, "radius": 0.8 * mm});
            skCircle(sketch, "E46.0.2.31", {"center": v(65, 42.44) * mm, "radius": 0.8 * mm});
            skCircle(sketch, "E46.0.2.32", {"center": v(65, 37.44) * mm, "radius": 0.8 * mm});
            skCircle(sketch, "E46.0.2.33", {"center": v(65, 32.44) * mm, "radius": 0.8 * mm});
            skCircle(sketch, "E46.0.2.34", {"center": v(65, 27.44) * mm, "radius": 0.8 * mm});
            skCircle(sketch, "E46.0.2.35", {"center": v(65, 22.44) * mm, "radius": 0.8 * mm});
            skCircle(sketch, "E46.0.2.36", {"center": v(65, 17.44) * mm, "radius": 0.8 * mm});
            skCircle(sketch, "E46.0.2.37", {"center": v(65, 12.44) * mm, "radius": 0.8 * mm});
            skCircle(sketch, "E46.0.2.38", {"center": v(65, 7.44) * mm, "radius": 0.8 * mm});
            skCircle(sketch, "E46.0.2.39", {"center": v(65, 2.44) * mm, "radius": 0.8 * mm});
            skCircle(sketch, "E46.0.3.30", {"center": v(60, 47.44) * mm, "radius": 0.8 * mm});
            skCircle(sketch, "E46.0.3.31", {"center": v(60, 42.44) * mm, "radius": 0.8 * mm});
            skCircle(sketch, "E46.0.3.32", {"center": v(60, 37.44) * mm, "radius": 0.8 * mm});
            skCircle(sketch, "E46.0.3.33", {"center": v(60, 32.44) * mm, "radius": 0.8 * mm});
            skCircle(sketch, "E46.0.3.34", {"center": v(60, 27.44) * mm, "radius": 0.8 * mm});
            skCircle(sketch, "E46.0.3.35", {"center": v(60, 22.44) * mm, "radius": 0.8 * mm});
            skCircle(sketch, "E46.0.3.36", {"center": v(60, 17.44) * mm, "radius": 0.8 * mm});
            skCircle(sketch, "E46.0.3.37", {"center": v(60, 12.44) * mm, "radius": 0.8 * mm});
            skCircle(sketch, "E46.0.3.38", {"center": v(60, 7.44) * mm, "radius": 0.8 * mm});
            skCircle(sketch, "E46.0.3.39", {"center": v(60, 2.44) * mm, "radius": 0.8 * mm});
            skCircle(sketch, "E46.0.4.30", {"center": v(55, 47.44) * mm, "radius": 0.8 * mm});
            skCircle(sketch, "E46.0.4.31", {"center": v(55, 42.44) * mm, "radius": 0.8 * mm});
            skCircle(sketch, "E46.0.4.32", {"center": v(55, 37.44) * mm, "radius": 0.8 * mm});
            skCircle(sketch, "E46.0.4.33", {"center": v(55, 32.44) * mm, "radius": 0.8 * mm});
            skCircle(sketch, "E46.0.4.34", {"center": v(55, 27.44) * mm, "radius": 0.8 * mm});
            skCircle(sketch, "E46.0.4.35", {"center": v(55, 22.44) * mm, "radius": 0.8 * mm});
            skCircle(sketch, "E46.0.4.36", {"center": v(55, 17.44) * mm, "radius": 0.8 * mm});
            skCircle(sketch, "E46.0.4.37", {"center": v(55, 12.44) * mm, "radius": 0.8 * mm});
            skCircle(sketch, "E46.0.4.38", {"center": v(55, 7.44) * mm, "radius": 0.8 * mm});
            skCircle(sketch, "E46.0.4.39", {"center": v(55, 2.44) * mm, "radius": 0.8 * mm});
            skCircle(sketch, "E46.0.5.30", {"center": v(50, 47.44) * mm, "radius": 0.8 * mm});
            skCircle(sketch, "E46.0.5.31", {"center": v(50, 42.44) * mm, "radius": 0.8 * mm});
            skCircle(sketch, "E46.0.5.32", {"center": v(50, 37.44) * mm, "radius": 0.8 * mm});
            skCircle(sketch, "E46.0.5.33", {"center": v(50, 32.44) * mm, "radius": 0.8 * mm});
            skCircle(sketch, "E46.0.5.34", {"center": v(50, 27.44) * mm, "radius": 0.8 * mm});
            skCircle(sketch, "E46.0.5.35", {"center": v(50, 22.44) * mm, "radius": 0.8 * mm});
            skCircle(sketch, "E46.0.5.36", {"center": v(50, 17.44) * mm, "radius": 0.8 * mm});
            skCircle(sketch, "E46.0.5.37", {"center": v(50, 12.44) * mm, "radius": 0.8 * mm});
            skCircle(sketch, "E46.0.5.38", {"center": v(50, 7.44) * mm, "radius": 0.8 * mm});
            skCircle(sketch, "E46.0.5.39", {"center": v(50, 2.44) * mm, "radius": 0.8 * mm});
            skCircle(sketch, "E46.0.6.30", {"center": v(45, 47.44) * mm, "radius": 0.8 * mm});
            skCircle(sketch, "E46.0.6.31", {"center": v(45, 42.44) * mm, "radius": 0.8 * mm});
            skCircle(sketch, "E46.0.6.32", {"center": v(45, 37.44) * mm, "radius": 0.8 * mm});
            skCircle(sketch, "E46.0.6.33", {"center": v(45, 32.44) * mm, "radius": 0.8 * mm});
            skCircle(sketch, "E46.0.6.34", {"center": v(45, 27.44) * mm, "radius": 0.8 * mm});
            skCircle(sketch, "E46.0.6.35", {"center": v(45, 22.44) * mm, "radius": 0.8 * mm});
            skCircle(sketch, "E46.0.6.36", {"center": v(45, 17.44) * mm, "radius": 0.8 * mm});
            skCircle(sketch, "E46.0.6.37", {"center": v(45, 12.44) * mm, "radius": 0.8 * mm});
            skCircle(sketch, "E46.0.6.38", {"center": v(45, 7.44) * mm, "radius": 0.8 * mm});
            skCircle(sketch, "E46.0.6.39", {"center": v(45, 2.44) * mm, "radius": 0.8 * mm});
            skCircle(sketch, "E46.0.7.30", {"center": v(40, 47.44) * mm, "radius": 0.8 * mm});
            skCircle(sketch, "E46.0.7.31", {"center": v(40, 42.44) * mm, "radius": 0.8 * mm});
            skCircle(sketch, "E46.0.7.32", {"center": v(40, 37.44) * mm, "radius": 0.8 * mm});
            skCircle(sketch, "E46.0.7.33", {"center": v(40, 32.44) * mm, "radius": 0.8 * mm});
            skCircle(sketch, "E46.0.7.34", {"center": v(40, 27.44) * mm, "radius": 0.8 * mm});
            skCircle(sketch, "E46.0.7.35", {"center": v(40, 22.44) * mm, "radius": 0.8 * mm});
            skCircle(sketch, "E46.0.7.36", {"center": v(40, 17.44) * mm, "radius": 0.8 * mm});
            skCircle(sketch, "E46.0.7.37", {"center": v(40, 12.44) * mm, "radius": 0.8 * mm});
            skCircle(sketch, "E46.0.7.38", {"center": v(40, 7.44) * mm, "radius": 0.8 * mm});
            skCircle(sketch, "E46.0.7.39", {"center": v(40, 2.44) * mm, "radius": 0.8 * mm});
            skCircle(sketch, "E46.0.8.30", {"center": v(35, 47.44) * mm, "radius": 0.8 * mm});
            skCircle(sketch, "E46.0.8.31", {"center": v(35, 42.44) * mm, "radius": 0.8 * mm});
            skCircle(sketch, "E46.0.8.32", {"center": v(35, 37.44) * mm, "radius": 0.8 * mm});
            skCircle(sketch, "E46.0.8.33", {"center": v(35, 32.44) * mm, "radius": 0.8 * mm});
            skCircle(sketch, "E46.0.8.34", {"center": v(35, 27.44) * mm, "radius": 0.8 * mm});
            skCircle(sketch, "E46.0.8.35", {"center": v(35, 22.44) * mm, "radius": 0.8 * mm});
            skCircle(sketch, "E46.0.8.36", {"center": v(35, 17.44) * mm, "radius": 0.8 * mm});
            skCircle(sketch, "E46.0.8.37", {"center": v(35, 12.44) * mm, "radius": 0.8 * mm});
            skCircle(sketch, "E46.0.8.38", {"center": v(35, 7.44) * mm, "radius": 0.8 * mm});
            skCircle(sketch, "E46.0.8.39", {"center": v(35, 2.44) * mm, "radius": 0.8 * mm});
            skCircle(sketch, "E46.0.9.30", {"center": v(30, 47.44) * mm, "radius": 0.8 * mm});
            skCircle(sketch, "E46.0.9.31", {"center": v(30, 42.44) * mm, "radius": 0.8 * mm});
            skCircle(sketch, "E46.0.9.32", {"center": v(30, 37.44) * mm, "radius": 0.8 * mm});
            skCircle(sketch, "E46.0.9.33", {"center": v(30, 32.44) * mm, "radius": 0.8 * mm});
            skCircle(sketch, "E46.0.9.34", {"center": v(30, 27.44) * mm, "radius": 0.8 * mm});
            skCircle(sketch, "E46.0.9.35", {"center": v(30, 22.44) * mm, "radius": 0.8 * mm});
            skCircle(sketch, "E46.0.9.36", {"center": v(30, 17.44) * mm, "radius": 0.8 * mm});
            skCircle(sketch, "E46.0.9.37", {"center": v(30, 12.44) * mm, "radius": 0.8 * mm});
            skCircle(sketch, "E46.0.9.38", {"center": v(30, 7.44) * mm, "radius": 0.8 * mm});
            skCircle(sketch, "E46.0.9.39", {"center": v(30, 2.44) * mm, "radius": 0.8 * mm});
            skCircle(sketch, "E46.0.10.30", {"center": v(25, 47.44) * mm, "radius": 0.8 * mm});
            skCircle(sketch, "E46.0.10.31", {"center": v(25, 42.44) * mm, "radius": 0.8 * mm});
            skCircle(sketch, "E46.0.10.32", {"center": v(25, 37.44) * mm, "radius": 0.8 * mm});
            skCircle(sketch, "E46.0.10.33", {"center": v(25, 32.44) * mm, "radius": 0.8 * mm});
            skCircle(sketch, "E46.0.10.34", {"center": v(25, 27.44) * mm, "radius": 0.8 * mm});
            skCircle(sketch, "E46.0.10.35", {"center": v(25, 22.44) * mm, "radius": 0.8 * mm});
            skCircle(sketch, "E46.0.10.36", {"center": v(25, 17.44) * mm, "radius": 0.8 * mm});
            skCircle(sketch, "E46.0.10.37", {"center": v(25, 12.44) * mm, "radius": 0.8 * mm});
            skCircle(sketch, "E46.0.10.38", {"center": v(25, 7.44) * mm, "radius": 0.8 * mm});
            skCircle(sketch, "E46.0.10.39", {"center": v(25, 2.44) * mm, "radius": 0.8 * mm});
            skCircle(sketch, "E46.0.11.30", {"center": v(20, 47.44) * mm, "radius": 0.8 * mm});
            skCircle(sketch, "E46.0.11.31", {"center": v(20, 42.44) * mm, "radius": 0.8 * mm});
            skCircle(sketch, "E46.0.11.32", {"center": v(20, 37.44) * mm, "radius": 0.8 * mm});
            skCircle(sketch, "E46.0.11.33", {"center": v(20, 32.44) * mm, "radius": 0.8 * mm});
            skCircle(sketch, "E46.0.11.34", {"center": v(20, 27.44) * mm, "radius": 0.8 * mm});
            skCircle(sketch, "E46.0.11.35", {"center": v(20, 22.44) * mm, "radius": 0.8 * mm});
            skCircle(sketch, "E46.0.11.36", {"center": v(20, 17.44) * mm, "radius": 0.8 * mm});
            skCircle(sketch, "E46.0.11.37", {"center": v(20, 12.44) * mm, "radius": 0.8 * mm});
            skCircle(sketch, "E46.0.11.38", {"center": v(20, 7.44) * mm, "radius": 0.8 * mm});
            skCircle(sketch, "E46.0.11.39", {"center": v(20, 2.44) * mm, "radius": 0.8 * mm});
            skCircle(sketch, "E46.0.12.30", {"center": v(15, 47.44) * mm, "radius": 0.8 * mm});
            skCircle(sketch, "E46.0.12.31", {"center": v(15, 42.44) * mm, "radius": 0.8 * mm});
            skCircle(sketch, "E46.0.12.32", {"center": v(15, 37.44) * mm, "radius": 0.8 * mm});
            skCircle(sketch, "E46.0.12.33", {"center": v(15, 32.44) * mm, "radius": 0.8 * mm});
            skCircle(sketch, "E46.0.12.34", {"center": v(15, 27.44) * mm, "radius": 0.8 * mm});
            skCircle(sketch, "E46.0.12.35", {"center": v(15, 22.44) * mm, "radius": 0.8 * mm});
            skCircle(sketch, "E46.0.12.36", {"center": v(15, 17.44) * mm, "radius": 0.8 * mm});
            skCircle(sketch, "E46.0.12.37", {"center": v(15, 12.44) * mm, "radius": 0.8 * mm});
            skCircle(sketch, "E46.0.12.38", {"center": v(15, 7.44) * mm, "radius": 0.8 * mm});
            skCircle(sketch, "E46.0.12.39", {"center": v(15, 2.44) * mm, "radius": 0.8 * mm});
            skCircle(sketch, "E46.0.13.30", {"center": v(10, 47.44) * mm, "radius": 0.8 * mm});
            skCircle(sketch, "E46.0.13.31", {"center": v(10, 42.44) * mm, "radius": 0.8 * mm});
            skCircle(sketch, "E46.0.13.32", {"center": v(10, 37.44) * mm, "radius": 0.8 * mm});
            skCircle(sketch, "E46.0.13.33", {"center": v(10, 32.44) * mm, "radius": 0.8 * mm});
            skCircle(sketch, "E46.0.13.34", {"center": v(10, 27.44) * mm, "radius": 0.8 * mm});
            skCircle(sketch, "E46.0.13.35", {"center": v(10, 22.44) * mm, "radius": 0.8 * mm});
            skCircle(sketch, "E46.0.13.36", {"center": v(10, 17.44) * mm, "radius": 0.8 * mm});
            skCircle(sketch, "E46.0.13.37", {"center": v(10, 12.44) * mm, "radius": 0.8 * mm});
            skCircle(sketch, "E46.0.13.38", {"center": v(10, 7.44) * mm, "radius": 0.8 * mm});
            skCircle(sketch, "E46.0.13.39", {"center": v(10, 2.44) * mm, "radius": 0.8 * mm});
            skCircle(sketch, "E46.0.14.30", {"center": v(5, 47.44) * mm, "radius": 0.8 * mm});
            skCircle(sketch, "E46.0.14.31", {"center": v(5, 42.44) * mm, "radius": 0.8 * mm});
            skCircle(sketch, "E46.0.14.32", {"center": v(5, 37.44) * mm, "radius": 0.8 * mm});
            skCircle(sketch, "E46.0.14.33", {"center": v(5, 32.44) * mm, "radius": 0.8 * mm});
            skCircle(sketch, "E46.0.14.34", {"center": v(5, 27.44) * mm, "radius": 0.8 * mm});
            skCircle(sketch, "E46.0.14.35", {"center": v(5, 22.44) * mm, "radius": 0.8 * mm});
            skCircle(sketch, "E46.0.14.36", {"center": v(5, 17.44) * mm, "radius": 0.8 * mm});
            skCircle(sketch, "E46.0.14.37", {"center": v(5, 12.44) * mm, "radius": 0.8 * mm});
            skCircle(sketch, "E46.0.14.38", {"center": v(5, 7.44) * mm, "radius": 0.8 * mm});
            skCircle(sketch, "E46.0.14.39", {"center": v(5, 2.44) * mm, "radius": 0.8 * mm});
            skCircle(sketch, "E46.0.15.30", {"center": v(0, 47.44) * mm, "radius": 0.8 * mm});
            skCircle(sketch, "E46.0.15.31", {"center": v(0, 42.44) * mm, "radius": 0.8 * mm});
            skCircle(sketch, "E46.0.15.32", {"center": v(0, 37.44) * mm, "radius": 0.8 * mm});
            skCircle(sketch, "E46.0.15.33", {"center": v(0, 32.44) * mm, "radius": 0.8 * mm});
            skCircle(sketch, "E46.0.15.34", {"center": v(0, 27.44) * mm, "radius": 0.8 * mm});
            skCircle(sketch, "E46.0.15.35", {"center": v(0, 22.44) * mm, "radius": 0.8 * mm});
            skCircle(sketch, "E46.0.15.36", {"center": v(0, 17.44) * mm, "radius": 0.8 * mm});
            skCircle(sketch, "E46.0.15.37", {"center": v(0, 12.44) * mm, "radius": 0.8 * mm});
            skCircle(sketch, "E46.0.15.38", {"center": v(0, 7.44) * mm, "radius": 0.8 * mm});
            skCircle(sketch, "E46.0.15.39", {"center": v(0, 2.44) * mm, "radius": 0.8 * mm});
            skCircle(sketch, "E46.0.16.30", {"center": v(-5, 47.44) * mm, "radius": 0.8 * mm});
            skCircle(sketch, "E46.0.16.31", {"center": v(-5, 42.44) * mm, "radius": 0.8 * mm});
            skCircle(sketch, "E46.0.16.32", {"center": v(-5, 37.44) * mm, "radius": 0.8 * mm});
            skCircle(sketch, "E46.0.16.33", {"center": v(-5, 32.44) * mm, "radius": 0.8 * mm});
            skCircle(sketch, "E46.0.16.34", {"center": v(-5, 27.44) * mm, "radius": 0.8 * mm});
            skCircle(sketch, "E46.0.16.35", {"center": v(-5, 22.44) * mm, "radius": 0.8 * mm});
            skCircle(sketch, "E46.0.16.36", {"center": v(-5, 17.44) * mm, "radius": 0.8 * mm});
            skCircle(sketch, "E46.0.16.37", {"center": v(-5, 12.44) * mm, "radius": 0.8 * mm});
            skCircle(sketch, "E46.0.16.38", {"center": v(-5, 7.44) * mm, "radius": 0.8 * mm});
            skCircle(sketch, "E46.0.16.39", {"center": v(-5, 2.44) * mm, "radius": 0.8 * mm});
            skCircle(sketch, "E46.0.17.30", {"center": v(-10, 47.44) * mm, "radius": 0.8 * mm});
            skCircle(sketch, "E46.0.17.31", {"center": v(-10, 42.44) * mm, "radius": 0.8 * mm});
            skCircle(sketch, "E46.0.17.32", {"center": v(-10, 37.44) * mm, "radius": 0.8 * mm});
            skCircle(sketch, "E46.0.17.33", {"center": v(-10, 32.44) * mm, "radius": 0.8 * mm});
            skCircle(sketch, "E46.0.17.34", {"center": v(-10, 27.44) * mm, "radius": 0.8 * mm});
            skCircle(sketch, "E46.0.17.35", {"center": v(-10, 22.44) * mm, "radius": 0.8 * mm});
            skCircle(sketch, "E46.0.17.36", {"center": v(-10, 17.44) * mm, "radius": 0.8 * mm});
            skCircle(sketch, "E46.0.17.37", {"center": v(-10, 12.44) * mm, "radius": 0.8 * mm});
            skCircle(sketch, "E46.0.17.38", {"center": v(-10, 7.44) * mm, "radius": 0.8 * mm});
            skCircle(sketch, "E46.0.17.39", {"center": v(-10, 2.44) * mm, "radius": 0.8 * mm});
            skCircle(sketch, "E46.0.18.30", {"center": v(-15, 47.44) * mm, "radius": 0.8 * mm});
            skCircle(sketch, "E46.0.18.31", {"center": v(-15, 42.44) * mm, "radius": 0.8 * mm});
            skCircle(sketch, "E46.0.18.32", {"center": v(-15, 37.44) * mm, "radius": 0.8 * mm});
            skCircle(sketch, "E46.0.18.33", {"center": v(-15, 32.44) * mm, "radius": 0.8 * mm});
            skCircle(sketch, "E46.0.18.34", {"center": v(-15, 27.44) * mm, "radius": 0.8 * mm});
            skCircle(sketch, "E46.0.18.35", {"center": v(-15, 22.44) * mm, "radius": 0.8 * mm});
            skCircle(sketch, "E46.0.18.36", {"center": v(-15, 17.44) * mm, "radius": 0.8 * mm});
            skCircle(sketch, "E46.0.18.37", {"center": v(-15, 12.44) * mm, "radius": 0.8 * mm});
            skCircle(sketch, "E46.0.18.38", {"center": v(-15, 7.44) * mm, "radius": 0.8 * mm});
            skCircle(sketch, "E46.0.18.39", {"center": v(-15, 2.44) * mm, "radius": 0.8 * mm});
            skCircle(sketch, "E46.0.19.30", {"center": v(-20, 47.44) * mm, "radius": 0.8 * mm});
            skCircle(sketch, "E46.0.19.31", {"center": v(-20, 42.44) * mm, "radius": 0.8 * mm});
            skCircle(sketch, "E46.0.19.32", {"center": v(-20, 37.44) * mm, "radius": 0.8 * mm});
            skCircle(sketch, "E46.0.19.33", {"center": v(-20, 32.44) * mm, "radius": 0.8 * mm});
            skCircle(sketch, "E46.0.19.34", {"center": v(-20, 27.44) * mm, "radius": 0.8 * mm});
            skCircle(sketch, "E46.0.19.35", {"center": v(-20, 22.44) * mm, "radius": 0.8 * mm});
            skCircle(sketch, "E46.0.19.36", {"center": v(-20, 17.44) * mm, "radius": 0.8 * mm});
            skCircle(sketch, "E46.0.19.37", {"center": v(-20, 12.44) * mm, "radius": 0.8 * mm});
            skCircle(sketch, "E46.0.19.38", {"center": v(-20, 7.44) * mm, "radius": 0.8 * mm});
            skCircle(sketch, "E46.0.19.39", {"center": v(-20, 2.44) * mm, "radius": 0.8 * mm});
            skCircle(sketch, "E46.0.20.30", {"center": v(-25, 47.44) * mm, "radius": 0.8 * mm});
            skCircle(sketch, "E46.0.20.31", {"center": v(-25, 42.44) * mm, "radius": 0.8 * mm});
            skCircle(sketch, "E46.0.20.32", {"center": v(-25, 37.44) * mm, "radius": 0.8 * mm});
            skCircle(sketch, "E46.0.20.33", {"center": v(-25, 32.44) * mm, "radius": 0.8 * mm});
            skCircle(sketch, "E46.0.20.34", {"center": v(-25, 27.44) * mm, "radius": 0.8 * mm});
            skCircle(sketch, "E46.0.20.35", {"center": v(-25, 22.44) * mm, "radius": 0.8 * mm});
            skCircle(sketch, "E46.0.20.36", {"center": v(-25, 17.44) * mm, "radius": 0.8 * mm});
            skCircle(sketch, "E46.0.20.37", {"center": v(-25, 12.44) * mm, "radius": 0.8 * mm});
            skCircle(sketch, "E46.0.20.38", {"center": v(-25, 7.44) * mm, "radius": 0.8 * mm});
            skCircle(sketch, "E46.0.20.39", {"center": v(-25, 2.44) * mm, "radius": 0.8 * mm});
            skCircle(sketch, "E46.0.21.30", {"center": v(-30, 47.44) * mm, "radius": 0.8 * mm});
            skCircle(sketch, "E46.0.21.31", {"center": v(-30, 42.44) * mm, "radius": 0.8 * mm});
            skCircle(sketch, "E46.0.21.32", {"center": v(-30, 37.44) * mm, "radius": 0.8 * mm});
            skCircle(sketch, "E46.0.21.33", {"center": v(-30, 32.44) * mm, "radius": 0.8 * mm});
            skCircle(sketch, "E46.0.21.34", {"center": v(-30, 27.44) * mm, "radius": 0.8 * mm});
            skCircle(sketch, "E46.0.21.35", {"center": v(-30, 22.44) * mm, "radius": 0.8 * mm});
            skCircle(sketch, "E46.0.21.36", {"center": v(-30, 17.44) * mm, "radius": 0.8 * mm});
            skCircle(sketch, "E46.0.21.37", {"center": v(-30, 12.44) * mm, "radius": 0.8 * mm});
            skCircle(sketch, "E46.0.21.38", {"center": v(-30, 7.44) * mm, "radius": 0.8 * mm});
            skCircle(sketch, "E46.0.21.39", {"center": v(-30, 2.44) * mm, "radius": 0.8 * mm});
            skCircle(sketch, "E46.0.22.30", {"center": v(-35, 47.44) * mm, "radius": 0.8 * mm});
            skCircle(sketch, "E46.0.22.31", {"center": v(-35, 42.44) * mm, "radius": 0.8 * mm});
            skCircle(sketch, "E46.0.22.32", {"center": v(-35, 37.44) * mm, "radius": 0.8 * mm});
            skCircle(sketch, "E46.0.22.33", {"center": v(-35, 32.44) * mm, "radius": 0.8 * mm});
            skCircle(sketch, "E46.0.22.34", {"center": v(-35, 27.44) * mm, "radius": 0.8 * mm});
            skCircle(sketch, "E46.0.22.35", {"center": v(-35, 22.44) * mm, "radius": 0.8 * mm});
            skCircle(sketch, "E46.0.22.36", {"center": v(-35, 17.44) * mm, "radius": 0.8 * mm});
            skCircle(sketch, "E46.0.22.37", {"center": v(-35, 12.44) * mm, "radius": 0.8 * mm});
            skCircle(sketch, "E46.0.22.38", {"center": v(-35, 7.44) * mm, "radius": 0.8 * mm});
            skCircle(sketch, "E46.0.22.39", {"center": v(-35, 2.44) * mm, "radius": 0.8 * mm});
            skCircle(sketch, "E46.0.23.30", {"center": v(-40, 47.44) * mm, "radius": 0.8 * mm});
            skCircle(sketch, "E46.0.23.31", {"center": v(-40, 42.44) * mm, "radius": 0.8 * mm});
            skCircle(sketch, "E46.0.23.32", {"center": v(-40, 37.44) * mm, "radius": 0.8 * mm});
            skCircle(sketch, "E46.0.23.33", {"center": v(-40, 32.44) * mm, "radius": 0.8 * mm});
            skCircle(sketch, "E46.0.23.34", {"center": v(-40, 27.44) * mm, "radius": 0.8 * mm});
            skCircle(sketch, "E46.0.23.35", {"center": v(-40, 22.44) * mm, "radius": 0.8 * mm});
            skCircle(sketch, "E46.0.23.36", {"center": v(-40, 17.44) * mm, "radius": 0.8 * mm});
            skCircle(sketch, "E46.0.23.37", {"center": v(-40, 12.44) * mm, "radius": 0.8 * mm});
            skCircle(sketch, "E46.0.23.38", {"center": v(-40, 7.44) * mm, "radius": 0.8 * mm});
            skCircle(sketch, "E46.0.23.39", {"center": v(-40, 2.44) * mm, "radius": 0.8 * mm});
            skCircle(sketch, "E46.0.24.30", {"center": v(-45, 47.44) * mm, "radius": 0.8 * mm});
            skCircle(sketch, "E46.0.24.31", {"center": v(-45, 42.44) * mm, "radius": 0.8 * mm});
            skCircle(sketch, "E46.0.24.32", {"center": v(-45, 37.44) * mm, "radius": 0.8 * mm});
            skCircle(sketch, "E46.0.24.33", {"center": v(-45, 32.44) * mm, "radius": 0.8 * mm});
            skCircle(sketch, "E46.0.24.34", {"center": v(-45, 27.44) * mm, "radius": 0.8 * mm});
            skCircle(sketch, "E46.0.24.35", {"center": v(-45, 22.44) * mm, "radius": 0.8 * mm});
            skCircle(sketch, "E46.0.24.36", {"center": v(-45, 17.44) * mm, "radius": 0.8 * mm});
            skCircle(sketch, "E46.0.24.37", {"center": v(-45, 12.44) * mm, "radius": 0.8 * mm});
            skCircle(sketch, "E46.0.24.38", {"center": v(-45, 7.44) * mm, "radius": 0.8 * mm});
            skCircle(sketch, "E46.0.24.39", {"center": v(-45, 2.44) * mm, "radius": 0.8 * mm});
            skCircle(sketch, "E46.0.25.30", {"center": v(-50, 47.44) * mm, "radius": 0.8 * mm});
            skCircle(sketch, "E46.0.25.31", {"center": v(-50, 42.44) * mm, "radius": 0.8 * mm});
            skCircle(sketch, "E46.0.25.32", {"center": v(-50, 37.44) * mm, "radius": 0.8 * mm});
            skCircle(sketch, "E46.0.25.33", {"center": v(-50, 32.44) * mm, "radius": 0.8 * mm});
            skCircle(sketch, "E46.0.25.34", {"center": v(-50, 27.44) * mm, "radius": 0.8 * mm});
            skCircle(sketch, "E46.0.25.35", {"center": v(-50, 22.44) * mm, "radius": 0.8 * mm});
            skCircle(sketch, "E46.0.25.36", {"center": v(-50, 17.44) * mm, "radius": 0.8 * mm});
            skCircle(sketch, "E46.0.25.37", {"center": v(-50, 12.44) * mm, "radius": 0.8 * mm});
            skCircle(sketch, "E46.0.25.38", {"center": v(-50, 7.44) * mm, "radius": 0.8 * mm});
            skCircle(sketch, "E46.0.25.39", {"center": v(-50, 2.44) * mm, "radius": 0.8 * mm});
            skCircle(sketch, "E46.0.26.30", {"center": v(-55, 47.44) * mm, "radius": 0.8 * mm});
            skCircle(sketch, "E46.0.26.31", {"center": v(-55, 42.44) * mm, "radius": 0.8 * mm});
            skCircle(sketch, "E46.0.26.32", {"center": v(-55, 37.44) * mm, "radius": 0.8 * mm});
            skCircle(sketch, "E46.0.26.33", {"center": v(-55, 32.44) * mm, "radius": 0.8 * mm});
            skCircle(sketch, "E46.0.26.34", {"center": v(-55, 27.44) * mm, "radius": 0.8 * mm});
            skCircle(sketch, "E46.0.26.35", {"center": v(-55, 22.44) * mm, "radius": 0.8 * mm});
            skCircle(sketch, "E46.0.26.36", {"center": v(-55, 17.44) * mm, "radius": 0.8 * mm});
            skCircle(sketch, "E46.0.26.37", {"center": v(-55, 12.44) * mm, "radius": 0.8 * mm});
            skCircle(sketch, "E46.0.26.38", {"center": v(-55, 7.44) * mm, "radius": 0.8 * mm});
            skCircle(sketch, "E46.0.26.39", {"center": v(-55, 2.44) * mm, "radius": 0.8 * mm});
            skCircle(sketch, "E46.0.27.30", {"center": v(-60, 47.44) * mm, "radius": 0.8 * mm});
            skCircle(sketch, "E46.0.27.31", {"center": v(-60, 42.44) * mm, "radius": 0.8 * mm});
            skCircle(sketch, "E46.0.27.32", {"center": v(-60, 37.44) * mm, "radius": 0.8 * mm});
            skCircle(sketch, "E46.0.27.33", {"center": v(-60, 32.44) * mm, "radius": 0.8 * mm});
            skCircle(sketch, "E46.0.27.34", {"center": v(-60, 27.44) * mm, "radius": 0.8 * mm});
            skCircle(sketch, "E46.0.27.35", {"center": v(-60, 22.44) * mm, "radius": 0.8 * mm});
            skCircle(sketch, "E46.0.27.36", {"center": v(-60, 17.44) * mm, "radius": 0.8 * mm});
            skCircle(sketch, "E46.0.27.37", {"center": v(-60, 12.44) * mm, "radius": 0.8 * mm});
            skCircle(sketch, "E46.0.27.38", {"center": v(-60, 7.44) * mm, "radius": 0.8 * mm});
            skCircle(sketch, "E46.0.27.39", {"center": v(-60, 2.44) * mm, "radius": 0.8 * mm});
            skCircle(sketch, "E46.0.28.30", {"center": v(-65, 47.44) * mm, "radius": 0.8 * mm});
            skCircle(sketch, "E46.0.28.31", {"center": v(-65, 42.44) * mm, "radius": 0.8 * mm});
            skCircle(sketch, "E46.0.28.32", {"center": v(-65, 37.44) * mm, "radius": 0.8 * mm});
            skCircle(sketch, "E46.0.28.33", {"center": v(-65, 32.44) * mm, "radius": 0.8 * mm});
            skCircle(sketch, "E46.0.28.34", {"center": v(-65, 27.44) * mm, "radius": 0.8 * mm});
            skCircle(sketch, "E46.0.28.35", {"center": v(-65, 22.44) * mm, "radius": 0.8 * mm});
            skCircle(sketch, "E46.0.28.36", {"center": v(-65, 17.44) * mm, "radius": 0.8 * mm});
            skCircle(sketch, "E46.0.28.37", {"center": v(-65, 12.44) * mm, "radius": 0.8 * mm});
            skCircle(sketch, "E46.0.28.38", {"center": v(-65, 7.44) * mm, "radius": 0.8 * mm});
            skCircle(sketch, "E46.0.28.39", {"center": v(-65, 2.44) * mm, "radius": 0.8 * mm});
            skCircle(sketch, "E46.0.29.30", {"center": v(-70, 47.44) * mm, "radius": 0.8 * mm});
            skCircle(sketch, "E46.0.29.31", {"center": v(-70, 42.44) * mm, "radius": 0.8 * mm});
            skCircle(sketch, "E46.0.29.32", {"center": v(-70, 37.44) * mm, "radius": 0.8 * mm});
            skCircle(sketch, "E46.0.29.33", {"center": v(-70, 32.44) * mm, "radius": 0.8 * mm});
            skCircle(sketch, "E46.0.29.34", {"center": v(-70, 27.44) * mm, "radius": 0.8 * mm});
            skCircle(sketch, "E46.0.29.35", {"center": v(-70, 22.44) * mm, "radius": 0.8 * mm});
            skCircle(sketch, "E46.0.29.36", {"center": v(-70, 17.44) * mm, "radius": 0.8 * mm});
            skCircle(sketch, "E46.0.29.37", {"center": v(-70, 12.44) * mm, "radius": 0.8 * mm});
            skCircle(sketch, "E46.0.29.38", {"center": v(-70, 7.44) * mm, "radius": 0.8 * mm});
            skCircle(sketch, "E46.0.29.39", {"center": v(-70, 2.44) * mm, "radius": 0.8 * mm});
            skCircle(sketch, "E46.0.30.30", {"center": v(-75, 47.44) * mm, "radius": 0.8 * mm});
            skCircle(sketch, "E46.0.30.31", {"center": v(-75, 42.44) * mm, "radius": 0.8 * mm});
            skCircle(sketch, "E46.0.30.32", {"center": v(-75, 37.44) * mm, "radius": 0.8 * mm});
            skCircle(sketch, "E46.0.30.33", {"center": v(-75, 32.44) * mm, "radius": 0.8 * mm});
            skCircle(sketch, "E46.0.30.34", {"center": v(-75, 27.44) * mm, "radius": 0.8 * mm});
            skCircle(sketch, "E46.0.30.35", {"center": v(-75, 22.44) * mm, "radius": 0.8 * mm});
            skCircle(sketch, "E46.0.30.36", {"center": v(-75, 17.44) * mm, "radius": 0.8 * mm});
            skCircle(sketch, "E46.0.30.37", {"center": v(-75, 12.44) * mm, "radius": 0.8 * mm});
            skCircle(sketch, "E46.0.30.38", {"center": v(-75, 7.44) * mm, "radius": 0.8 * mm});
            skCircle(sketch, "E46.0.30.39", {"center": v(-75, 2.44) * mm, "radius": 0.8 * mm});
            skCircle(sketch, "E46.0.31.30", {"center": v(-80, 47.44) * mm, "radius": 0.8 * mm});
            skCircle(sketch, "E46.0.31.31", {"center": v(-80, 42.44) * mm, "radius": 0.8 * mm});
            skCircle(sketch, "E46.0.31.32", {"center": v(-80, 37.44) * mm, "radius": 0.8 * mm});
            skCircle(sketch, "E46.0.31.33", {"center": v(-80, 32.44) * mm, "radius": 0.8 * mm});
            skCircle(sketch, "E46.0.31.34", {"center": v(-80, 27.44) * mm, "radius": 0.8 * mm});
            skCircle(sketch, "E46.0.31.35", {"center": v(-80, 22.44) * mm, "radius": 0.8 * mm});
            skCircle(sketch, "E46.0.31.36", {"center": v(-80, 17.44) * mm, "radius": 0.8 * mm});
            skCircle(sketch, "E46.0.31.37", {"center": v(-80, 12.44) * mm, "radius": 0.8 * mm});
            skCircle(sketch, "E46.0.31.38", {"center": v(-80, 7.44) * mm, "radius": 0.8 * mm});
            skCircle(sketch, "E46.0.31.39", {"center": v(-80, 2.44) * mm, "radius": 0.8 * mm});
            skCircle(sketch, "E46.0.32.30", {"center": v(-85, 47.44) * mm, "radius": 0.8 * mm});
            skCircle(sketch, "E46.0.32.31", {"center": v(-85, 42.44) * mm, "radius": 0.8 * mm});
            skCircle(sketch, "E46.0.32.32", {"center": v(-85, 37.44) * mm, "radius": 0.8 * mm});
            skCircle(sketch, "E46.0.32.33", {"center": v(-85, 32.44) * mm, "radius": 0.8 * mm});
            skCircle(sketch, "E46.0.32.34", {"center": v(-85, 27.44) * mm, "radius": 0.8 * mm});
            skCircle(sketch, "E46.0.32.35", {"center": v(-85, 22.44) * mm, "radius": 0.8 * mm});
            skCircle(sketch, "E46.0.32.36", {"center": v(-85, 17.44) * mm, "radius": 0.8 * mm});
            skCircle(sketch, "E46.0.32.37", {"center": v(-85, 12.44) * mm, "radius": 0.8 * mm});
            skCircle(sketch, "E46.0.32.38", {"center": v(-85, 7.44) * mm, "radius": 0.8 * mm});
            skCircle(sketch, "E46.0.32.39", {"center": v(-85, 2.44) * mm, "radius": 0.8 * mm});
            skCircle(sketch, "E46.0.33.30", {"center": v(-90, 47.44) * mm, "radius": 0.8 * mm});
            skCircle(sketch, "E46.0.33.31", {"center": v(-90, 42.44) * mm, "radius": 0.8 * mm});
            skCircle(sketch, "E46.0.33.32", {"center": v(-90, 37.44) * mm, "radius": 0.8 * mm});
            skCircle(sketch, "E46.0.33.33", {"center": v(-90, 32.44) * mm, "radius": 0.8 * mm});
            skCircle(sketch, "E46.0.33.34", {"center": v(-90, 27.44) * mm, "radius": 0.8 * mm});
            skCircle(sketch, "E46.0.33.35", {"center": v(-90, 22.44) * mm, "radius": 0.8 * mm});
            skCircle(sketch, "E46.0.33.36", {"center": v(-90, 17.44) * mm, "radius": 0.8 * mm});
            skCircle(sketch, "E46.0.33.37", {"center": v(-90, 12.44) * mm, "radius": 0.8 * mm});
            skCircle(sketch, "E46.0.33.38", {"center": v(-90, 7.44) * mm, "radius": 0.8 * mm});
            skCircle(sketch, "E46.0.33.39", {"center": v(-90, 2.44) * mm, "radius": 0.8 * mm});
            skCircle(sketch, "E46.0.34.30", {"center": v(-95, 47.44) * mm, "radius": 0.8 * mm});
            skCircle(sketch, "E46.0.34.31", {"center": v(-95, 42.44) * mm, "radius": 0.8 * mm});
            skCircle(sketch, "E46.0.34.32", {"center": v(-95, 37.44) * mm, "radius": 0.8 * mm});
            skCircle(sketch, "E46.0.34.33", {"center": v(-95, 32.44) * mm, "radius": 0.8 * mm});
            skCircle(sketch, "E46.0.34.34", {"center": v(-95, 27.44) * mm, "radius": 0.8 * mm});
            skCircle(sketch, "E46.0.34.35", {"center": v(-95, 22.44) * mm, "radius": 0.8 * mm});
            skCircle(sketch, "E46.0.34.36", {"center": v(-95, 17.44) * mm, "radius": 0.8 * mm});
            skCircle(sketch, "E46.0.34.37", {"center": v(-95, 12.44) * mm, "radius": 0.8 * mm});
            skCircle(sketch, "E46.0.34.38", {"center": v(-95, 7.44) * mm, "radius": 0.8 * mm});
            skCircle(sketch, "E46.0.34.39", {"center": v(-95, 2.44) * mm, "radius": 0.8 * mm});
            skCircle(sketch, "E46.0.35.30", {"center": v(-100, 47.44) * mm, "radius": 0.8 * mm});
            skCircle(sketch, "E46.0.35.31", {"center": v(-100, 42.44) * mm, "radius": 0.8 * mm});
            skCircle(sketch, "E46.0.35.32", {"center": v(-100, 37.44) * mm, "radius": 0.8 * mm});
            skCircle(sketch, "E46.0.35.33", {"center": v(-100, 32.44) * mm, "radius": 0.8 * mm});
            skCircle(sketch, "E46.0.35.34", {"center": v(-100, 27.44) * mm, "radius": 0.8 * mm});
            skCircle(sketch, "E46.0.35.35", {"center": v(-100, 22.44) * mm, "radius": 0.8 * mm});
            skCircle(sketch, "E46.0.35.36", {"center": v(-100, 17.44) * mm, "radius": 0.8 * mm});
            skCircle(sketch, "E46.0.35.37", {"center": v(-100, 12.44) * mm, "radius": 0.8 * mm});
            skCircle(sketch, "E46.0.35.38", {"center": v(-100, 7.44) * mm, "radius": 0.8 * mm});
            skCircle(sketch, "E46.0.35.39", {"center": v(-100, 2.44) * mm, "radius": 0.8 * mm});
            skCircle(sketch, "E46.0.36.30", {"center": v(-105, 47.44) * mm, "radius": 0.8 * mm});
            skCircle(sketch, "E46.0.36.31", {"center": v(-105, 42.44) * mm, "radius": 0.8 * mm});
            skCircle(sketch, "E46.0.36.32", {"center": v(-105, 37.44) * mm, "radius": 0.8 * mm});
            skCircle(sketch, "E46.0.36.33", {"center": v(-105, 32.44) * mm, "radius": 0.8 * mm});
            skCircle(sketch, "E46.0.36.34", {"center": v(-105, 27.44) * mm, "radius": 0.8 * mm});
            skCircle(sketch, "E46.0.36.35", {"center": v(-105, 22.44) * mm, "radius": 0.8 * mm});
            skCircle(sketch, "E46.0.36.36", {"center": v(-105, 17.44) * mm, "radius": 0.8 * mm});
            skCircle(sketch, "E46.0.36.37", {"center": v(-105, 12.44) * mm, "radius": 0.8 * mm});
            skCircle(sketch, "E46.0.36.38", {"center": v(-105, 7.44) * mm, "radius": 0.8 * mm});
            skCircle(sketch, "E46.0.36.39", {"center": v(-105, 2.44) * mm, "radius": 0.8 * mm});
            skCircle(sketch, "E46.0.37.30", {"center": v(-110, 47.44) * mm, "radius": 0.8 * mm});
            skCircle(sketch, "E46.0.37.31", {"center": v(-110, 42.44) * mm, "radius": 0.8 * mm});
            skCircle(sketch, "E46.0.37.32", {"center": v(-110, 37.44) * mm, "radius": 0.8 * mm});
            skCircle(sketch, "E46.0.37.33", {"center": v(-110, 32.44) * mm, "radius": 0.8 * mm});
            skCircle(sketch, "E46.0.37.34", {"center": v(-110, 27.44) * mm, "radius": 0.8 * mm});
            skCircle(sketch, "E46.0.37.35", {"center": v(-110, 22.44) * mm, "radius": 0.8 * mm});
            skCircle(sketch, "E46.0.37.36", {"center": v(-110, 17.44) * mm, "radius": 0.8 * mm});
            skCircle(sketch, "E46.0.37.37", {"center": v(-110, 12.44) * mm, "radius": 0.8 * mm});
            skCircle(sketch, "E46.0.37.38", {"center": v(-110, 7.44) * mm, "radius": 0.8 * mm});
            skCircle(sketch, "E46.0.37.39", {"center": v(-110, 2.44) * mm, "radius": 0.8 * mm});
            skCircle(sketch, "E46.0.38.30", {"center": v(-115, 47.44) * mm, "radius": 0.8 * mm});
            skCircle(sketch, "E46.0.38.31", {"center": v(-115, 42.44) * mm, "radius": 0.8 * mm});
            skCircle(sketch, "E46.0.38.32", {"center": v(-115, 37.44) * mm, "radius": 0.8 * mm});
            skCircle(sketch, "E46.0.38.33", {"center": v(-115, 32.44) * mm, "radius": 0.8 * mm});
            skCircle(sketch, "E46.0.38.34", {"center": v(-115, 27.44) * mm, "radius": 0.8 * mm});
            skCircle(sketch, "E46.0.38.35", {"center": v(-115, 22.44) * mm, "radius": 0.8 * mm});
            skCircle(sketch, "E46.0.38.36", {"center": v(-115, 17.44) * mm, "radius": 0.8 * mm});
            skCircle(sketch, "E46.0.38.37", {"center": v(-115, 12.44) * mm, "radius": 0.8 * mm});
            skCircle(sketch, "E46.0.38.38", {"center": v(-115, 7.44) * mm, "radius": 0.8 * mm});
            skCircle(sketch, "E46.0.38.39", {"center": v(-115, 2.44) * mm, "radius": 0.8 * mm});
            skCircle(sketch, "E46.0.39.30", {"center": v(-120, 47.44) * mm, "radius": 0.8 * mm});
            skCircle(sketch, "E46.0.39.31", {"center": v(-120, 42.44) * mm, "radius": 0.8 * mm});
            skCircle(sketch, "E46.0.39.32", {"center": v(-120, 37.44) * mm, "radius": 0.8 * mm});
            skCircle(sketch, "E46.0.39.33", {"center": v(-120, 32.44) * mm, "radius": 0.8 * mm});
            skCircle(sketch, "E46.0.39.34", {"center": v(-120, 27.44) * mm, "radius": 0.8 * mm});
            skCircle(sketch, "E46.0.39.35", {"center": v(-120, 22.44) * mm, "radius": 0.8 * mm});
            skCircle(sketch, "E46.0.39.36", {"center": v(-120, 17.44) * mm, "radius": 0.8 * mm});
            skCircle(sketch, "E46.0.39.37", {"center": v(-120, 12.44) * mm, "radius": 0.8 * mm});
            skCircle(sketch, "E46.0.39.38", {"center": v(-120, 7.44) * mm, "radius": 0.8 * mm});
            skCircle(sketch, "E46.0.39.39", {"center": v(-120, 2.44) * mm, "radius": 0.8 * mm});
            skCircle(sketch, "E46.0.40.30", {"center": v(-125, 47.44) * mm, "radius": 0.8 * mm});
            skCircle(sketch, "E46.0.40.31", {"center": v(-125, 42.44) * mm, "radius": 0.8 * mm});
            skCircle(sketch, "E46.0.40.32", {"center": v(-125, 37.44) * mm, "radius": 0.8 * mm});
            skCircle(sketch, "E46.0.40.33", {"center": v(-125, 32.44) * mm, "radius": 0.8 * mm});
            skCircle(sketch, "E46.0.40.34", {"center": v(-125, 27.44) * mm, "radius": 0.8 * mm});
            skCircle(sketch, "E46.0.40.35", {"center": v(-125, 22.44) * mm, "radius": 0.8 * mm});
            skCircle(sketch, "E46.0.40.36", {"center": v(-125, 17.44) * mm, "radius": 0.8 * mm});
            skCircle(sketch, "E46.0.40.37", {"center": v(-125, 12.44) * mm, "radius": 0.8 * mm});
            skCircle(sketch, "E46.0.40.38", {"center": v(-125, 7.44) * mm, "radius": 0.8 * mm});
            skCircle(sketch, "E46.0.40.39", {"center": v(-125, 2.44) * mm, "radius": 0.8 * mm});
            skCircle(sketch, "E46.0.41.30", {"center": v(-130, 47.44) * mm, "radius": 0.8 * mm});
            skCircle(sketch, "E46.0.41.31", {"center": v(-130, 42.44) * mm, "radius": 0.8 * mm});
            skCircle(sketch, "E46.0.41.32", {"center": v(-130, 37.44) * mm, "radius": 0.8 * mm});
            skCircle(sketch, "E46.0.41.33", {"center": v(-130, 32.44) * mm, "radius": 0.8 * mm});
            skCircle(sketch, "E46.0.41.34", {"center": v(-130, 27.44) * mm, "radius": 0.8 * mm});
            skCircle(sketch, "E46.0.41.35", {"center": v(-130, 22.44) * mm, "radius": 0.8 * mm});
            skCircle(sketch, "E46.0.41.36", {"center": v(-130, 17.44) * mm, "radius": 0.8 * mm});
            skCircle(sketch, "E46.0.41.37", {"center": v(-130, 12.44) * mm, "radius": 0.8 * mm});
            skCircle(sketch, "E46.0.41.38", {"center": v(-130, 7.44) * mm, "radius": 0.8 * mm});
            skCircle(sketch, "E46.0.41.39", {"center": v(-130, 2.44) * mm, "radius": 0.8 * mm});
            skCircle(sketch, "E46.0.42.30", {"center": v(-135, 47.44) * mm, "radius": 0.8 * mm});
            skCircle(sketch, "E46.0.42.31", {"center": v(-135, 42.44) * mm, "radius": 0.8 * mm});
            skCircle(sketch, "E46.0.42.32", {"center": v(-135, 37.44) * mm, "radius": 0.8 * mm});
            skCircle(sketch, "E46.0.42.33", {"center": v(-135, 32.44) * mm, "radius": 0.8 * mm});
            skCircle(sketch, "E46.0.42.34", {"center": v(-135, 27.44) * mm, "radius": 0.8 * mm});
            skCircle(sketch, "E46.0.42.35", {"center": v(-135, 22.44) * mm, "radius": 0.8 * mm});
            skCircle(sketch, "E46.0.42.36", {"center": v(-135, 17.44) * mm, "radius": 0.8 * mm});
            skCircle(sketch, "E46.0.42.37", {"center": v(-135, 12.44) * mm, "radius": 0.8 * mm});
            skCircle(sketch, "E46.0.42.38", {"center": v(-135, 7.44) * mm, "radius": 0.8 * mm});
            skCircle(sketch, "E46.0.42.39", {"center": v(-135, 2.44) * mm, "radius": 0.8 * mm});
            skCircle(sketch, "E46.0.43.30", {"center": v(-140, 47.44) * mm, "radius": 0.8 * mm});
            skCircle(sketch, "E46.0.43.31", {"center": v(-140, 42.44) * mm, "radius": 0.8 * mm});
            skCircle(sketch, "E46.0.43.32", {"center": v(-140, 37.44) * mm, "radius": 0.8 * mm});
            skCircle(sketch, "E46.0.43.33", {"center": v(-140, 32.44) * mm, "radius": 0.8 * mm});
            skCircle(sketch, "E46.0.43.34", {"center": v(-140, 27.44) * mm, "radius": 0.8 * mm});
            skCircle(sketch, "E46.0.43.35", {"center": v(-140, 22.44) * mm, "radius": 0.8 * mm});
            skCircle(sketch, "E46.0.43.36", {"center": v(-140, 17.44) * mm, "radius": 0.8 * mm});
            skCircle(sketch, "E46.0.43.37", {"center": v(-140, 12.44) * mm, "radius": 0.8 * mm});
            skCircle(sketch, "E46.0.43.38", {"center": v(-140, 7.44) * mm, "radius": 0.8 * mm});
            skCircle(sketch, "E46.0.43.39", {"center": v(-140, 2.44) * mm, "radius": 0.8 * mm});
            skCircle(sketch, "E46.0.44.30", {"center": v(-145, 47.44) * mm, "radius": 0.8 * mm});
            skCircle(sketch, "E46.0.44.31", {"center": v(-145, 42.44) * mm, "radius": 0.8 * mm});
            skCircle(sketch, "E46.0.44.32", {"center": v(-145, 37.44) * mm, "radius": 0.8 * mm});
            skCircle(sketch, "E46.0.44.33", {"center": v(-145, 32.44) * mm, "radius": 0.8 * mm});
            skCircle(sketch, "E46.0.44.34", {"center": v(-145, 27.44) * mm, "radius": 0.8 * mm});
            skCircle(sketch, "E46.0.44.35", {"center": v(-145, 22.44) * mm, "radius": 0.8 * mm});
            skCircle(sketch, "E46.0.44.36", {"center": v(-145, 17.44) * mm, "radius": 0.8 * mm});
            skCircle(sketch, "E46.0.44.37", {"center": v(-145, 12.44) * mm, "radius": 0.8 * mm});
            skCircle(sketch, "E46.0.44.38", {"center": v(-145, 7.44) * mm, "radius": 0.8 * mm});
            skCircle(sketch, "E46.0.44.39", {"center": v(-145, 2.44) * mm, "radius": 0.8 * mm});
            skCircle(sketch, "E46.0.45.30", {"center": v(-150, 47.44) * mm, "radius": 0.8 * mm});
            skCircle(sketch, "E46.0.45.31", {"center": v(-150, 42.44) * mm, "radius": 0.8 * mm});
            skCircle(sketch, "E46.0.45.32", {"center": v(-150, 37.44) * mm, "radius": 0.8 * mm});
            skCircle(sketch, "E46.0.45.33", {"center": v(-150, 32.44) * mm, "radius": 0.8 * mm});
            skCircle(sketch, "E46.0.45.34", {"center": v(-150, 27.44) * mm, "radius": 0.8 * mm});
            skCircle(sketch, "E46.0.45.35", {"center": v(-150, 22.44) * mm, "radius": 0.8 * mm});
            skCircle(sketch, "E46.0.45.36", {"center": v(-150, 17.44) * mm, "radius": 0.8 * mm});
            skCircle(sketch, "E46.0.45.37", {"center": v(-150, 12.44) * mm, "radius": 0.8 * mm});
            skCircle(sketch, "E46.0.45.38", {"center": v(-150, 7.44) * mm, "radius": 0.8 * mm});
            skCircle(sketch, "E46.0.45.39", {"center": v(-150, 2.44) * mm, "radius": 0.8 * mm});
            skCircle(sketch, "E46.0.46.30", {"center": v(-155, 47.44) * mm, "radius": 0.8 * mm});
            skCircle(sketch, "E46.0.46.31", {"center": v(-155, 42.44) * mm, "radius": 0.8 * mm});
            skCircle(sketch, "E46.0.46.32", {"center": v(-155, 37.44) * mm, "radius": 0.8 * mm});
            skCircle(sketch, "E46.0.46.33", {"center": v(-155, 32.44) * mm, "radius": 0.8 * mm});
            skCircle(sketch, "E46.0.46.34", {"center": v(-155, 27.44) * mm, "radius": 0.8 * mm});
            skCircle(sketch, "E46.0.46.35", {"center": v(-155, 22.44) * mm, "radius": 0.8 * mm});
            skCircle(sketch, "E46.0.46.36", {"center": v(-155, 17.44) * mm, "radius": 0.8 * mm});
            skCircle(sketch, "E46.0.46.37", {"center": v(-155, 12.44) * mm, "radius": 0.8 * mm});
            skCircle(sketch, "E46.0.46.38", {"center": v(-155, 7.44) * mm, "radius": 0.8 * mm});
            skCircle(sketch, "E46.0.46.39", {"center": v(-155, 2.44) * mm, "radius": 0.8 * mm});
            skCircle(sketch, "E46.0.47.30", {"center": v(-160, 47.44) * mm, "radius": 0.8 * mm});
            skCircle(sketch, "E46.0.47.31", {"center": v(-160, 42.44) * mm, "radius": 0.8 * mm});
            skCircle(sketch, "E46.0.47.32", {"center": v(-160, 37.44) * mm, "radius": 0.8 * mm});
            skCircle(sketch, "E46.0.47.33", {"center": v(-160, 32.44) * mm, "radius": 0.8 * mm});
            skCircle(sketch, "E46.0.47.34", {"center": v(-160, 27.44) * mm, "radius": 0.8 * mm});
            skCircle(sketch, "E46.0.47.35", {"center": v(-160, 22.44) * mm, "radius": 0.8 * mm});
            skCircle(sketch, "E46.0.47.36", {"center": v(-160, 17.44) * mm, "radius": 0.8 * mm});
            skCircle(sketch, "E46.0.47.37", {"center": v(-160, 12.44) * mm, "radius": 0.8 * mm});
            skCircle(sketch, "E46.0.47.38", {"center": v(-160, 7.44) * mm, "radius": 0.8 * mm});
            skCircle(sketch, "E46.0.47.39", {"center": v(-160, 2.44) * mm, "radius": 0.8 * mm});
            skCircle(sketch, "E46.0.48.30", {"center": v(-165, 47.44) * mm, "radius": 0.8 * mm});
            skCircle(sketch, "E46.0.48.31", {"center": v(-165, 42.44) * mm, "radius": 0.8 * mm});
            skCircle(sketch, "E46.0.48.32", {"center": v(-165, 37.44) * mm, "radius": 0.8 * mm});
            skCircle(sketch, "E46.0.48.33", {"center": v(-165, 32.44) * mm, "radius": 0.8 * mm});
            skCircle(sketch, "E46.0.48.34", {"center": v(-165, 27.44) * mm, "radius": 0.8 * mm});
            skCircle(sketch, "E46.0.48.35", {"center": v(-165, 22.44) * mm, "radius": 0.8 * mm});
            skCircle(sketch, "E46.0.48.36", {"center": v(-165, 17.44) * mm, "radius": 0.8 * mm});
            skCircle(sketch, "E46.0.48.37", {"center": v(-165, 12.44) * mm, "radius": 0.8 * mm});
            skCircle(sketch, "E46.0.48.38", {"center": v(-165, 7.44) * mm, "radius": 0.8 * mm});
            skCircle(sketch, "E46.0.48.39", {"center": v(-165, 2.44) * mm, "radius": 0.8 * mm});
            skCircle(sketch, "E47.0.49.0", {"center": v(-170, 197.44) * mm, "radius": 0.8 * mm});
            skCircle(sketch, "E47.0.49.1", {"center": v(-170, 192.44) * mm, "radius": 0.8 * mm});
            skCircle(sketch, "E47.0.49.2", {"center": v(-170, 187.44) * mm, "radius": 0.8 * mm});
            skCircle(sketch, "E47.0.49.3", {"center": v(-170, 182.44) * mm, "radius": 0.8 * mm});
            skCircle(sketch, "E47.0.49.4", {"center": v(-170, 177.44) * mm, "radius": 0.8 * mm});
            skCircle(sketch, "E47.0.49.5", {"center": v(-170, 172.44) * mm, "radius": 0.8 * mm});
            skCircle(sketch, "E47.0.49.6", {"center": v(-170, 167.44) * mm, "radius": 0.8 * mm});
            skCircle(sketch, "E47.0.49.7", {"center": v(-170, 162.44) * mm, "radius": 0.8 * mm});
            skCircle(sketch, "E47.0.49.8", {"center": v(-170, 157.44) * mm, "radius": 0.8 * mm});
            skCircle(sketch, "E47.0.49.9", {"center": v(-170, 152.44) * mm, "radius": 0.8 * mm});
            skCircle(sketch, "E47.0.49.10", {"center": v(-170, 147.44) * mm, "radius": 0.8 * mm});
            skCircle(sketch, "E47.0.49.11", {"center": v(-170, 142.44) * mm, "radius": 0.8 * mm});
            skCircle(sketch, "E47.0.49.12", {"center": v(-170, 137.44) * mm, "radius": 0.8 * mm});
            skCircle(sketch, "E47.0.49.13", {"center": v(-170, 132.44) * mm, "radius": 0.8 * mm});
            skCircle(sketch, "E47.0.49.14", {"center": v(-170, 127.44) * mm, "radius": 0.8 * mm});
            skCircle(sketch, "E47.0.49.15", {"center": v(-170, 122.44) * mm, "radius": 0.8 * mm});
            skCircle(sketch, "E47.0.49.16", {"center": v(-170, 117.44) * mm, "radius": 0.8 * mm});
            skCircle(sketch, "E47.0.49.17", {"center": v(-170, 112.44) * mm, "radius": 0.8 * mm});
            skCircle(sketch, "E47.0.49.18", {"center": v(-170, 107.44) * mm, "radius": 0.8 * mm});
            skCircle(sketch, "E47.0.49.19", {"center": v(-170, 102.44) * mm, "radius": 0.8 * mm});
            skCircle(sketch, "E47.0.49.20", {"center": v(-170, 97.44) * mm, "radius": 0.8 * mm});
            skCircle(sketch, "E47.0.49.21", {"center": v(-170, 92.44) * mm, "radius": 0.8 * mm});
            skCircle(sketch, "E47.0.49.22", {"center": v(-170, 87.44) * mm, "radius": 0.8 * mm});
            skCircle(sketch, "E47.0.49.23", {"center": v(-170, 82.44) * mm, "radius": 0.8 * mm});
            skCircle(sketch, "E47.0.49.24", {"center": v(-170, 77.44) * mm, "radius": 0.8 * mm});
            skCircle(sketch, "E47.0.49.25", {"center": v(-170, 72.44) * mm, "radius": 0.8 * mm});
            skCircle(sketch, "E47.0.49.26", {"center": v(-170, 67.44) * mm, "radius": 0.8 * mm});
            skCircle(sketch, "E47.0.49.27", {"center": v(-170, 62.44) * mm, "radius": 0.8 * mm});
            skCircle(sketch, "E47.0.49.28", {"center": v(-170, 57.44) * mm, "radius": 0.8 * mm});
            skCircle(sketch, "E47.0.49.29", {"center": v(-170, 52.44) * mm, "radius": 0.8 * mm});
            skCircle(sketch, "E47.0.49.30", {"center": v(-170, 47.44) * mm, "radius": 0.8 * mm});
            skCircle(sketch, "E47.0.49.31", {"center": v(-170, 42.44) * mm, "radius": 0.8 * mm});
            skCircle(sketch, "E47.0.49.32", {"center": v(-170, 37.44) * mm, "radius": 0.8 * mm});
            skCircle(sketch, "E47.0.49.33", {"center": v(-170, 32.44) * mm, "radius": 0.8 * mm});
            skCircle(sketch, "E47.0.49.34", {"center": v(-170, 27.44) * mm, "radius": 0.8 * mm});
            skCircle(sketch, "E47.0.49.35", {"center": v(-170, 22.44) * mm, "radius": 0.8 * mm});
            skCircle(sketch, "E47.0.49.36", {"center": v(-170, 17.44) * mm, "radius": 0.8 * mm});
            skCircle(sketch, "E47.0.49.37", {"center": v(-170, 12.44) * mm, "radius": 0.8 * mm});
            skCircle(sketch, "E47.0.49.38", {"center": v(-170, 7.44) * mm, "radius": 0.8 * mm});
            skCircle(sketch, "E47.0.49.39", {"center": v(-170, 2.44) * mm, "radius": 0.8 * mm});
            skCircle(sketch, "E47.0.50.0", {"center": v(-175, 197.44) * mm, "radius": 0.8 * mm});
            skCircle(sketch, "E47.0.50.1", {"center": v(-175, 192.44) * mm, "radius": 0.8 * mm});
            skCircle(sketch, "E47.0.50.2", {"center": v(-175, 187.44) * mm, "radius": 0.8 * mm});
            skCircle(sketch, "E47.0.50.3", {"center": v(-175, 182.44) * mm, "radius": 0.8 * mm});
            skCircle(sketch, "E47.0.50.4", {"center": v(-175, 177.44) * mm, "radius": 0.8 * mm});
            skCircle(sketch, "E47.0.50.5", {"center": v(-175, 172.44) * mm, "radius": 0.8 * mm});
            skCircle(sketch, "E47.0.50.6", {"center": v(-175, 167.44) * mm, "radius": 0.8 * mm});
            skCircle(sketch, "E47.0.50.7", {"center": v(-175, 162.44) * mm, "radius": 0.8 * mm});
            skCircle(sketch, "E47.0.50.8", {"center": v(-175, 157.44) * mm, "radius": 0.8 * mm});
            skCircle(sketch, "E47.0.50.9", {"center": v(-175, 152.44) * mm, "radius": 0.8 * mm});
            skCircle(sketch, "E47.0.50.10", {"center": v(-175, 147.44) * mm, "radius": 0.8 * mm});
            skCircle(sketch, "E47.0.50.11", {"center": v(-175, 142.44) * mm, "radius": 0.8 * mm});
            skCircle(sketch, "E47.0.50.12", {"center": v(-175, 137.44) * mm, "radius": 0.8 * mm});
            skCircle(sketch, "E47.0.50.13", {"center": v(-175, 132.44) * mm, "radius": 0.8 * mm});
            skCircle(sketch, "E47.0.50.14", {"center": v(-175, 127.44) * mm, "radius": 0.8 * mm});
            skCircle(sketch, "E47.0.50.15", {"center": v(-175, 122.44) * mm, "radius": 0.8 * mm});
            skCircle(sketch, "E47.0.50.16", {"center": v(-175, 117.44) * mm, "radius": 0.8 * mm});
            skCircle(sketch, "E47.0.50.17", {"center": v(-175, 112.44) * mm, "radius": 0.8 * mm});
            skCircle(sketch, "E47.0.50.18", {"center": v(-175, 107.44) * mm, "radius": 0.8 * mm});
            skCircle(sketch, "E47.0.50.19", {"center": v(-175, 102.44) * mm, "radius": 0.8 * mm});
            skCircle(sketch, "E47.0.50.20", {"center": v(-175, 97.44) * mm, "radius": 0.8 * mm});
            skCircle(sketch, "E47.0.50.21", {"center": v(-175, 92.44) * mm, "radius": 0.8 * mm});
            skCircle(sketch, "E47.0.50.22", {"center": v(-175, 87.44) * mm, "radius": 0.8 * mm});
            skCircle(sketch, "E47.0.50.23", {"center": v(-175, 82.44) * mm, "radius": 0.8 * mm});
            skCircle(sketch, "E47.0.50.24", {"center": v(-175, 77.44) * mm, "radius": 0.8 * mm});
            skCircle(sketch, "E47.0.50.25", {"center": v(-175, 72.44) * mm, "radius": 0.8 * mm});
            skCircle(sketch, "E47.0.50.26", {"center": v(-175, 67.44) * mm, "radius": 0.8 * mm});
            skCircle(sketch, "E47.0.50.27", {"center": v(-175, 62.44) * mm, "radius": 0.8 * mm});
            skCircle(sketch, "E47.0.50.28", {"center": v(-175, 57.44) * mm, "radius": 0.8 * mm});
            skCircle(sketch, "E47.0.50.29", {"center": v(-175, 52.44) * mm, "radius": 0.8 * mm});
            skCircle(sketch, "E47.0.50.30", {"center": v(-175, 47.44) * mm, "radius": 0.8 * mm});
            skCircle(sketch, "E47.0.50.31", {"center": v(-175, 42.44) * mm, "radius": 0.8 * mm});
            skCircle(sketch, "E47.0.50.32", {"center": v(-175, 37.44) * mm, "radius": 0.8 * mm});
            skCircle(sketch, "E47.0.50.33", {"center": v(-175, 32.44) * mm, "radius": 0.8 * mm});
            skCircle(sketch, "E47.0.50.34", {"center": v(-175, 27.44) * mm, "radius": 0.8 * mm});
            skCircle(sketch, "E47.0.50.35", {"center": v(-175, 22.44) * mm, "radius": 0.8 * mm});
            skCircle(sketch, "E47.0.50.36", {"center": v(-175, 17.44) * mm, "radius": 0.8 * mm});
            skCircle(sketch, "E47.0.50.37", {"center": v(-175, 12.44) * mm, "radius": 0.8 * mm});
            skCircle(sketch, "E47.0.50.38", {"center": v(-175, 7.44) * mm, "radius": 0.8 * mm});
            skCircle(sketch, "E47.0.50.39", {"center": v(-175, 2.44) * mm, "radius": 0.8 * mm});
            skCircle(sketch, "E47.0.51.0", {"center": v(-180, 197.44) * mm, "radius": 0.8 * mm});
            skCircle(sketch, "E47.0.51.1", {"center": v(-180, 192.44) * mm, "radius": 0.8 * mm});
            skCircle(sketch, "E47.0.51.2", {"center": v(-180, 187.44) * mm, "radius": 0.8 * mm});
            skCircle(sketch, "E47.0.51.3", {"center": v(-180, 182.44) * mm, "radius": 0.8 * mm});
            skCircle(sketch, "E47.0.51.4", {"center": v(-180, 177.44) * mm, "radius": 0.8 * mm});
            skCircle(sketch, "E47.0.51.5", {"center": v(-180, 172.44) * mm, "radius": 0.8 * mm});
            skCircle(sketch, "E47.0.51.6", {"center": v(-180, 167.44) * mm, "radius": 0.8 * mm});
            skCircle(sketch, "E47.0.51.7", {"center": v(-180, 162.44) * mm, "radius": 0.8 * mm});
            skCircle(sketch, "E47.0.51.8", {"center": v(-180, 157.44) * mm, "radius": 0.8 * mm});
            skCircle(sketch, "E47.0.51.9", {"center": v(-180, 152.44) * mm, "radius": 0.8 * mm});
            skCircle(sketch, "E47.0.51.10", {"center": v(-180, 147.44) * mm, "radius": 0.8 * mm});
            skCircle(sketch, "E47.0.51.11", {"center": v(-180, 142.44) * mm, "radius": 0.8 * mm});
            skCircle(sketch, "E47.0.51.12", {"center": v(-180, 137.44) * mm, "radius": 0.8 * mm});
            skCircle(sketch, "E47.0.51.13", {"center": v(-180, 132.44) * mm, "radius": 0.8 * mm});
            skCircle(sketch, "E47.0.51.14", {"center": v(-180, 127.44) * mm, "radius": 0.8 * mm});
            skCircle(sketch, "E47.0.51.15", {"center": v(-180, 122.44) * mm, "radius": 0.8 * mm});
            skCircle(sketch, "E47.0.51.16", {"center": v(-180, 117.44) * mm, "radius": 0.8 * mm});
            skCircle(sketch, "E47.0.51.17", {"center": v(-180, 112.44) * mm, "radius": 0.8 * mm});
            skCircle(sketch, "E47.0.51.18", {"center": v(-180, 107.44) * mm, "radius": 0.8 * mm});
            skCircle(sketch, "E47.0.51.19", {"center": v(-180, 102.44) * mm, "radius": 0.8 * mm});
            skCircle(sketch, "E47.0.51.20", {"center": v(-180, 97.44) * mm, "radius": 0.8 * mm});
            skCircle(sketch, "E47.0.51.21", {"center": v(-180, 92.44) * mm, "radius": 0.8 * mm});
            skCircle(sketch, "E47.0.51.22", {"center": v(-180, 87.44) * mm, "radius": 0.8 * mm});
            skCircle(sketch, "E47.0.51.23", {"center": v(-180, 82.44) * mm, "radius": 0.8 * mm});
            skCircle(sketch, "E47.0.51.24", {"center": v(-180, 77.44) * mm, "radius": 0.8 * mm});
            skCircle(sketch, "E47.0.51.25", {"center": v(-180, 72.44) * mm, "radius": 0.8 * mm});
            skCircle(sketch, "E47.0.51.26", {"center": v(-180, 67.44) * mm, "radius": 0.8 * mm});
            skCircle(sketch, "E47.0.51.27", {"center": v(-180, 62.44) * mm, "radius": 0.8 * mm});
            skCircle(sketch, "E47.0.51.28", {"center": v(-180, 57.44) * mm, "radius": 0.8 * mm});
            skCircle(sketch, "E47.0.51.29", {"center": v(-180, 52.44) * mm, "radius": 0.8 * mm});
            skCircle(sketch, "E47.0.51.30", {"center": v(-180, 47.44) * mm, "radius": 0.8 * mm});
            skCircle(sketch, "E47.0.51.31", {"center": v(-180, 42.44) * mm, "radius": 0.8 * mm});
            skCircle(sketch, "E47.0.51.32", {"center": v(-180, 37.44) * mm, "radius": 0.8 * mm});
            skCircle(sketch, "E47.0.51.33", {"center": v(-180, 32.44) * mm, "radius": 0.8 * mm});
            skCircle(sketch, "E47.0.51.34", {"center": v(-180, 27.44) * mm, "radius": 0.8 * mm});
            skCircle(sketch, "E47.0.51.35", {"center": v(-180, 22.44) * mm, "radius": 0.8 * mm});
            skCircle(sketch, "E47.0.51.36", {"center": v(-180, 17.44) * mm, "radius": 0.8 * mm});
            skCircle(sketch, "E47.0.51.37", {"center": v(-180, 12.44) * mm, "radius": 0.8 * mm});
            skCircle(sketch, "E47.0.51.38", {"center": v(-180, 7.44) * mm, "radius": 0.8 * mm});
            skCircle(sketch, "E47.0.51.39", {"center": v(-180, 2.44) * mm, "radius": 0.8 * mm});
            skCircle(sketch, "E47.0.52.0", {"center": v(-185, 197.44) * mm, "radius": 0.8 * mm});
            skCircle(sketch, "E47.0.52.1", {"center": v(-185, 192.44) * mm, "radius": 0.8 * mm});
            skCircle(sketch, "E47.0.52.2", {"center": v(-185, 187.44) * mm, "radius": 0.8 * mm});
            skCircle(sketch, "E47.0.52.3", {"center": v(-185, 182.44) * mm, "radius": 0.8 * mm});
            skCircle(sketch, "E47.0.52.4", {"center": v(-185, 177.44) * mm, "radius": 0.8 * mm});
            skCircle(sketch, "E47.0.52.5", {"center": v(-185, 172.44) * mm, "radius": 0.8 * mm});
            skCircle(sketch, "E47.0.52.6", {"center": v(-185, 167.44) * mm, "radius": 0.8 * mm});
            skCircle(sketch, "E47.0.52.7", {"center": v(-185, 162.44) * mm, "radius": 0.8 * mm});
            skCircle(sketch, "E47.0.52.8", {"center": v(-185, 157.44) * mm, "radius": 0.8 * mm});
            skCircle(sketch, "E47.0.52.9", {"center": v(-185, 152.44) * mm, "radius": 0.8 * mm});
            skCircle(sketch, "E47.0.52.10", {"center": v(-185, 147.44) * mm, "radius": 0.8 * mm});
            skCircle(sketch, "E47.0.52.11", {"center": v(-185, 142.44) * mm, "radius": 0.8 * mm});
            skCircle(sketch, "E47.0.52.12", {"center": v(-185, 137.44) * mm, "radius": 0.8 * mm});
            skCircle(sketch, "E47.0.52.13", {"center": v(-185, 132.44) * mm, "radius": 0.8 * mm});
            skCircle(sketch, "E47.0.52.14", {"center": v(-185, 127.44) * mm, "radius": 0.8 * mm});
            skCircle(sketch, "E47.0.52.15", {"center": v(-185, 122.44) * mm, "radius": 0.8 * mm});
            skCircle(sketch, "E47.0.52.16", {"center": v(-185, 117.44) * mm, "radius": 0.8 * mm});
            skCircle(sketch, "E47.0.52.17", {"center": v(-185, 112.44) * mm, "radius": 0.8 * mm});
            skCircle(sketch, "E47.0.52.18", {"center": v(-185, 107.44) * mm, "radius": 0.8 * mm});
            skCircle(sketch, "E47.0.52.19", {"center": v(-185, 102.44) * mm, "radius": 0.8 * mm});
            skCircle(sketch, "E47.0.52.20", {"center": v(-185, 97.44) * mm, "radius": 0.8 * mm});
            skCircle(sketch, "E47.0.52.21", {"center": v(-185, 92.44) * mm, "radius": 0.8 * mm});
            skCircle(sketch, "E47.0.52.22", {"center": v(-185, 87.44) * mm, "radius": 0.8 * mm});
            skCircle(sketch, "E47.0.52.23", {"center": v(-185, 82.44) * mm, "radius": 0.8 * mm});
            skCircle(sketch, "E47.0.52.24", {"center": v(-185, 77.44) * mm, "radius": 0.8 * mm});
            skCircle(sketch, "E47.0.52.25", {"center": v(-185, 72.44) * mm, "radius": 0.8 * mm});
            skCircle(sketch, "E47.0.52.26", {"center": v(-185, 67.44) * mm, "radius": 0.8 * mm});
            skCircle(sketch, "E47.0.52.27", {"center": v(-185, 62.44) * mm, "radius": 0.8 * mm});
            skCircle(sketch, "E47.0.52.28", {"center": v(-185, 57.44) * mm, "radius": 0.8 * mm});
            skCircle(sketch, "E47.0.52.29", {"center": v(-185, 52.44) * mm, "radius": 0.8 * mm});
            skCircle(sketch, "E47.0.52.30", {"center": v(-185, 47.44) * mm, "radius": 0.8 * mm});
            skCircle(sketch, "E47.0.52.31", {"center": v(-185, 42.44) * mm, "radius": 0.8 * mm});
            skCircle(sketch, "E47.0.52.32", {"center": v(-185, 37.44) * mm, "radius": 0.8 * mm});
            skCircle(sketch, "E47.0.52.33", {"center": v(-185, 32.44) * mm, "radius": 0.8 * mm});
            skCircle(sketch, "E47.0.52.34", {"center": v(-185, 27.44) * mm, "radius": 0.8 * mm});
            skCircle(sketch, "E47.0.52.35", {"center": v(-185, 22.44) * mm, "radius": 0.8 * mm});
            skCircle(sketch, "E47.0.52.36", {"center": v(-185, 17.44) * mm, "radius": 0.8 * mm});
            skCircle(sketch, "E47.0.52.37", {"center": v(-185, 12.44) * mm, "radius": 0.8 * mm});
            skCircle(sketch, "E47.0.52.38", {"center": v(-185, 7.44) * mm, "radius": 0.8 * mm});
            skCircle(sketch, "E47.0.52.39", {"center": v(-185, 2.44) * mm, "radius": 0.8 * mm});
            skCircle(sketch, "E47.0.53.0", {"center": v(-190, 197.44) * mm, "radius": 0.8 * mm});
            skCircle(sketch, "E47.0.53.1", {"center": v(-190, 192.44) * mm, "radius": 0.8 * mm});
            skCircle(sketch, "E47.0.53.2", {"center": v(-190, 187.44) * mm, "radius": 0.8 * mm});
            skCircle(sketch, "E47.0.53.3", {"center": v(-190, 182.44) * mm, "radius": 0.8 * mm});
            skCircle(sketch, "E47.0.53.4", {"center": v(-190, 177.44) * mm, "radius": 0.8 * mm});
            skCircle(sketch, "E47.0.53.5", {"center": v(-190, 172.44) * mm, "radius": 0.8 * mm});
            skCircle(sketch, "E47.0.53.6", {"center": v(-190, 167.44) * mm, "radius": 0.8 * mm});
            skCircle(sketch, "E47.0.53.7", {"center": v(-190, 162.44) * mm, "radius": 0.8 * mm});
            skCircle(sketch, "E47.0.53.8", {"center": v(-190, 157.44) * mm, "radius": 0.8 * mm});
            skCircle(sketch, "E47.0.53.9", {"center": v(-190, 152.44) * mm, "radius": 0.8 * mm});
            skCircle(sketch, "E47.0.53.10", {"center": v(-190, 147.44) * mm, "radius": 0.8 * mm});
            skCircle(sketch, "E47.0.53.11", {"center": v(-190, 142.44) * mm, "radius": 0.8 * mm});
            skCircle(sketch, "E47.0.53.12", {"center": v(-190, 137.44) * mm, "radius": 0.8 * mm});
            skCircle(sketch, "E47.0.53.13", {"center": v(-190, 132.44) * mm, "radius": 0.8 * mm});
            skCircle(sketch, "E47.0.53.14", {"center": v(-190, 127.44) * mm, "radius": 0.8 * mm});
            skCircle(sketch, "E47.0.53.15", {"center": v(-190, 122.44) * mm, "radius": 0.8 * mm});
            skCircle(sketch, "E47.0.53.16", {"center": v(-190, 117.44) * mm, "radius": 0.8 * mm});
            skCircle(sketch, "E47.0.53.17", {"center": v(-190, 112.44) * mm, "radius": 0.8 * mm});
            skCircle(sketch, "E47.0.53.18", {"center": v(-190, 107.44) * mm, "radius": 0.8 * mm});
            skCircle(sketch, "E47.0.53.19", {"center": v(-190, 102.44) * mm, "radius": 0.8 * mm});
            skCircle(sketch, "E47.0.53.20", {"center": v(-190, 97.44) * mm, "radius": 0.8 * mm});
            skCircle(sketch, "E47.0.53.21", {"center": v(-190, 92.44) * mm, "radius": 0.8 * mm});
            skCircle(sketch, "E47.0.53.22", {"center": v(-190, 87.44) * mm, "radius": 0.8 * mm});
            skCircle(sketch, "E47.0.53.23", {"center": v(-190, 82.44) * mm, "radius": 0.8 * mm});
            skCircle(sketch, "E47.0.53.24", {"center": v(-190, 77.44) * mm, "radius": 0.8 * mm});
            skCircle(sketch, "E47.0.53.25", {"center": v(-190, 72.44) * mm, "radius": 0.8 * mm});
            skCircle(sketch, "E47.0.53.26", {"center": v(-190, 67.44) * mm, "radius": 0.8 * mm});
            skCircle(sketch, "E47.0.53.27", {"center": v(-190, 62.44) * mm, "radius": 0.8 * mm});
            skCircle(sketch, "E47.0.53.28", {"center": v(-190, 57.44) * mm, "radius": 0.8 * mm});
            skCircle(sketch, "E47.0.53.29", {"center": v(-190, 52.44) * mm, "radius": 0.8 * mm});
            skCircle(sketch, "E47.0.53.30", {"center": v(-190, 47.44) * mm, "radius": 0.8 * mm});
            skCircle(sketch, "E47.0.53.31", {"center": v(-190, 42.44) * mm, "radius": 0.8 * mm});
            skCircle(sketch, "E47.0.53.32", {"center": v(-190, 37.44) * mm, "radius": 0.8 * mm});
            skCircle(sketch, "E47.0.53.33", {"center": v(-190, 32.44) * mm, "radius": 0.8 * mm});
            skCircle(sketch, "E47.0.53.34", {"center": v(-190, 27.44) * mm, "radius": 0.8 * mm});
            skCircle(sketch, "E47.0.53.35", {"center": v(-190, 22.44) * mm, "radius": 0.8 * mm});
            skCircle(sketch, "E47.0.53.36", {"center": v(-190, 17.44) * mm, "radius": 0.8 * mm});
            skCircle(sketch, "E47.0.53.37", {"center": v(-190, 12.44) * mm, "radius": 0.8 * mm});
            skCircle(sketch, "E47.0.53.38", {"center": v(-190, 7.44) * mm, "radius": 0.8 * mm});
            skCircle(sketch, "E47.0.53.39", {"center": v(-190, 2.44) * mm, "radius": 0.8 * mm});
            skCircle(sketch, "E47.0.54.0", {"center": v(-195, 197.44) * mm, "radius": 0.8 * mm});
            skCircle(sketch, "E47.0.54.1", {"center": v(-195, 192.44) * mm, "radius": 0.8 * mm});
            skCircle(sketch, "E47.0.54.2", {"center": v(-195, 187.44) * mm, "radius": 0.8 * mm});
            skCircle(sketch, "E47.0.54.3", {"center": v(-195, 182.44) * mm, "radius": 0.8 * mm});
            skCircle(sketch, "E47.0.54.4", {"center": v(-195, 177.44) * mm, "radius": 0.8 * mm});
            skCircle(sketch, "E47.0.54.5", {"center": v(-195, 172.44) * mm, "radius": 0.8 * mm});
            skCircle(sketch, "E47.0.54.6", {"center": v(-195, 167.44) * mm, "radius": 0.8 * mm});
            skCircle(sketch, "E47.0.54.7", {"center": v(-195, 162.44) * mm, "radius": 0.8 * mm});
            skCircle(sketch, "E47.0.54.8", {"center": v(-195, 157.44) * mm, "radius": 0.8 * mm});
            skCircle(sketch, "E47.0.54.9", {"center": v(-195, 152.44) * mm, "radius": 0.8 * mm});
            skCircle(sketch, "E47.0.54.10", {"center": v(-195, 147.44) * mm, "radius": 0.8 * mm});
            skCircle(sketch, "E47.0.54.11", {"center": v(-195, 142.44) * mm, "radius": 0.8 * mm});
            skCircle(sketch, "E47.0.54.12", {"center": v(-195, 137.44) * mm, "radius": 0.8 * mm});
            skCircle(sketch, "E47.0.54.13", {"center": v(-195, 132.44) * mm, "radius": 0.8 * mm});
            skCircle(sketch, "E47.0.54.14", {"center": v(-195, 127.44) * mm, "radius": 0.8 * mm});
            skCircle(sketch, "E47.0.54.15", {"center": v(-195, 122.44) * mm, "radius": 0.8 * mm});
            skCircle(sketch, "E47.0.54.16", {"center": v(-195, 117.44) * mm, "radius": 0.8 * mm});
            skCircle(sketch, "E47.0.54.17", {"center": v(-195, 112.44) * mm, "radius": 0.8 * mm});
            skCircle(sketch, "E47.0.54.18", {"center": v(-195, 107.44) * mm, "radius": 0.8 * mm});
            skCircle(sketch, "E47.0.54.19", {"center": v(-195, 102.44) * mm, "radius": 0.8 * mm});
            skCircle(sketch, "E47.0.54.20", {"center": v(-195, 97.44) * mm, "radius": 0.8 * mm});
            skCircle(sketch, "E47.0.54.21", {"center": v(-195, 92.44) * mm, "radius": 0.8 * mm});
            skCircle(sketch, "E47.0.54.22", {"center": v(-195, 87.44) * mm, "radius": 0.8 * mm});
            skCircle(sketch, "E47.0.54.23", {"center": v(-195, 82.44) * mm, "radius": 0.8 * mm});
            skCircle(sketch, "E47.0.54.24", {"center": v(-195, 77.44) * mm, "radius": 0.8 * mm});
            skCircle(sketch, "E47.0.54.25", {"center": v(-195, 72.44) * mm, "radius": 0.8 * mm});
            skCircle(sketch, "E47.0.54.26", {"center": v(-195, 67.44) * mm, "radius": 0.8 * mm});
            skCircle(sketch, "E47.0.54.27", {"center": v(-195, 62.44) * mm, "radius": 0.8 * mm});
            skCircle(sketch, "E47.0.54.28", {"center": v(-195, 57.44) * mm, "radius": 0.8 * mm});
            skCircle(sketch, "E47.0.54.29", {"center": v(-195, 52.44) * mm, "radius": 0.8 * mm});
            skCircle(sketch, "E47.0.54.30", {"center": v(-195, 47.44) * mm, "radius": 0.8 * mm});
            skCircle(sketch, "E47.0.54.31", {"center": v(-195, 42.44) * mm, "radius": 0.8 * mm});
            skCircle(sketch, "E47.0.54.32", {"center": v(-195, 37.44) * mm, "radius": 0.8 * mm});
            skCircle(sketch, "E47.0.54.33", {"center": v(-195, 32.44) * mm, "radius": 0.8 * mm});
            skCircle(sketch, "E47.0.54.34", {"center": v(-195, 27.44) * mm, "radius": 0.8 * mm});
            skCircle(sketch, "E47.0.54.35", {"center": v(-195, 22.44) * mm, "radius": 0.8 * mm});
            skCircle(sketch, "E47.0.54.36", {"center": v(-195, 17.44) * mm, "radius": 0.8 * mm});
            skCircle(sketch, "E47.0.54.37", {"center": v(-195, 12.44) * mm, "radius": 0.8 * mm});
            skCircle(sketch, "E47.0.54.38", {"center": v(-195, 7.44) * mm, "radius": 0.8 * mm});
            skCircle(sketch, "E47.0.54.39", {"center": v(-195, 2.44) * mm, "radius": 0.8 * mm});
            skSolve(sketch);
        }
        {
            var Q0;
            Q0 = qSketchRegion(id + "F2", true);
            extrude(context, id + "F3", {"entities" : qUnion([Q0]), "operationType" : NewBodyOperationType.REMOVE, "oppositeDirection" : true, "depth" : 25 * mm, "offsetDistance" : 25 * mm, "hasSecondDirection" : true, "secondDirectionOppositeDirection" : false, "secondDirectionDepth" : 60 * mm});
        }
        {
            var Q0;
            {var subQ0=sQuery(id+"F0.wireOp",EDGE,"E1");var subQ15=makeQuery(id+"F0.imprint","INTERSECT",VERTEX,{"derivedFrom":[subQ0,sQuery(id+"F0.wireOp",EDGE,"E16")]});Q0=makeQuery(id+"F0.imprint","IMPRINT",FACE,{"disambiguationData":[TD([[makeQuery(id+"F0.imprint","IMPRINT",EDGE,{"disambiguationData":[TD([[subQ15,1.0]])],"derivedFrom":subQ0}),-1.0]])]});}
            var Q1;
            {var subQ3=sQuery(id+"F0.wireOp",EDGE,"E13");Q1=makeQuery(id+"F0.imprint","IMPRINT",FACE,{"disambiguationData":[TD([[makeQuery(id+"F0.imprint","IMPRINT",EDGE,{"derivedFrom":subQ3}),1.0]])]});}
            var Q2;
            {var subQ0=sQuery(id+"F0.wireOp",EDGE,"E11");Q2=makeQuery(id+"F0.imprint","IMPRINT",FACE,{"disambiguationData":[TD([[makeQuery(id+"F0.imprint","IMPRINT",EDGE,{"derivedFrom":subQ0}),1.0]])]});}
            var Q3;
            {var subQ0=sQuery(id+"F0.wireOp",EDGE,"E11");Q3=makeQuery(id+"F0.imprint","IMPRINT",FACE,{"disambiguationData":[TD([[makeQuery(id+"F0.imprint","IMPRINT",EDGE,{"derivedFrom":subQ0}),-1.0]])]});}
            var Q4;
            {var subQ0=sQuery(id+"F0.wireOp",EDGE,"E12");Q4=makeQuery(id+"F0.imprint","IMPRINT",FACE,{"disambiguationData":[TD([[makeQuery(id+"F0.imprint","IMPRINT",EDGE,{"derivedFrom":subQ0}),-1.0]])]});}
            var Q5;
            {var subQ0=sQuery(id+"F0.wireOp",EDGE,"E10.2.0.0");Q5=makeQuery(id+"F0.imprint","IMPRINT",FACE,{"disambiguationData":[TD([[makeQuery(id+"F0.imprint","IMPRINT",EDGE,{"derivedFrom":subQ0}),1.0]])]});}
            var Q6;
            {var subQ0=sQuery(id+"F0.wireOp",EDGE,"E14");Q6=makeQuery(id+"F0.imprint","IMPRINT",FACE,{"disambiguationData":[TD([[makeQuery(id+"F0.imprint","IMPRINT",EDGE,{"derivedFrom":subQ0}),-1.0]])]});}
            var Q7;
            {var subQ0=sQuery(id+"F0.wireOp",EDGE,"E10.2.0.0");Q7=makeQuery(id+"F0.imprint","IMPRINT",FACE,{"disambiguationData":[TD([[makeQuery(id+"F0.imprint","IMPRINT",EDGE,{"derivedFrom":subQ0}),-1.0]])]});}
            var Q8;
            {var subQ0=sQuery(id+"F0.wireOp",EDGE,"E10.1.0.0");Q8=makeQuery(id+"F0.imprint","IMPRINT",FACE,{"disambiguationData":[TD([[makeQuery(id+"F0.imprint","IMPRINT",EDGE,{"derivedFrom":subQ0}),1.0]])]});}
            var Q9;
            {var subQ0=sQuery(id+"F0.wireOp",EDGE,"E10.1.0.0");Q9=makeQuery(id+"F0.imprint","IMPRINT",FACE,{"disambiguationData":[TD([[makeQuery(id+"F0.imprint","IMPRINT",EDGE,{"derivedFrom":subQ0}),-1.0]])]});}
            var Q10;
            {var subQ0=sQuery(id+"F0.wireOp",EDGE,"E16");Q10=makeQuery(id+"F0.imprint","IMPRINT",FACE,{"disambiguationData":[TD([[makeQuery(id+"F0.imprint","IMPRINT",EDGE,{"derivedFrom":subQ0}),-1.0]])]});}
            var Q11;
            {var subQ0=sQuery(id+"F0.wireOp",EDGE,"E5");Q11=makeQuery(id+"F0.imprint","IMPRINT",FACE,{"disambiguationData":[TD([[makeQuery(id+"F0.imprint","IMPRINT",EDGE,{"derivedFrom":subQ0}),1.0]])]});}
            var Q12;
            {var subQ0=sQuery(id+"F0.wireOp",EDGE,"E5");Q12=makeQuery(id+"F0.imprint","IMPRINT",FACE,{"disambiguationData":[TD([[makeQuery(id+"F0.imprint","IMPRINT",EDGE,{"derivedFrom":subQ0}),-1.0]])]});}
            var Q13;
            {var subQ0=sQuery(id+"F0.wireOp",EDGE,"E18");Q13=makeQuery(id+"F0.imprint","IMPRINT",FACE,{"disambiguationData":[TD([[makeQuery(id+"F0.imprint","IMPRINT",EDGE,{"derivedFrom":subQ0}),-1.0]])]});}
            var Q14;
            {var subQ0=sQuery(id+"F0.wireOp",EDGE,"E6");Q14=makeQuery(id+"F0.imprint","IMPRINT",FACE,{"disambiguationData":[TD([[makeQuery(id+"F0.imprint","IMPRINT",EDGE,{"derivedFrom":subQ0}),1.0]])]});}
            var Q15;
            {var subQ0=sQuery(id+"F0.wireOp",EDGE,"E6");Q15=makeQuery(id+"F0.imprint","IMPRINT",FACE,{"disambiguationData":[TD([[makeQuery(id+"F0.imprint","IMPRINT",EDGE,{"derivedFrom":subQ0}),-1.0]])]});}
            var Q16;
            {var subQ0=sQuery(id+"F0.wireOp",EDGE,"E20");Q16=makeQuery(id+"F0.imprint","IMPRINT",FACE,{"disambiguationData":[TD([[makeQuery(id+"F0.imprint","IMPRINT",EDGE,{"derivedFrom":subQ0}),-1.0]])]});}
            var Q17;
            {var subQ0=sQuery(id+"F0.wireOp",EDGE,"E7");Q17=makeQuery(id+"F0.imprint","IMPRINT",FACE,{"disambiguationData":[TD([[makeQuery(id+"F0.imprint","IMPRINT",EDGE,{"derivedFrom":subQ0}),1.0]])]});}
            var Q18;
            {var subQ0=sQuery(id+"F0.wireOp",EDGE,"E7");Q18=makeQuery(id+"F0.imprint","IMPRINT",FACE,{"disambiguationData":[TD([[makeQuery(id+"F0.imprint","IMPRINT",EDGE,{"derivedFrom":subQ0}),-1.0]])]});}
            var Q19;
            {var subQ0=sQuery(id+"F0.wireOp",EDGE,"E22");Q19=makeQuery(id+"F0.imprint","IMPRINT",FACE,{"disambiguationData":[TD([[makeQuery(id+"F0.imprint","IMPRINT",EDGE,{"derivedFrom":subQ0}),-1.0]])]});}
            var Q20;
            {var subQ0=sQuery(id+"F0.wireOp",EDGE,"E8");Q20=makeQuery(id+"F0.imprint","IMPRINT",FACE,{"disambiguationData":[TD([[makeQuery(id+"F0.imprint","IMPRINT",EDGE,{"derivedFrom":subQ0}),1.0]])]});}
            var Q21;
            {var subQ0=sQuery(id+"F0.wireOp",EDGE,"E8");Q21=makeQuery(id+"F0.imprint","IMPRINT",FACE,{"disambiguationData":[TD([[makeQuery(id+"F0.imprint","IMPRINT",EDGE,{"derivedFrom":subQ0}),-1.0]])]});}
            var Q22;
            {var subQ3=sQuery(id+"F0.wireOp",EDGE,"E27");Q22=makeQuery(id+"F0.imprint","IMPRINT",FACE,{"disambiguationData":[TD([[makeQuery(id+"F0.imprint","IMPRINT",EDGE,{"derivedFrom":subQ3}),1.0]])]});}
            var Q23;
            {var subQ0=sQuery(id+"F0.wireOp",EDGE,"E9.1.0.0");Q23=makeQuery(id+"F0.imprint","IMPRINT",FACE,{"disambiguationData":[TD([[makeQuery(id+"F0.imprint","IMPRINT",EDGE,{"derivedFrom":subQ0}),1.0]])]});}
            var Q24;
            {var subQ0=sQuery(id+"F0.wireOp",EDGE,"E9.1.0.0");Q24=makeQuery(id+"F0.imprint","IMPRINT",FACE,{"disambiguationData":[TD([[makeQuery(id+"F0.imprint","IMPRINT",EDGE,{"derivedFrom":subQ0}),-1.0]])]});}
            var Q25;
            {var subQ0=sQuery(id+"F0.wireOp",EDGE,"E26");Q25=makeQuery(id+"F0.imprint","IMPRINT",FACE,{"disambiguationData":[TD([[makeQuery(id+"F0.imprint","IMPRINT",EDGE,{"derivedFrom":subQ0}),-1.0]])]});}
            var Q26;
            {var subQ0=sQuery(id+"F0.wireOp",EDGE,"E9.2.0.0");Q26=makeQuery(id+"F0.imprint","IMPRINT",FACE,{"disambiguationData":[TD([[makeQuery(id+"F0.imprint","IMPRINT",EDGE,{"derivedFrom":subQ0}),1.0]])]});}
            var Q27;
            {var subQ0=sQuery(id+"F0.wireOp",EDGE,"E9.2.0.0");Q27=makeQuery(id+"F0.imprint","IMPRINT",FACE,{"disambiguationData":[TD([[makeQuery(id+"F0.imprint","IMPRINT",EDGE,{"derivedFrom":subQ0}),-1.0]])]});}
            var Q28;
            {var subQ0=sQuery(id+"F0.wireOp",EDGE,"E28");Q28=makeQuery(id+"F0.imprint","IMPRINT",FACE,{"disambiguationData":[TD([[makeQuery(id+"F0.imprint","IMPRINT",EDGE,{"derivedFrom":subQ0}),-1.0]])]});}
            var Q29;
            {var subQ0=sQuery(id+"F0.wireOp",EDGE,"E9.3.0.0");Q29=makeQuery(id+"F0.imprint","IMPRINT",FACE,{"disambiguationData":[TD([[makeQuery(id+"F0.imprint","IMPRINT",EDGE,{"derivedFrom":subQ0}),1.0]])]});}
            var Q30;
            {var subQ0=sQuery(id+"F0.wireOp",EDGE,"E9.3.0.0");Q30=makeQuery(id+"F0.imprint","IMPRINT",FACE,{"disambiguationData":[TD([[makeQuery(id+"F0.imprint","IMPRINT",EDGE,{"derivedFrom":subQ0}),-1.0]])]});}
            var Q31;
            {var subQ0=sQuery(id+"F0.wireOp",EDGE,"E30");Q31=makeQuery(id+"F0.imprint","IMPRINT",FACE,{"disambiguationData":[TD([[makeQuery(id+"F0.imprint","IMPRINT",EDGE,{"derivedFrom":subQ0}),-1.0]])]});}
            var Q32;
            {var subQ0=sQuery(id+"F0.wireOp",EDGE,"E9.4.0.0");Q32=makeQuery(id+"F0.imprint","IMPRINT",FACE,{"disambiguationData":[TD([[makeQuery(id+"F0.imprint","IMPRINT",EDGE,{"derivedFrom":subQ0}),1.0]])]});}
            var Q33;
            {var subQ0=sQuery(id+"F0.wireOp",EDGE,"E9.4.0.0");Q33=makeQuery(id+"F0.imprint","IMPRINT",FACE,{"disambiguationData":[TD([[makeQuery(id+"F0.imprint","IMPRINT",EDGE,{"derivedFrom":subQ0}),-1.0]])]});}
            var Q34;
            {var subQ0=sQuery(id+"F0.wireOp",EDGE,"E33");Q34=makeQuery(id+"F0.imprint","IMPRINT",FACE,{"disambiguationData":[TD([[makeQuery(id+"F0.imprint","IMPRINT",EDGE,{"derivedFrom":subQ0}),-1.0]])]});}
            var Q35;
            {var subQ0=sQuery(id+"F0.wireOp",EDGE,"E9.5.0.0");Q35=makeQuery(id+"F0.imprint","IMPRINT",FACE,{"disambiguationData":[TD([[makeQuery(id+"F0.imprint","IMPRINT",EDGE,{"derivedFrom":subQ0}),1.0]])]});}
            var Q36;
            {var subQ0=sQuery(id+"F0.wireOp",EDGE,"E9.5.0.0");Q36=makeQuery(id+"F0.imprint","IMPRINT",FACE,{"disambiguationData":[TD([[makeQuery(id+"F0.imprint","IMPRINT",EDGE,{"derivedFrom":subQ0}),-1.0]])]});}
            var Q37;
            {var subQ0=sQuery(id+"F0.wireOp",EDGE,"E34");Q37=makeQuery(id+"F0.imprint","IMPRINT",FACE,{"disambiguationData":[TD([[makeQuery(id+"F0.imprint","IMPRINT",EDGE,{"derivedFrom":subQ0}),-1.0]])]});}
            var Q38;
            {var subQ0=sQuery(id+"F0.wireOp",EDGE,"E9.6.0.0");Q38=makeQuery(id+"F0.imprint","IMPRINT",FACE,{"disambiguationData":[TD([[makeQuery(id+"F0.imprint","IMPRINT",EDGE,{"derivedFrom":subQ0}),1.0]])]});}
            var Q39;
            {var subQ0=sQuery(id+"F0.wireOp",EDGE,"E9.6.0.0");Q39=makeQuery(id+"F0.imprint","IMPRINT",FACE,{"disambiguationData":[TD([[makeQuery(id+"F0.imprint","IMPRINT",EDGE,{"derivedFrom":subQ0}),-1.0]])]});}
            var Q40;
            {var subQ3=sQuery(id+"F0.wireOp",EDGE,"E36");Q40=makeQuery(id+"F0.imprint","IMPRINT",FACE,{"disambiguationData":[TD([[makeQuery(id+"F0.imprint","IMPRINT",EDGE,{"derivedFrom":subQ3}),-1.0]])]});}
            extrude(context, id + "F4", {"entities" : qUnion([Q0, Q1, Q2, Q3, Q4, Q5, Q6, Q7, Q8, Q9, Q10, Q11, Q12, Q13, Q14, Q15, Q16, Q17, Q18, Q19, Q20, Q21, Q22, Q23, Q24, Q25, Q26, Q27, Q28, Q29, Q30, Q31, Q32, Q33, Q34, Q35, Q36, Q37, Q38, Q39, Q40]), "operationType" : NewBodyOperationType.ADD, "oppositeDirection" : true, "depth" : 5 * mm, "offsetDistance" : 25 * mm});
        }
        {
            var Q0;
            {var subQ0=sQuery(id+"F0.wireOp",EDGE,"E1");var subQ15=makeQuery(id+"F0.imprint","INTERSECT",VERTEX,{"derivedFrom":[subQ0,sQuery(id+"F0.wireOp",EDGE,"E16")]});Q0=makeQuery(id+"F0.imprint","IMPRINT",FACE,{"disambiguationData":[TD([[makeQuery(id+"F0.imprint","IMPRINT",EDGE,{"disambiguationData":[TD([[subQ15,1.0]])],"derivedFrom":subQ0}),-1.0]])]});}
            extrude(context, id + "F5", {"entities" : qUnion([Q0]), "operationType" : NewBodyOperationType.ADD, "depth" : 135 * mm, "offsetDistance" : 25 * mm});
        }
        {
            var Q0;
            {var subQ0=sQuery(id+"F0.wireOp",EDGE,"E1");var subQ1=sQuery(id+"F0.wireOp",EDGE,"E4");Q0=makeQuery(id+"F5.boolean.opBoolean","MERGE",FACE,{"derivedFrom":[makeQuery(id+"F1.opExtrude","CAP_FACE",FACE,{"disambiguationData":[OSD([subQ0,sQuery(id+"F0.wireOp",EDGE,"E3"),subQ1,sQuery(id+"F0.wireOp",EDGE,"E18"),sQuery(id+"F0.wireOp",EDGE,"E19")])],"isStart":false}),makeQuery(id+"F1.opExtrude","CAP_FACE",FACE,{"disambiguationData":[OSD([subQ0,subQ1,sQuery(id+"F0.wireOp",EDGE,"E16"),sQuery(id+"F0.wireOp",EDGE,"E17")])],"isStart":false}),makeQuery(id+"F1.opExtrude","CAP_FACE",FACE,{"disambiguationData":[OSD([subQ0,subQ1,sQuery(id+"F0.wireOp",EDGE,"E14"),sQuery(id+"F0.wireOp",EDGE,"E15")])],"isStart":false}),makeQuery(id+"F1.opExtrude","CAP_FACE",FACE,{"disambiguationData":[OSD([subQ0,subQ1,sQuery(id+"F0.wireOp",EDGE,"E12"),sQuery(id+"F0.wireOp",EDGE,"E13")])],"isStart":false}),makeQuery(id+"F5.opExtrude","CAP_FACE",FACE,{"disambiguationData":[OSD([sQuery(id+"F0.wireOp",EDGE,"E0"),subQ0,sQuery(id+"F0.wireOp",EDGE,"E2"),sQuery(id+"F0.wireOp",EDGE,"E39")])],"isStart":false})]});}
            var sketch = newSketch(context, id + "F6", { "sketchPlane" : qUnion([Q0])});
            skLineSegment(sketch, "E48", {"start": v(0, -87) * mm, "end": v(-152.4, 141.6) * mm});
            skLineSegment(sketch, "E49", {"start": v(-152.4, 141.6) * mm, "end": v(-76.2, 141.6) * mm});
            skPoint(sketch, "E50", {"position": v(0, -83.04) * mm});
            skLineSegment(sketch, "E51", {"start": v(0, -83.04) * mm, "end": v(0, -87) * mm});
            skLineSegment(sketch, "E52", {"start": v(-74.88, 141.6) * mm, "end": v(-76.2, 141.6) * mm});
            skLineSegment(sketch, "E53", {"start": v(-74.88, 141.6) * mm, "end": v(0, -83.04) * mm});
            skLineSegment(sketch, "E54", {"start": v(-152.4, 141.6) * mm, "end": v(-74.88, 141.6) * mm});
            skSolve(sketch);
        }
        {
            var Q0;
            Q0 = qSketchRegion(id + "F6", true);
            extrude(context, id + "F7", {"entities" : qUnion([Q0]), "operationType" : NewBodyOperationType.ADD, "depth" : 5 * mm, "offsetDistance" : 25 * mm});
        }
    });
